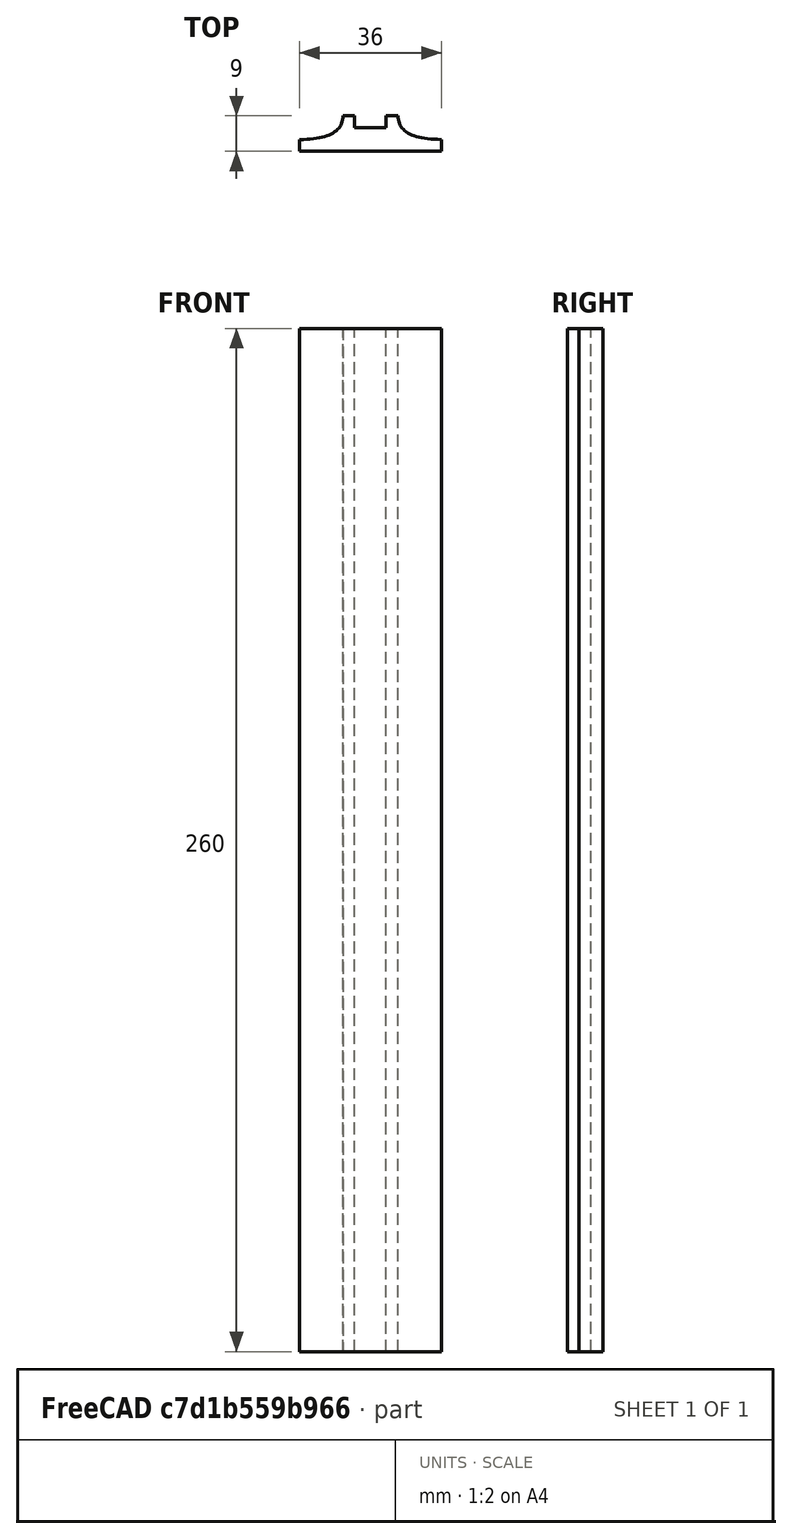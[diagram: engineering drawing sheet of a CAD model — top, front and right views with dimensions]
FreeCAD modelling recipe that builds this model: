
FCSTD DOCUMENT  (FreeCAD 0.19R0.19.2)
Label: laptopStand304
License: All rights reserved
LicenseURL: http://en.wikipedia.org/wiki/All_rights_reserved
objects: Sketcher::SketchObject×12, Part::Extrusion×1
note: 13 computed .brp shape members not serialized (recipe doc carries the construction recipe); baked Part::Feature solids carry a one-line shape summary decoded from their .brp

FEATURE [Sketcher::SketchObject] Sketch001  label="legTop"
  FullyConstrained = true
  MapMode = 4
  Placement = pos=(0,0,0) rot=(0.57735,0.57735,0.57735;2.0944rad)
  sketch-geometry (41):
    g0: BSplineCurve PolesCount=3 KnotsCount=2 Degree=2 IsPeriodic=0
    g1: ArcOfCircle CenterX=73.1223 CenterY=-32.291 CenterZ=0 NormalX=0 NormalY=0 NormalZ=1 AngleXU=0 Radius=13 StartAngle=5.92268 EndAngle=9.06428
    g2: ArcOfCircle CenterX=66.7816 CenterY=-49.1439 CenterZ=0 NormalX=0 NormalY=0 NormalZ=1 AngleXU=0 Radius=13 StartAngle=2.78068 EndAngle=5.92131
    g3-g6: Circle x4 (B-spline internal-alignment scaffolding for g7; pole/knot coordinates omitted)
    g7: BSplineCurve PolesCount=4 KnotsCount=2 Degree=3 IsPeriodic=0
    g8: GeomPoint X=28.8094 Y=-19.0875 Z=0
    g9: GeomPoint X=47.0443 Y=-50.4712 Z=0
    g10: Circle CenterX=53.5586 CenterY=-23.2695 CenterZ=0 NormalX=0 NormalY=0 NormalZ=1 AngleXU=0 Radius=3.24518
    g11: LineSegment StartX=17.2232 StartY=-16.0875 StartZ=0 EndX=17.2232 EndY=-19.0875 EndZ=0
    g12: ArcOfCircle CenterX=17.2475 CenterY=-181.166 CenterZ=0 NormalX=0 NormalY=0 NormalZ=1 AngleXU=0 Radius=13 StartAngle=5.92268 EndAngle=7.49361
    g13: ArcOfCircle CenterX=29.5716 CenterY=-148.408 CenterZ=0 NormalX=0 NormalY=0 NormalZ=1 AngleXU=0 Radius=13 StartAngle=4.35228 EndAngle=5.92131
    g14: ArcOfCircle CenterX=35.8967 CenterY=-131.555 CenterZ=0 NormalX=0 NormalY=0 NormalZ=1 AngleXU=0 Radius=13 StartAngle=5.92268 EndAngle=7.49902
    g15: ArcOfCircle CenterX=48.1805 CenterY=-98.7782 CenterZ=0 NormalX=0 NormalY=0 NormalZ=1 AngleXU=0 Radius=13 StartAngle=4.34921 EndAngle=5.92131
    g16: ArcOfCircle CenterX=54.5183 CenterY=-81.9247 CenterZ=0 NormalX=0 NormalY=0 NormalZ=1 AngleXU=0 Radius=13 StartAngle=5.92268 EndAngle=8.70432
    g17: ArcOfCircle CenterX=20.184 CenterY=-217.506 CenterZ=0 NormalX=0 NormalY=0 NormalZ=1 AngleXU=0 Radius=3.81084 StartAngle=1.88136 EndAngle=6.80465
    g18: ArcOfCircle CenterX=36.3663 CenterY=-113.042 CenterZ=0 NormalX=0 NormalY=0 NormalZ=1 AngleXU=0 Radius=3.60555 StartAngle=0.230024 EndAngle=5.3372
    g19: ArcOfCircle CenterX=17.7945 CenterY=-162.686 CenterZ=0 NormalX=0 NormalY=0 NormalZ=1 AngleXU=0 Radius=3.60555 StartAngle=0.230024 EndAngle=5.3372
    g20: ArcOfCircle CenterX=49.8795 CenterY=-62.6074 CenterZ=0 NormalX=0 NormalY=0 NormalZ=1 AngleXU=0 Radius=3.84187 StartAngle=4.46973 EndAngle=9.40343
    g21: LineSegment StartX=48.9563 StartY=-66.3367 StartZ=0 EndX=44.7488 EndY=-73.3482 EndZ=0
    g22: LineSegment StartX=41.085 StartY=-66.3176 StartZ=0 EndX=46.0385 EndY=-62.5254 EndZ=0
    g23: LineSegment StartX=47.0443 StartY=-50.4712 StartZ=0 EndX=41.085 EndY=-66.3176 EndZ=0
    g24: LineSegment StartX=17.2232 StartY=-16.0875 StartZ=0 EndX=117.223 EndY=-16.0875 EndZ=0
    g25: LineSegment StartX=28.8094 StartY=-19.0875 StartZ=0 EndX=17.2232 EndY=-19.0875 EndZ=0
    g26: LineSegment StartX=117.223 StartY=-16.0875 StartZ=0 EndX=117.223 EndY=-19.0875 EndZ=0
    g27: LineSegment StartX=85.2866 StartY=-36.8766 StartZ=0 EndX=78.9396 EndY=-53.7463 EndZ=0
    g28: LineSegment StartX=60.9579 StartY=-27.7053 StartZ=0 EndX=54.6191 EndY=-44.5532 EndZ=0
    g29: LineSegment StartX=23.4884 StartY=-215.608 StartZ=0 EndX=94.6579 EndY=-26.1359 EndZ=0
    g30: LineSegment StartX=19.0195 StartY=-213.878 StartZ=0 EndX=29.4118 EndY=-185.752 EndZ=0
    g31: LineSegment StartX=22.7134 StartY=-166.661 StartZ=0 EndX=21.8316 EndY=-169.001 EndZ=0
    g32: LineSegment StartX=19.9036 StartY=-165.61 StartZ=0 EndX=22.7134 EndY=-166.661 EndZ=0
    g33: LineSegment StartX=21.3051 StartY=-161.864 StartZ=0 EndX=24.1149 EndY=-162.915 EndZ=0
    g34: LineSegment StartX=24.1149 StartY=-162.915 StartZ=0 EndX=24.9906 EndY=-160.574 EndZ=0
    g35: LineSegment StartX=41.7296 StartY=-153.01 StartZ=0 EndX=48.061 EndY=-136.14 EndZ=0
    g36: LineSegment StartX=41.2852 StartY=-117.017 StartZ=0 EndX=40.4148 EndY=-119.365 EndZ=0
    g37: LineSegment StartX=38.4753 StartY=-115.966 StartZ=0 EndX=41.2852 EndY=-117.017 EndZ=0
    g38: LineSegment StartX=39.8769 StartY=-112.22 StartZ=0 EndX=42.6867 EndY=-113.271 EndZ=0
    g39: LineSegment StartX=42.6867 StartY=-113.271 StartZ=0 EndX=43.5622 EndY=-110.93 EndZ=0
    g40: LineSegment StartX=66.6827 StartY=-86.5104 StartZ=0 EndX=60.3386 EndY=-103.381 EndZ=0
  constraints (65):
    c: Block(g0)
    c: Block(g1)
    c: Block(g2)
    c: Weight(g3) = 1
    c: Equal(g3,g4)
    c: Equal(g3,g5)
    c: Equal(g3,g6)
    c: InternalAlignment(g3-g6 -> g7) x4
    c: InternalAlignment(g8,g7)
    c: InternalAlignment(g9,g7)
    c: Block(g10)
    c: Block(g7)
    c: Vertical(g11)
    c: Block(g12)
    c: Block(g13)
    c: Block(g14)
    c: Block(g15)
    c: Block(g16)
    c: Block(g17)
    c: Block(g18)
    c: Block(g19)
    c: Block(g20)
    c: Coincident(g21,g20)
    c: Coincident(g21,g16)
    c: Coincident(g22,g20)
    c: Block(g22)
    c: Coincident(g23,g7)
    c: Coincident(g23,g22)
    c: Coincident(g24,g11)
    c: Horizontal(g24)
    c: Coincident(g25,g7)
    c: Coincident(g25,g11)
    c: Horizontal(g25)
    c: Coincident(g26,g24)
    c: Coincident(g26,g0)
    c: Vertical(g26)
    c: Block(g24)
    c: Coincident(g27,g1)
    c: Coincident(g27,g2)
    c: Coincident(g28,g1)
    c: Coincident(g28,g2)
    c: Coincident(g29,g17)
    c: Coincident(g29,g0)
    c: Coincident(g30,g17)
    c: Coincident(g30,g12)
    c: Coincident(g31,g12)
    c: Coincident(g32,g19)
    c: Coincident(g32,g31)
    c: Block(g31)
    c: Coincident(g33,g19)
    c: Coincident(g34,g33)
    c: Coincident(g34,g13)
    c: Block(g34)
    c: Coincident(g35,g13)
    c: Coincident(g35,g14)
    c: Coincident(g36,g14)
    c: Coincident(g37,g18)
    c: Coincident(g37,g36)
    c: Block(g36)
    c: Coincident(g38,g18)
    c: Coincident(g39,g38)
    c: Coincident(g39,g15)
    c: Block(g39)
    c: Coincident(g40,g16)
    c: Coincident(g40,g15)
FEATURE [Sketcher::SketchObject] Sketch002
  FullyConstrained = true
  sketch-geometry (20):
    g0: LineSegment StartX=-2.77179 StartY=-200.304 StartZ=0 EndX=5.22821 EndY=-200.304 EndZ=0
    g1: LineSegment StartX=5.22821 StartY=-200.304 StartZ=0 EndX=5.22821 EndY=-197.304 EndZ=0
    g2: LineSegment StartX=-2.77179 StartY=-200.304 StartZ=0 EndX=-2.77179 EndY=-197.304 EndZ=0
    g3: LineSegment StartX=5.22821 StartY=-197.304 StartZ=0 EndX=8.22821 EndY=-197.304 EndZ=0
    g4: LineSegment StartX=-2.77179 StartY=-197.304 StartZ=0 EndX=-5.77179 EndY=-197.304 EndZ=0
    g5: LineSegment StartX=19.2282 StartY=-203.304 StartZ=0 EndX=19.2282 EndY=-206.304 EndZ=0
    g6: LineSegment StartX=-16.7718 StartY=-203.304 StartZ=0 EndX=-16.7718 EndY=-206.304 EndZ=0
    g7: LineSegment StartX=-16.7718 StartY=-206.304 StartZ=0 EndX=19.2282 EndY=-206.304 EndZ=0
    g8: Circle CenterX=-16.7718 CenterY=-203.304 CenterZ=0 NormalX=0 NormalY=0 NormalZ=1 AngleXU=0 Radius=1
    g9: Circle CenterX=-5.77179 CenterY=-203.304 CenterZ=0 NormalX=0 NormalY=0 NormalZ=1 AngleXU=0 Radius=1
    g10: Circle CenterX=-5.77179 CenterY=-197.304 CenterZ=0 NormalX=0 NormalY=0 NormalZ=1 AngleXU=0 Radius=1
    g11: BSplineCurve PolesCount=3 KnotsCount=2 Degree=2 IsPeriodic=0
    g12: GeomPoint X=-16.7718 Y=-203.304 Z=0
    g13: GeomPoint X=-5.77179 Y=-197.304 Z=0
    g14: Circle CenterX=19.2282 CenterY=-203.304 CenterZ=0 NormalX=0 NormalY=0 NormalZ=1 AngleXU=0 Radius=1
    g15: Circle CenterX=8.22821 CenterY=-203.304 CenterZ=0 NormalX=0 NormalY=0 NormalZ=1 AngleXU=0 Radius=1
    g16: Circle CenterX=8.22821 CenterY=-197.304 CenterZ=0 NormalX=0 NormalY=0 NormalZ=1 AngleXU=0 Radius=1
    g17: BSplineCurve PolesCount=3 KnotsCount=2 Degree=2 IsPeriodic=0
    g18: GeomPoint X=19.2282 Y=-203.304 Z=0
    g19: GeomPoint X=8.22821 Y=-197.304 Z=0
  constraints (41):
    c: Horizontal(g0)
    c: Distance(g0) = 8
    c: Coincident(g1,g0)
    c: Vertical(g1)
    c: Distance(g1) = 3
    c: Coincident(g2,g0)
    c: Vertical(g2)
    c: Distance(g2) = 3
    c: Coincident(g3,g1)
    c: Horizontal(g3)
    c: Distance(g3) = 3
    c: Coincident(g4,g2)
    c: Horizontal(g4)
    c: Distance(g4) = 3
    c: Vertical(g5)
    c: Vertical(g6)
    c: Coincident(g7,g6)
    c: Coincident(g7,g5)
    c: Weight(g8) = 1
    c: Equal(g8,g9)
    c: Equal(g8,g10)
    c: Coincident(g11,g4)
    c: InternalAlignment(g8,g11)
    c: InternalAlignment(g9,g11)
    c: InternalAlignment(g10,g11)
    c: InternalAlignment(g12,g11)
    c: InternalAlignment(g13,g11)
    c: Coincident(g17,g5)
    c: Weight(g14) = 1
    c: Equal(g14,g15)
    c: Equal(g14,g16)
    c: Coincident(g17,g3)
    c: InternalAlignment(g14,g17)
    c: InternalAlignment(g15,g17)
    c: InternalAlignment(g16,g17)
    c: InternalAlignment(g18,g17)
    c: InternalAlignment(g19,g17)
    c: Block(g7)
    c: Block(g17)
    c: Block(g11)
    c: Block(g6)
FEATURE [Part::Extrusion] Extrude003
  Base = -> Sketch002
  Dir = (0,0,1)
  DirMode = 2
  FaceMakerClass = Part::FaceMakerBullseye
  LengthFwd = 260
  LengthRev = 0
  Solid = true
  Symmetric = false
FEATURE [Sketcher::SketchObject] Sketch003  label="original"
  FullyConstrained = false
  sketch-geometry (469):
    g0: LineSegment StartX=-42.9272 StartY=136.221 StartZ=0 EndX=-42.9272 EndY=-103.779 EndZ=0
    g1: LineSegment StartX=407.073 StartY=136.221 StartZ=0 EndX=407.073 EndY=-103.779 EndZ=0
    g2: ArcOfCircle CenterX=-26.9272 CenterY=-83.7794 CenterZ=0 NormalX=0 NormalY=0 NormalZ=1 AngleXU=0 Radius=8 StartAngle=3.14159 EndAngle=6.28319
    g3: ArcOfCircle CenterX=391.073 CenterY=-83.7794 CenterZ=0 NormalX=0 NormalY=0 NormalZ=1 AngleXU=0 Radius=8 StartAngle=3.14159 EndAngle=6.28319
    g4: Circle CenterX=175.022 CenterY=27.0628 CenterZ=0 NormalX=0 NormalY=0 NormalZ=1 AngleXU=0 Radius=1
    g5: Circle CenterX=179.022 CenterY=24.8665 CenterZ=0 NormalX=0 NormalY=0 NormalZ=1 AngleXU=0 Radius=1
    g6: Circle CenterX=179.022 CenterY=27.0628 CenterZ=0 NormalX=0 NormalY=0 NormalZ=1 AngleXU=0 Radius=1
    g7: BSplineCurve PolesCount=3 KnotsCount=2 Degree=2 IsPeriodic=0
    g8: GeomPoint X=175.022 Y=27.0628 Z=0
    g9: GeomPoint X=179.022 Y=27.0628 Z=0
    g10: Circle CenterX=189.124 CenterY=27.0628 CenterZ=0 NormalX=0 NormalY=0 NormalZ=1 AngleXU=0 Radius=1
    g11: Circle CenterX=185.124 CenterY=24.8665 CenterZ=0 NormalX=0 NormalY=0 NormalZ=1 AngleXU=0 Radius=1
    g12: Circle CenterX=185.124 CenterY=27.0628 CenterZ=0 NormalX=0 NormalY=0 NormalZ=1 AngleXU=0 Radius=1
    g13: BSplineCurve PolesCount=3 KnotsCount=2 Degree=2 IsPeriodic=0
    g14: GeomPoint X=189.124 Y=27.0628 Z=0
    g15: GeomPoint X=185.124 Y=27.0628 Z=0
    g16: Circle CenterX=175.022 CenterY=5.37834 CenterZ=0 NormalX=0 NormalY=0 NormalZ=1 AngleXU=0 Radius=1
    g17: Circle CenterX=179.022 CenterY=7.57463 CenterZ=0 NormalX=0 NormalY=0 NormalZ=1 AngleXU=0 Radius=1
    g18: Circle CenterX=179.022 CenterY=5.34704 CenterZ=0 NormalX=0 NormalY=0 NormalZ=1 AngleXU=0 Radius=1
    g19: BSplineCurve PolesCount=3 KnotsCount=2 Degree=2 IsPeriodic=0
    g20: GeomPoint X=175.022 Y=5.37834 Z=0
    g21: GeomPoint X=179.022 Y=5.34704 Z=0
    g22: Circle CenterX=189.124 CenterY=5.37834 CenterZ=0 NormalX=0 NormalY=0 NormalZ=1 AngleXU=0 Radius=1
    g23: Circle CenterX=185.124 CenterY=7.57463 CenterZ=0 NormalX=0 NormalY=0 NormalZ=1 AngleXU=0 Radius=1
    g24: Circle CenterX=185.124 CenterY=5.34704 CenterZ=0 NormalX=0 NormalY=0 NormalZ=1 AngleXU=0 Radius=1
    g25: BSplineCurve PolesCount=3 KnotsCount=2 Degree=2 IsPeriodic=0
    g26: GeomPoint X=189.124 Y=5.37834 Z=0
    g27: GeomPoint X=185.124 Y=5.34704 Z=0
    g28: Circle CenterX=165.871 CenterY=18.1458 CenterZ=0 NormalX=0 NormalY=0 NormalZ=1 AngleXU=0 Radius=1
    g29: Circle CenterX=169.377 CenterY=16.2206 CenterZ=0 NormalX=0 NormalY=0 NormalZ=1 AngleXU=0 Radius=1
    g30: Circle CenterX=165.871 CenterY=14.2956 CenterZ=0 NormalX=0 NormalY=0 NormalZ=1 AngleXU=0 Radius=1
    g31: BSplineCurve PolesCount=3 KnotsCount=2 Degree=2 IsPeriodic=0
    g32: GeomPoint X=165.871 Y=18.1458 Z=0
    g33: GeomPoint X=165.871 Y=14.2956 Z=0
    g34: Circle CenterX=198.275 CenterY=18.1318 CenterZ=0 NormalX=0 NormalY=0 NormalZ=1 AngleXU=0 Radius=1
    g35: Circle CenterX=194.768 CenterY=16.2206 CenterZ=0 NormalX=0 NormalY=0 NormalZ=1 AngleXU=0 Radius=1
    g36: Circle CenterX=198.264 CenterY=14.2963 CenterZ=0 NormalX=0 NormalY=0 NormalZ=1 AngleXU=0 Radius=1
    g37: BSplineCurve PolesCount=3 KnotsCount=2 Degree=2 IsPeriodic=0
    g38: GeomPoint X=198.275 Y=18.1318 Z=0
    g39: GeomPoint X=198.264 Y=14.2963 Z=0
    g40: LineSegment StartX=407.073 StartY=-103.779 StartZ=0 EndX=-42.9272 EndY=-103.779 EndZ=0
    g41: Circle CenterX=125.607 CenterY=54.1951 CenterZ=0 NormalX=0 NormalY=0 NormalZ=1 AngleXU=0 Radius=1
    g42: Circle CenterX=139.632 CenterY=46.4944 CenterZ=0 NormalX=0 NormalY=0 NormalZ=1 AngleXU=0 Radius=1
    g43: Circle CenterX=127.326 CenterY=56.7187 CenterZ=0 NormalX=0 NormalY=0 NormalZ=1 AngleXU=0 Radius=1
    g44: BSplineCurve PolesCount=3 KnotsCount=2 Degree=2 IsPeriodic=0
    g45: GeomPoint X=125.607 Y=54.1951 Z=0
    g46: GeomPoint X=127.326 Y=56.7187 Z=0
    g47: Circle CenterX=236.824 CenterY=56.7187 CenterZ=0 NormalX=0 NormalY=0 NormalZ=1 AngleXU=0 Radius=1
    g48: Circle CenterX=224.513 CenterY=46.4944 CenterZ=0 NormalX=0 NormalY=0 NormalZ=1 AngleXU=0 Radius=1
    g49: Circle CenterX=238.538 CenterY=54.1951 CenterZ=0 NormalX=0 NormalY=0 NormalZ=1 AngleXU=0 Radius=1
    g50: BSplineCurve PolesCount=3 KnotsCount=2 Degree=2 IsPeriodic=0
    g51: GeomPoint X=236.824 Y=56.7187 Z=0
    g52: GeomPoint X=238.538 Y=54.1951 Z=0
    g53: Circle CenterX=238.538 CenterY=-21.7516 CenterZ=0 NormalX=0 NormalY=0 NormalZ=1 AngleXU=0 Radius=1
    g54: Circle CenterX=224.513 CenterY=-14.0532 CenterZ=0 NormalX=0 NormalY=0 NormalZ=1 AngleXU=0 Radius=1
    g55: Circle CenterX=236.584 CenterY=-24.2775 CenterZ=0 NormalX=0 NormalY=0 NormalZ=1 AngleXU=0 Radius=1
    g56: BSplineCurve PolesCount=3 KnotsCount=2 Degree=2 IsPeriodic=0
    g57: GeomPoint X=238.538 Y=-21.7516 Z=0
    g58: GeomPoint X=236.584 Y=-24.2775 Z=0
    g59: Circle CenterX=125.607 CenterY=-21.7539 CenterZ=0 NormalX=0 NormalY=0 NormalZ=1 AngleXU=0 Radius=1
    g60: Circle CenterX=139.632 CenterY=-14.0532 CenterZ=0 NormalX=0 NormalY=0 NormalZ=1 AngleXU=0 Radius=1
    g61: Circle CenterX=127.325 CenterY=-24.2775 CenterZ=0 NormalX=0 NormalY=0 NormalZ=1 AngleXU=0 Radius=1
    g62: BSplineCurve PolesCount=3 KnotsCount=2 Degree=2 IsPeriodic=0
    g63: GeomPoint X=125.607 Y=-21.7539 Z=0
    g64: GeomPoint X=127.325 Y=-24.2775 Z=0
    g65: Circle CenterX=302.996 CenterY=111.695 CenterZ=0 NormalX=0 NormalY=0 NormalZ=1 AngleXU=0 Radius=1
    g66: Circle CenterX=306.073 CenterY=114.251 CenterZ=0 NormalX=0 NormalY=0 NormalZ=1 AngleXU=0 Radius=1
    g67: Circle CenterX=306.073 CenterY=110.251 CenterZ=0 NormalX=0 NormalY=0 NormalZ=1 AngleXU=0 Radius=1
    g68: BSplineCurve PolesCount=3 KnotsCount=2 Degree=2 IsPeriodic=0
    g69: GeomPoint X=302.996 Y=111.695 Z=0
    g70: GeomPoint X=306.073 Y=110.251 Z=0
    g71: Circle CenterX=306.073 CenterY=95.2763 CenterZ=0 NormalX=0 NormalY=0 NormalZ=1 AngleXU=0 Radius=1
    g72: Circle CenterX=306.073 CenterY=91.2763 CenterZ=0 NormalX=0 NormalY=0 NormalZ=1 AngleXU=0 Radius=1
    g73: Circle CenterX=302.567 CenterY=89.3511 CenterZ=0 NormalX=0 NormalY=0 NormalZ=1 AngleXU=0 Radius=1
    g74: BSplineCurve PolesCount=3 KnotsCount=2 Degree=2 IsPeriodic=0
    g75: GeomPoint X=306.073 Y=95.2763 Z=0
    g76: GeomPoint X=302.567 Y=89.3511 Z=0
    g77: LineSegment StartX=306.073 StartY=110.251 StartZ=0 EndX=306.073 EndY=95.2763 EndZ=0
    g78: LineSegment StartX=302.996 StartY=111.695 StartZ=0 EndX=236.824 EndY=56.7187 EndZ=0
    g79: LineSegment StartX=238.538 StartY=54.1951 StartZ=0 EndX=302.567 EndY=89.3511 EndZ=0
    g80: Circle CenterX=61.1496 CenterY=111.695 CenterZ=0 NormalX=0 NormalY=0 NormalZ=1 AngleXU=0 Radius=1
    g81: Circle CenterX=58.0728 CenterY=114.251 CenterZ=0 NormalX=0 NormalY=0 NormalZ=1 AngleXU=0 Radius=1
    g82: Circle CenterX=58.0728 CenterY=110.251 CenterZ=0 NormalX=0 NormalY=0 NormalZ=1 AngleXU=0 Radius=1
    g83: BSplineCurve PolesCount=3 KnotsCount=2 Degree=2 IsPeriodic=0
    g84: GeomPoint X=61.1496 Y=111.695 Z=0
    g85: GeomPoint X=58.0728 Y=110.251 Z=0
    g86: Circle CenterX=61.5791 CenterY=89.3511 CenterZ=0 NormalX=0 NormalY=0 NormalZ=1 AngleXU=0 Radius=1
    g87: Circle CenterX=58.0728 CenterY=91.2763 CenterZ=0 NormalX=0 NormalY=0 NormalZ=1 AngleXU=0 Radius=1
    g88: Circle CenterX=58.0728 CenterY=95.2763 CenterZ=0 NormalX=0 NormalY=0 NormalZ=1 AngleXU=0 Radius=1
    g89: BSplineCurve PolesCount=3 KnotsCount=2 Degree=2 IsPeriodic=0
    g90: GeomPoint X=61.5791 Y=89.3511 Z=0
    g91: GeomPoint X=58.0728 Y=95.2763 Z=0
    g92: LineSegment StartX=58.0728 StartY=110.251 StartZ=0 EndX=58.0728 EndY=95.2763 EndZ=0
    g93: LineSegment StartX=61.1496 StartY=111.695 StartZ=0 EndX=127.326 EndY=56.7187 EndZ=0
    g94: LineSegment StartX=125.607 StartY=54.1951 StartZ=0 EndX=61.5791 EndY=89.3511 EndZ=0
    g95: Circle CenterX=61.5791 CenterY=-56.9099 CenterZ=0 NormalX=0 NormalY=0 NormalZ=1 AngleXU=0 Radius=1
    g96: Circle CenterX=58.0728 CenterY=-58.8351 CenterZ=0 NormalX=0 NormalY=0 NormalZ=1 AngleXU=0 Radius=1
    g97: Circle CenterX=58.0728 CenterY=-62.8351 CenterZ=0 NormalX=0 NormalY=0 NormalZ=1 AngleXU=0 Radius=1
    g98: BSplineCurve PolesCount=3 KnotsCount=2 Degree=2 IsPeriodic=0
    g99: GeomPoint X=61.5791 Y=-56.9099 Z=0
    g100: GeomPoint X=58.0728 Y=-62.8351 Z=0
    g101: Circle CenterX=58.0728 CenterY=-77.8102 CenterZ=0 NormalX=0 NormalY=0 NormalZ=1 AngleXU=0 Radius=1
    g102: Circle CenterX=58.0728 CenterY=-81.8102 CenterZ=0 NormalX=0 NormalY=0 NormalZ=1 AngleXU=0 Radius=1
    g103: Circle CenterX=61.1496 CenterY=-79.2541 CenterZ=0 NormalX=0 NormalY=0 NormalZ=1 AngleXU=0 Radius=1
    g104: BSplineCurve PolesCount=3 KnotsCount=2 Degree=2 IsPeriodic=0
    g105: GeomPoint X=58.0728 Y=-77.8102 Z=0
    g106: GeomPoint X=61.1496 Y=-79.2541 Z=0
    g107: LineSegment StartX=58.0728 StartY=-62.8351 StartZ=0 EndX=58.0728 EndY=-77.8102 EndZ=0
    g108: LineSegment StartX=61.1496 StartY=-79.2541 StartZ=0 EndX=127.325 EndY=-24.2775 EndZ=0
    g109: LineSegment StartX=125.607 StartY=-21.7539 StartZ=0 EndX=61.5791 EndY=-56.9099 EndZ=0
    g110: Circle CenterX=302.567 CenterY=-56.9099 CenterZ=0 NormalX=0 NormalY=0 NormalZ=1 AngleXU=0 Radius=1
    g111: Circle CenterX=306.073 CenterY=-58.8351 CenterZ=0 NormalX=0 NormalY=0 NormalZ=1 AngleXU=0 Radius=1
    g112: Circle CenterX=306.073 CenterY=-62.8351 CenterZ=0 NormalX=0 NormalY=0 NormalZ=1 AngleXU=0 Radius=1
    g113: BSplineCurve PolesCount=3 KnotsCount=2 Degree=2 IsPeriodic=0
    g114: GeomPoint X=302.567 Y=-56.9099 Z=0
    g115: GeomPoint X=306.073 Y=-62.8351 Z=0
    g116: Circle CenterX=302.996 CenterY=-79.2541 CenterZ=0 NormalX=0 NormalY=0 NormalZ=1 AngleXU=0 Radius=1
    g117: Circle CenterX=306.073 CenterY=-81.8102 CenterZ=0 NormalX=0 NormalY=0 NormalZ=1 AngleXU=0 Radius=1
    g118: Circle CenterX=306.073 CenterY=-77.8102 CenterZ=0 NormalX=0 NormalY=0 NormalZ=1 AngleXU=0 Radius=1
    g119: BSplineCurve PolesCount=3 KnotsCount=2 Degree=2 IsPeriodic=0
    g120: GeomPoint X=302.996 Y=-79.2541 Z=0
    g121: GeomPoint X=306.073 Y=-77.8102 Z=0
    g122: LineSegment StartX=306.073 StartY=-62.8351 StartZ=0 EndX=306.073 EndY=-77.8102 EndZ=0
    g123: LineSegment StartX=302.996 StartY=-79.2541 StartZ=0 EndX=236.584 EndY=-24.2775 EndZ=0
    g124: LineSegment StartX=238.538 StartY=-21.7516 StartZ=0 EndX=302.567 EndY=-56.9099 EndZ=0
    g125: Circle CenterX=61.6457 CenterY=-88.8112 CenterZ=0 NormalX=0 NormalY=0 NormalZ=1 AngleXU=0 Radius=1
    g126: Circle CenterX=58.0728 CenterY=-91.7794 CenterZ=0 NormalX=0 NormalY=0 NormalZ=1 AngleXU=0 Radius=1
    g127: Circle CenterX=63.9135 CenterY=-91.7791 CenterZ=0 NormalX=0 NormalY=0 NormalZ=1 AngleXU=0 Radius=1
    g128: BSplineCurve PolesCount=3 KnotsCount=2 Degree=2 IsPeriodic=0
    g129: GeomPoint X=61.6457 Y=-88.8112 Z=0
    g130: GeomPoint X=63.9135 Y=-91.7791 Z=0
    g131: Circle CenterX=179.022 CenterY=-85.8163 CenterZ=0 NormalX=0 NormalY=0 NormalZ=1 AngleXU=0 Radius=1
    g132: Circle CenterX=179.022 CenterY=-91.7794 CenterZ=0 NormalX=0 NormalY=0 NormalZ=1 AngleXU=0 Radius=1
    g133: Circle CenterX=171.895 CenterY=-91.7791 CenterZ=0 NormalX=0 NormalY=0 NormalZ=1 AngleXU=0 Radius=1
    g134: BSplineCurve PolesCount=3 KnotsCount=2 Degree=2 IsPeriodic=0
    g135: GeomPoint X=179.022 Y=-85.8163 Z=0
    g136: GeomPoint X=171.895 Y=-91.7791 Z=0
    g137: Circle CenterX=185.124 CenterY=-86.2028 CenterZ=0 NormalX=0 NormalY=0 NormalZ=1 AngleXU=0 Radius=1
    g138: Circle CenterX=185.124 CenterY=-91.7794 CenterZ=0 NormalX=0 NormalY=0 NormalZ=1 AngleXU=0 Radius=1
    g139: Circle CenterX=191.747 CenterY=-91.7794 CenterZ=0 NormalX=0 NormalY=0 NormalZ=1 AngleXU=0 Radius=1
    g140: BSplineCurve PolesCount=3 KnotsCount=2 Degree=2 IsPeriodic=0
    g141: GeomPoint X=185.124 Y=-86.2028 Z=0
    g142: GeomPoint X=191.747 Y=-91.7794 Z=0
    g143: Circle CenterX=299.888 CenterY=-86.6413 CenterZ=0 NormalX=0 NormalY=0 NormalZ=1 AngleXU=0 Radius=1
    g144: Circle CenterX=306.073 CenterY=-91.7794 CenterZ=0 NormalX=0 NormalY=0 NormalZ=1 AngleXU=0 Radius=1
    g145: Circle CenterX=298.776 CenterY=-91.7794 CenterZ=0 NormalX=0 NormalY=0 NormalZ=1 AngleXU=0 Radius=1
    g146: BSplineCurve PolesCount=3 KnotsCount=2 Degree=2 IsPeriodic=0
    g147: GeomPoint X=299.888 Y=-86.6413 Z=0
    g148: GeomPoint X=298.776 Y=-91.7794 Z=0
    g149: LineSegment StartX=189.124 StartY=5.37834 StartZ=0 EndX=299.888 EndY=-86.6413 EndZ=0
    g150: LineSegment StartX=298.776 StartY=-91.7794 StartZ=0 EndX=191.747 EndY=-91.7794 EndZ=0
    g151: LineSegment StartX=185.124 StartY=-86.2028 StartZ=0 EndX=185.124 EndY=5.34704 EndZ=0
    g152: LineSegment StartX=179.022 StartY=5.34704 StartZ=0 EndX=179.022 EndY=-85.8163 EndZ=0
    g153: LineSegment StartX=171.895 StartY=-91.7791 StartZ=0 EndX=63.9135 EndY=-91.7791 EndZ=0
    g154: LineSegment StartX=61.6457 StartY=-88.8112 StartZ=0 EndX=175.022 EndY=5.37834 EndZ=0
    g155: Circle CenterX=302.073 CenterY=124.221 CenterZ=0 NormalX=0 NormalY=0 NormalZ=1 AngleXU=0 Radius=1
    g156: Circle CenterX=306.073 CenterY=124.221 CenterZ=0 NormalX=0 NormalY=0 NormalZ=1 AngleXU=0 Radius=1
    g157: Circle CenterX=302.996 CenterY=121.665 CenterZ=0 NormalX=0 NormalY=0 NormalZ=1 AngleXU=0 Radius=1
    g158: BSplineCurve PolesCount=3 KnotsCount=2 Degree=2 IsPeriodic=0
    g159: GeomPoint X=302.073 Y=124.221 Z=0
    g160: GeomPoint X=302.996 Y=121.665 Z=0
    g161: Circle CenterX=189.124 CenterY=124.221 CenterZ=0 NormalX=0 NormalY=0 NormalZ=1 AngleXU=0 Radius=1
    g162: Circle CenterX=185.124 CenterY=124.221 CenterZ=0 NormalX=0 NormalY=0 NormalZ=1 AngleXU=0 Radius=1
    g163: Circle CenterX=185.124 CenterY=120.221 CenterZ=0 NormalX=0 NormalY=0 NormalZ=1 AngleXU=0 Radius=1
    g164: BSplineCurve PolesCount=3 KnotsCount=2 Degree=2 IsPeriodic=0
    g165: GeomPoint X=189.124 Y=124.221 Z=0
    g166: GeomPoint X=185.124 Y=120.221 Z=0
    g167: Circle CenterX=175.022 CenterY=124.221 CenterZ=0 NormalX=0 NormalY=0 NormalZ=1 AngleXU=0 Radius=1
    g168: Circle CenterX=179.022 CenterY=124.221 CenterZ=0 NormalX=0 NormalY=0 NormalZ=1 AngleXU=0 Radius=1
    g169: Circle CenterX=179.022 CenterY=120.221 CenterZ=0 NormalX=0 NormalY=0 NormalZ=1 AngleXU=0 Radius=1
    g170: BSplineCurve PolesCount=3 KnotsCount=2 Degree=2 IsPeriodic=0
    g171: GeomPoint X=175.022 Y=124.221 Z=0
    g172: GeomPoint X=179.022 Y=120.221 Z=0
    g173: Circle CenterX=62.0728 CenterY=124.221 CenterZ=0 NormalX=0 NormalY=0 NormalZ=1 AngleXU=0 Radius=1
    g174: Circle CenterX=58.0728 CenterY=124.221 CenterZ=0 NormalX=0 NormalY=0 NormalZ=1 AngleXU=0 Radius=1
    g175: Circle CenterX=61.1496 CenterY=121.665 CenterZ=0 NormalX=0 NormalY=0 NormalZ=1 AngleXU=0 Radius=1
    g176: BSplineCurve PolesCount=3 KnotsCount=2 Degree=2 IsPeriodic=0
    g177: GeomPoint X=62.0728 Y=124.221 Z=0
    g178: GeomPoint X=61.1496 Y=121.665 Z=0
    g179: LineSegment StartX=179.022 StartY=120.221 StartZ=0 EndX=179.022 EndY=27.0628 EndZ=0
    g180: LineSegment StartX=185.124 StartY=27.0628 StartZ=0 EndX=185.124 EndY=120.221 EndZ=0
    g181: LineSegment StartX=302.996 StartY=121.665 StartZ=0 EndX=189.124 EndY=27.0628 EndZ=0
    g182: LineSegment StartX=175.022 StartY=27.0628 StartZ=0 EndX=61.1496 EndY=121.665 EndZ=0
    g183: Circle CenterX=61.5791 CenterY=75.4095 CenterZ=0 NormalX=0 NormalY=0 NormalZ=1 AngleXU=0 Radius=1
    g184: Circle CenterX=58.0728 CenterY=77.3346 CenterZ=0 NormalX=0 NormalY=0 NormalZ=1 AngleXU=0 Radius=1
    g185: Circle CenterX=58.0728 CenterY=73.3346 CenterZ=0 NormalX=0 NormalY=0 NormalZ=1 AngleXU=0 Radius=1
    g186: BSplineCurve PolesCount=3 KnotsCount=2 Degree=2 IsPeriodic=0
    g187: GeomPoint X=61.5791 Y=75.4095 Z=0
    g188: GeomPoint X=58.0728 Y=73.3346 Z=0
    g189: Circle CenterX=58.0728 CenterY=-40.8935 CenterZ=0 NormalX=0 NormalY=0 NormalZ=1 AngleXU=0 Radius=1
    g190: Circle CenterX=58.0728 CenterY=-44.8935 CenterZ=0 NormalX=0 NormalY=0 NormalZ=1 AngleXU=0 Radius=1
    g191: Circle CenterX=61.5791 CenterY=-42.9683 CenterZ=0 NormalX=0 NormalY=0 NormalZ=1 AngleXU=0 Radius=1
    g192: BSplineCurve PolesCount=3 KnotsCount=2 Degree=2 IsPeriodic=0
    g193: GeomPoint X=58.0728 Y=-40.8935 Z=0
    g194: GeomPoint X=61.5791 Y=-42.9683 Z=0
    g195: LineSegment StartX=61.5791 StartY=-42.9683 StartZ=0 EndX=165.871 EndY=14.2956 EndZ=0
    g196: LineSegment StartX=165.871 StartY=18.1458 StartZ=0 EndX=61.5791 EndY=75.4095 EndZ=0
    g197: LineSegment StartX=58.0728 StartY=73.3346 StartZ=0 EndX=58.0728 EndY=-40.8935 EndZ=0
    g198: Circle CenterX=302.567 CenterY=-42.9683 CenterZ=0 NormalX=0 NormalY=0 NormalZ=1 AngleXU=0 Radius=1
    g199: Circle CenterX=306.073 CenterY=-44.8935 CenterZ=0 NormalX=0 NormalY=0 NormalZ=1 AngleXU=0 Radius=1
    g200: Circle CenterX=306.073 CenterY=-40.8935 CenterZ=0 NormalX=0 NormalY=0 NormalZ=1 AngleXU=0 Radius=1
    g201: BSplineCurve PolesCount=3 KnotsCount=2 Degree=2 IsPeriodic=0
    g202: GeomPoint X=302.567 Y=-42.9683 Z=0
    g203: GeomPoint X=306.073 Y=-40.8935 Z=0
    g204: Circle CenterX=306.073 CenterY=73.3346 CenterZ=0 NormalX=0 NormalY=0 NormalZ=1 AngleXU=0 Radius=1
    g205: Circle CenterX=306.073 CenterY=77.3346 CenterZ=0 NormalX=0 NormalY=0 NormalZ=1 AngleXU=0 Radius=1
    g206: Circle CenterX=302.535 CenterY=75.4095 CenterZ=0 NormalX=0 NormalY=0 NormalZ=1 AngleXU=0 Radius=1
    g207: BSplineCurve PolesCount=3 KnotsCount=2 Degree=2 IsPeriodic=0
    g208: GeomPoint X=306.073 Y=73.3346 Z=0
    g209: GeomPoint X=302.535 Y=75.4095 Z=0
    g210: LineSegment StartX=302.567 StartY=-42.9683 StartZ=0 EndX=198.264 EndY=14.2963 EndZ=0
    g211: LineSegment StartX=198.275 StartY=18.1318 StartZ=0 EndX=302.535 EndY=75.4095 EndZ=0
    g212: LineSegment StartX=306.073 StartY=73.3346 StartZ=0 EndX=306.073 EndY=-40.8935 EndZ=0
    g213: LineSegment StartX=322.073 StartY=105.865 StartZ=0 EndX=328.643 EndY=105.865 EndZ=0
    g214: LineSegment StartX=318.073 StartY=120.221 StartZ=0 EndX=318.073 EndY=109.865 EndZ=0
    g215: LineSegment StartX=336.157 StartY=107.779 StartZ=0 EndX=362.567 EndY=122.294 EndZ=0
    g216: Circle CenterX=362.073 CenterY=124.221 CenterZ=0 NormalX=0 NormalY=0 NormalZ=1 AngleXU=0 Radius=1
    g217: Circle CenterX=366.073 CenterY=124.221 CenterZ=0 NormalX=0 NormalY=0 NormalZ=1 AngleXU=0 Radius=1
    g218: Circle CenterX=362.567 CenterY=122.294 CenterZ=0 NormalX=0 NormalY=0 NormalZ=1 AngleXU=0 Radius=1
    g219: BSplineCurve PolesCount=3 KnotsCount=2 Degree=2 IsPeriodic=0
    g220: GeomPoint X=362.073 Y=124.221 Z=0
    g221: GeomPoint X=362.567 Y=122.294 Z=0
    g222: Circle CenterX=322.073 CenterY=124.221 CenterZ=0 NormalX=0 NormalY=0 NormalZ=1 AngleXU=0 Radius=1
    g223: Circle CenterX=318.073 CenterY=124.221 CenterZ=0 NormalX=0 NormalY=0 NormalZ=1 AngleXU=0 Radius=1
    g224: Circle CenterX=318.073 CenterY=120.221 CenterZ=0 NormalX=0 NormalY=0 NormalZ=1 AngleXU=0 Radius=1
    g225: BSplineCurve PolesCount=3 KnotsCount=2 Degree=2 IsPeriodic=0
    g226: GeomPoint X=322.073 Y=124.221 Z=0
    g227: GeomPoint X=318.073 Y=120.221 Z=0
    g228: Circle CenterX=322.073 CenterY=105.865 CenterZ=0 NormalX=0 NormalY=0 NormalZ=1 AngleXU=0 Radius=1
    g229: Circle CenterX=318.073 CenterY=105.865 CenterZ=0 NormalX=0 NormalY=0 NormalZ=1 AngleXU=0 Radius=1
    g230: Circle CenterX=318.073 CenterY=109.865 CenterZ=0 NormalX=0 NormalY=0 NormalZ=1 AngleXU=0 Radius=1
    g231: BSplineCurve PolesCount=3 KnotsCount=2 Degree=2 IsPeriodic=0
    g232: GeomPoint X=322.073 Y=105.865 Z=0
    g233: GeomPoint X=318.073 Y=109.865 Z=0
    g234: Circle CenterX=336.157 CenterY=107.779 CenterZ=0 NormalX=0 NormalY=0 NormalZ=1 AngleXU=0 Radius=1
    g235: Circle CenterX=332.651 CenterY=105.853 CenterZ=0 NormalX=0 NormalY=0 NormalZ=1 AngleXU=0 Radius=1
    g236: Circle CenterX=328.643 CenterY=105.865 CenterZ=0 NormalX=0 NormalY=0 NormalZ=1 AngleXU=0 Radius=1
    g237: BSplineCurve PolesCount=3 KnotsCount=2 Degree=2 IsPeriodic=0
    g238: GeomPoint X=336.157 Y=107.779 Z=0
    g239: GeomPoint X=328.643 Y=105.865 Z=0
    g240: LineSegment StartX=322.073 StartY=124.221 StartZ=0 EndX=362.073 EndY=124.221 EndZ=0
    g241: Circle CenterX=371.567 CenterY=-80.8644 CenterZ=0 NormalX=0 NormalY=0 NormalZ=1 AngleXU=0 Radius=1
    g242: Circle CenterX=375.073 CenterY=-82.7896 CenterZ=0 NormalX=0 NormalY=0 NormalZ=1 AngleXU=0 Radius=1
    g243: Circle CenterX=375.073 CenterY=-78.7896 CenterZ=0 NormalX=0 NormalY=0 NormalZ=1 AngleXU=0 Radius=1
    g244: BSplineCurve PolesCount=3 KnotsCount=2 Degree=2 IsPeriodic=0
    g245: GeomPoint X=371.567 Y=-80.8644 Z=0
    g246: GeomPoint X=375.073 Y=-78.7896 Z=0
    g247: Circle CenterX=321.579 CenterY=-53.4075 CenterZ=0 NormalX=0 NormalY=0 NormalZ=1 AngleXU=0 Radius=1
    g248: Circle CenterX=318.073 CenterY=-51.4823 CenterZ=0 NormalX=0 NormalY=0 NormalZ=1 AngleXU=0 Radius=1
    g249: Circle CenterX=318.073 CenterY=-47.4805 CenterZ=0 NormalX=0 NormalY=0 NormalZ=1 AngleXU=0 Radius=1
    g250: BSplineCurve PolesCount=3 KnotsCount=2 Degree=2 IsPeriodic=0
    g251: GeomPoint X=321.579 Y=-53.4075 Z=0
    g252: GeomPoint X=318.073 Y=-47.4805 Z=0
    g253: LineSegment StartX=371.567 StartY=-80.8644 StartZ=0 EndX=321.579 EndY=-53.4075 EndZ=0
    g254: Circle CenterX=321.579 CenterY=-67.3492 CenterZ=0 NormalX=0 NormalY=0 NormalZ=1 AngleXU=0 Radius=1
    g255: Circle CenterX=318.073 CenterY=-65.424 CenterZ=0 NormalX=0 NormalY=0 NormalZ=1 AngleXU=0 Radius=1
    g256: Circle CenterX=318.073 CenterY=-69.424 CenterZ=0 NormalX=0 NormalY=0 NormalZ=1 AngleXU=0 Radius=1
    g257: BSplineCurve PolesCount=3 KnotsCount=2 Degree=2 IsPeriodic=0
    g258: GeomPoint X=321.579 Y=-67.3492 Z=0
    g259: GeomPoint X=318.073 Y=-69.424 Z=0
    g260: Circle CenterX=362.567 CenterY=-89.8542 CenterZ=0 NormalX=0 NormalY=0 NormalZ=1 AngleXU=0 Radius=1
    g261: Circle CenterX=366.073 CenterY=-91.7794 CenterZ=0 NormalX=0 NormalY=0 NormalZ=1 AngleXU=0 Radius=1
    g262: Circle CenterX=362.073 CenterY=-91.7794 CenterZ=0 NormalX=0 NormalY=0 NormalZ=1 AngleXU=0 Radius=1
    g263: BSplineCurve PolesCount=3 KnotsCount=2 Degree=2 IsPeriodic=0
    g264: GeomPoint X=362.567 Y=-89.8542 Z=0
    g265: GeomPoint X=362.073 Y=-91.7794 Z=0
    g266: Circle CenterX=322.073 CenterY=-91.7794 CenterZ=0 NormalX=0 NormalY=0 NormalZ=1 AngleXU=0 Radius=1
    g267: Circle CenterX=318.073 CenterY=-91.7794 CenterZ=0 NormalX=0 NormalY=0 NormalZ=1 AngleXU=0 Radius=1
    g268: Circle CenterX=318.073 CenterY=-87.7794 CenterZ=0 NormalX=0 NormalY=0 NormalZ=1 AngleXU=0 Radius=1
    g269: BSplineCurve PolesCount=3 KnotsCount=2 Degree=2 IsPeriodic=0
    g270: GeomPoint X=322.073 Y=-91.7794 Z=0
    g271: GeomPoint X=318.073 Y=-87.7794 Z=0
    g272: LineSegment StartX=362.567 StartY=-89.8542 StartZ=0 EndX=321.579 EndY=-67.3492 EndZ=0
    g273: LineSegment StartX=318.073 StartY=-69.424 StartZ=0 EndX=318.073 EndY=-87.7794 EndZ=0
    g274: LineSegment StartX=322.073 StartY=-91.7794 StartZ=0 EndX=362.073 EndY=-91.7794 EndZ=0
    g275: Circle CenterX=2.07281 CenterY=124.221 CenterZ=0 NormalX=0 NormalY=0 NormalZ=1 AngleXU=0 Radius=1
    g276: Circle CenterX=1.57905 CenterY=122.295 CenterZ=0 NormalX=0 NormalY=0 NormalZ=1 AngleXU=0 Radius=1
    g277: BSplineCurve PolesCount=3 KnotsCount=2 Degree=2 IsPeriodic=0
    g278: GeomPoint X=2.07281 Y=124.221 Z=0
    g279: GeomPoint X=1.57905 Y=122.295 Z=0
    g280: Circle CenterX=42.0728 CenterY=124.221 CenterZ=0 NormalX=0 NormalY=0 NormalZ=1 AngleXU=0 Radius=1
    g281: Circle CenterX=46.0728 CenterY=124.221 CenterZ=0 NormalX=0 NormalY=0 NormalZ=1 AngleXU=0 Radius=1
    g282: Circle CenterX=46.0728 CenterY=120.221 CenterZ=0 NormalX=0 NormalY=0 NormalZ=1 AngleXU=0 Radius=1
    g283: BSplineCurve PolesCount=3 KnotsCount=2 Degree=2 IsPeriodic=0
    g284: GeomPoint X=42.0728 Y=124.221 Z=0
    g285: GeomPoint X=46.0728 Y=120.221 Z=0
    g286: Circle CenterX=46.0728 CenterY=109.865 CenterZ=0 NormalX=0 NormalY=0 NormalZ=1 AngleXU=0 Radius=1
    g287: Circle CenterX=46.0728 CenterY=105.865 CenterZ=0 NormalX=0 NormalY=0 NormalZ=1 AngleXU=0 Radius=1
    g288: Circle CenterX=42.0728 CenterY=105.865 CenterZ=0 NormalX=0 NormalY=0 NormalZ=1 AngleXU=0 Radius=1
    g289: BSplineCurve PolesCount=3 KnotsCount=2 Degree=2 IsPeriodic=0
    g290: GeomPoint X=46.0728 Y=109.865 Z=0
    g291: GeomPoint X=42.0728 Y=105.865 Z=0
    g292: Circle CenterX=35.5028 CenterY=105.865 CenterZ=0 NormalX=0 NormalY=0 NormalZ=1 AngleXU=0 Radius=1
    g293: Circle CenterX=31.5028 CenterY=105.865 CenterZ=0 NormalX=0 NormalY=0 NormalZ=1 AngleXU=0 Radius=1
    g294: Circle CenterX=27.9965 CenterY=107.79 CenterZ=0 NormalX=0 NormalY=0 NormalZ=1 AngleXU=0 Radius=1
    g295: BSplineCurve PolesCount=3 KnotsCount=2 Degree=2 IsPeriodic=0
    g296: GeomPoint X=35.5028 Y=105.865 Z=0
    g297: GeomPoint X=27.9965 Y=107.79 Z=0
    g298: LineSegment StartX=2.07281 StartY=124.221 StartZ=0 EndX=42.0728 EndY=124.221 EndZ=0
    g299: LineSegment StartX=46.0728 StartY=120.221 StartZ=0 EndX=46.0728 EndY=109.865 EndZ=0
    g300: LineSegment StartX=42.0728 StartY=105.865 StartZ=0 EndX=35.5028 EndY=105.865 EndZ=0
    g301: LineSegment StartX=27.9965 StartY=107.79 StartZ=0 EndX=1.57905 EndY=122.295 EndZ=0
    g302: Circle CenterX=42.5666 CenterY=-67.3492 CenterZ=0 NormalX=0 NormalY=0 NormalZ=1 AngleXU=0 Radius=1
    g303: Circle CenterX=46.0728 CenterY=-65.424 CenterZ=0 NormalX=0 NormalY=0 NormalZ=1 AngleXU=0 Radius=1
    g304: Circle CenterX=46.0728 CenterY=-69.424 CenterZ=0 NormalX=0 NormalY=0 NormalZ=1 AngleXU=0 Radius=1
    g305: BSplineCurve PolesCount=3 KnotsCount=2 Degree=2 IsPeriodic=0
    g306: GeomPoint X=42.5666 Y=-67.3492 Z=0
    g307: GeomPoint X=46.0728 Y=-69.424 Z=0
    g308: Circle CenterX=46.0728 CenterY=-87.7794 CenterZ=0 NormalX=0 NormalY=0 NormalZ=1 AngleXU=0 Radius=1
    g309: Circle CenterX=46.0728 CenterY=-91.7794 CenterZ=0 NormalX=0 NormalY=0 NormalZ=1 AngleXU=0 Radius=1
    g310: Circle CenterX=42.0728 CenterY=-91.7794 CenterZ=0 NormalX=0 NormalY=0 NormalZ=1 AngleXU=0 Radius=1
    g311: BSplineCurve PolesCount=3 KnotsCount=2 Degree=2 IsPeriodic=0
    g312: GeomPoint X=46.0728 Y=-87.7794 Z=0
    g313: GeomPoint X=42.0728 Y=-91.7794 Z=0
    g314: Circle CenterX=2.07281 CenterY=-91.7794 CenterZ=0 NormalX=0 NormalY=0 NormalZ=1 AngleXU=0 Radius=1
    g315: Circle CenterX=-1.92719 CenterY=-91.7794 CenterZ=0 NormalX=0 NormalY=0 NormalZ=1 AngleXU=0 Radius=1
    g316: Circle CenterX=1.57905 CenterY=-89.8542 CenterZ=0 NormalX=0 NormalY=0 NormalZ=1 AngleXU=0 Radius=1
    g317: BSplineCurve PolesCount=3 KnotsCount=2 Degree=2 IsPeriodic=0
    g318: GeomPoint X=2.07281 Y=-91.7794 Z=0
    g319: GeomPoint X=1.57905 Y=-89.8542 Z=0
    g320: LineSegment StartX=2.07281 StartY=-91.7794 StartZ=0 EndX=42.0728 EndY=-91.7794 EndZ=0
    g321: LineSegment StartX=46.0728 StartY=-87.7794 StartZ=0 EndX=46.0728 EndY=-69.424 EndZ=0
    g322: LineSegment StartX=42.5666 StartY=-67.3492 StartZ=0 EndX=1.57905 EndY=-89.8542 EndZ=0
    g323: Circle CenterX=322.073 CenterY=76.4095 CenterZ=0 NormalX=0 NormalY=0 NormalZ=1 AngleXU=0 Radius=4
    g324: BSplineCurve PolesCount=3 KnotsCount=2 Degree=2 IsPeriodic=0
    g325: GeomPoint X=318.073 Y=72.4095 Z=0
    g326: GeomPoint X=322.073 Y=76.4095 Z=0
    g327: Circle CenterX=375.073 CenterY=72.4095 CenterZ=0 NormalX=0 NormalY=0 NormalZ=1 AngleXU=0 Radius=1
    g328: Circle CenterX=375.073 CenterY=76.4095 CenterZ=0 NormalX=0 NormalY=0 NormalZ=1 AngleXU=0 Radius=1
    g329: Circle CenterX=371.073 CenterY=76.4095 CenterZ=0 NormalX=0 NormalY=0 NormalZ=1 AngleXU=0 Radius=1
    g330: BSplineCurve PolesCount=3 KnotsCount=2 Degree=2 IsPeriodic=0
    g331: GeomPoint X=375.073 Y=72.4095 Z=0
    g332: GeomPoint X=371.073 Y=76.4095 Z=0
    g333: LineSegment StartX=322.073 StartY=76.4095 StartZ=0 EndX=371.073 EndY=76.4095 EndZ=0
    g334: LineSegment StartX=318.073 StartY=72.4095 StartZ=0 EndX=318.073 EndY=-47.4805 EndZ=0
    g335: LineSegment StartX=375.073 StartY=72.4095 StartZ=0 EndX=375.073 EndY=-78.7896 EndZ=0
    g336: ArcOfCircle CenterX=-26.9272 CenterY=22.1087 CenterZ=0 NormalX=0 NormalY=0 NormalZ=1 AngleXU=0 Radius=4 StartAngle=5e-16 EndAngle=3.14159
    g337: LineSegment StartX=-22.9272 StartY=22.1087 StartZ=0 EndX=-18.9272 EndY=-83.7794 EndZ=0
    g338: LineSegment StartX=-34.9272 StartY=-83.7794 StartZ=0 EndX=-30.9272 EndY=22.1087 EndZ=0
    g339: ArcOfCircle CenterX=391.073 CenterY=22.1087 CenterZ=0 NormalX=0 NormalY=0 NormalZ=1 AngleXU=0 Radius=4 StartAngle=0 EndAngle=3.14159
    g340: LineSegment StartX=387.073 StartY=22.1087 StartZ=0 EndX=383.073 EndY=-83.7794 EndZ=0
    g341: LineSegment StartX=395.073 StartY=22.1087 StartZ=0 EndX=399.073 EndY=-83.7794 EndZ=0
    g342: Circle CenterX=-10.9272 CenterY=-78.7794 CenterZ=0 NormalX=0 NormalY=0 NormalZ=1 AngleXU=0 Radius=1
    g343: Circle CenterX=-10.9272 CenterY=-82.7794 CenterZ=0 NormalX=0 NormalY=0 NormalZ=1 AngleXU=0 Radius=1
    g344: Circle CenterX=-7.42095 CenterY=-80.8542 CenterZ=0 NormalX=0 NormalY=0 NormalZ=1 AngleXU=0 Radius=1
    g345: BSplineCurve PolesCount=3 KnotsCount=2 Degree=2 IsPeriodic=0
    g346: GeomPoint X=-10.9272 Y=-78.7794 Z=0
    g347: GeomPoint X=-7.42095 Y=-80.8542 Z=0
    g348: Circle CenterX=42.5666 CenterY=-53.4075 CenterZ=0 NormalX=0 NormalY=0 NormalZ=1 AngleXU=0 Radius=1
    g349: Circle CenterX=46.0728 CenterY=-51.4823 CenterZ=0 NormalX=0 NormalY=0 NormalZ=1 AngleXU=0 Radius=1
    g350: Circle CenterX=46.0728 CenterY=-47.4823 CenterZ=0 NormalX=0 NormalY=0 NormalZ=1 AngleXU=0 Radius=1
    g351: BSplineCurve PolesCount=3 KnotsCount=2 Degree=2 IsPeriodic=0
    g352: GeomPoint X=42.5666 Y=-53.4075 Z=0
    g353: GeomPoint X=46.0728 Y=-47.4823 Z=0
    g354: Circle CenterX=46.0728 CenterY=72.4095 CenterZ=0 NormalX=0 NormalY=0 NormalZ=1 AngleXU=0 Radius=1
    g355: Circle CenterX=46.0728 CenterY=76.4095 CenterZ=0 NormalX=0 NormalY=0 NormalZ=1 AngleXU=0 Radius=1
    g356: Circle CenterX=42.0728 CenterY=76.4095 CenterZ=0 NormalX=0 NormalY=0 NormalZ=1 AngleXU=0 Radius=1
    g357: BSplineCurve PolesCount=3 KnotsCount=2 Degree=2 IsPeriodic=0
    g358: GeomPoint X=46.0728 Y=72.4095 Z=0
    g359: GeomPoint X=42.0728 Y=76.4095 Z=0
    g360: Circle CenterX=-6.92719 CenterY=76.4095 CenterZ=0 NormalX=0 NormalY=0 NormalZ=1 AngleXU=0 Radius=1
    g361: Circle CenterX=-10.9272 CenterY=76.4095 CenterZ=0 NormalX=0 NormalY=0 NormalZ=1 AngleXU=0 Radius=1
    g362: Circle CenterX=-10.9272 CenterY=72.4095 CenterZ=0 NormalX=0 NormalY=0 NormalZ=1 AngleXU=0 Radius=1
    g363: BSplineCurve PolesCount=3 KnotsCount=2 Degree=2 IsPeriodic=0
    g364: GeomPoint X=-6.92719 Y=76.4095 Z=0
    g365: GeomPoint X=-10.9272 Y=72.4095 Z=0
    g366: LineSegment StartX=-10.9272 StartY=72.4095 StartZ=0 EndX=-10.9272 EndY=-78.7794 EndZ=0
    g367: LineSegment StartX=-7.42095 StartY=-80.8542 StartZ=0 EndX=42.5666 EndY=-53.4075 EndZ=0
    g368: LineSegment StartX=46.0728 StartY=-47.4823 StartZ=0 EndX=46.0728 EndY=72.4095 EndZ=0
    g369: LineSegment StartX=42.0728 StartY=76.4095 StartZ=0 EndX=-6.92719 EndY=76.4095 EndZ=0
    g370: LineSegment StartX=-42.9272 StartY=136.221 StartZ=0 EndX=407.073 EndY=136.221 EndZ=0
    g371: LineSegment StartX=232.072 StartY=136.221 StartZ=0 EndX=220.072 EndY=136.221 EndZ=0
    g372: LineSegment StartX=232.072 StartY=136.221 StartZ=0 EndX=232.072 EndY=124.221 EndZ=0
    g373: LineSegment StartX=220.072 StartY=136.221 StartZ=0 EndX=220.072 EndY=124.221 EndZ=0
    g374: LineSegment StartX=220.072 StartY=136.221 StartZ=0 EndX=226.072 EndY=136.221 EndZ=0
    g375: LineSegment StartX=220.072 StartY=136.221 StartZ=0 EndX=220.072 EndY=130.221 EndZ=0
    g376: LineSegment StartX=220.072 StartY=124.221 StartZ=0 EndX=226.072 EndY=124.221 EndZ=0
    g377: LineSegment StartX=232.072 StartY=124.221 StartZ=0 EndX=232.072 EndY=127.221 EndZ=0
    g378: LineSegment StartX=232.072 StartY=136.221 StartZ=0 EndX=232.072 EndY=133.221 EndZ=0
    g379-g383: Circle x5 (B-spline internal-alignment scaffolding for g384; pole/knot coordinates omitted)
    g384: BSplineCurve PolesCount=5 KnotsCount=3 Degree=3 IsPeriodic=0
    g385: GeomPoint X=232.072 Y=133.221 Z=0
    g386: GeomPoint X=223.072 Y=130.221 Z=0
    g387: GeomPoint X=232.072 Y=127.221 Z=0
    g388: LineSegment StartX=189.124 StartY=124.221 StartZ=0 EndX=302.073 EndY=124.221 EndZ=0
    g389: LineSegment StartX=132.072 StartY=136.221 StartZ=0 EndX=132.072 EndY=124.221 EndZ=0
    g390: LineSegment StartX=132.072 StartY=136.221 StartZ=0 EndX=144.072 EndY=136.221 EndZ=0
    g391: LineSegment StartX=144.072 StartY=136.221 StartZ=0 EndX=144.072 EndY=124.221 EndZ=0
    g392: LineSegment StartX=144.072 StartY=136.221 StartZ=0 EndX=138.072 EndY=136.221 EndZ=0
    g393: LineSegment StartX=144.072 StartY=136.221 StartZ=0 EndX=144.072 EndY=130.221 EndZ=0
    g394: LineSegment StartX=132.072 StartY=136.221 StartZ=0 EndX=132.072 EndY=133.221 EndZ=0
    g395: LineSegment StartX=132.072 StartY=133.221 StartZ=0 EndX=132.072 EndY=127.221 EndZ=0
    g396-g400: Circle x5 (B-spline internal-alignment scaffolding for g401; pole/knot coordinates omitted)
    g401: BSplineCurve PolesCount=5 KnotsCount=3 Degree=3 IsPeriodic=0
    g402: GeomPoint X=132.072 Y=133.221 Z=0
    g403: GeomPoint X=141.072 Y=130.221 Z=0
    g404: GeomPoint X=132.072 Y=127.221 Z=0
    g405: LineSegment StartX=132.072 StartY=124.221 StartZ=0 EndX=175.022 EndY=124.221 EndZ=0
    g406: LineSegment StartX=62.0728 StartY=124.221 StartZ=0 EndX=132.072 EndY=124.221 EndZ=0
    g407: LineSegment StartX=132.072 StartY=136.221 StartZ=0 EndX=131.457 EndY=138.832 EndZ=0
    ... +61 more geometry lines
  constraints (808):
    c: Vertical(g0)
    c: Vertical(g1)
    c: Block(g1)
    c: Block(g0)
    c: Weight(g4) = 1
    c: Equal(g4,g5)
    c: Equal(g4,g6)
    c: InternalAlignment(g4,g7)
    c: InternalAlignment(g5,g7)
    c: InternalAlignment(g6,g7)
    c: InternalAlignment(g8,g7)
    c: InternalAlignment(g9,g7)
    c: Weight(g10) = 1
    c: Equal(g10,g11)
    c: Equal(g10,g12)
    c: InternalAlignment(g10,g13)
    c: InternalAlignment(g11,g13)
    c: InternalAlignment(g12,g13)
    c: InternalAlignment(g14,g13)
    c: InternalAlignment(g15,g13)
    c: Block(g13)
    c: Block(g7)
    c: Weight(g16) = 1
    c: Equal(g16,g17)
    c: Equal(g16,g18)
    c: InternalAlignment(g16,g19)
    c: InternalAlignment(g17,g19)
    c: InternalAlignment(g18,g19)
    c: InternalAlignment(g20,g19)
    c: InternalAlignment(g21,g19)
    c: Weight(g22) = 1
    c: Equal(g22,g23)
    c: Equal(g22,g24)
    c: InternalAlignment(g22,g25)
    c: InternalAlignment(g23,g25)
    c: InternalAlignment(g24,g25)
    c: InternalAlignment(g26,g25)
    c: InternalAlignment(g27,g25)
    c: Block(g25)
    c: Block(g19)
    c: Weight(g28) = 1
    c: Equal(g28,g29)
    c: Equal(g28,g30)
    c: InternalAlignment(g28,g31)
    c: InternalAlignment(g29,g31)
    c: InternalAlignment(g30,g31)
    c: InternalAlignment(g32,g31)
    c: InternalAlignment(g33,g31)
    c: Weight(g34) = 1
    c: Equal(g34,g35)
    c: Equal(g34,g36)
    c: InternalAlignment(g34,g37)
    c: InternalAlignment(g35,g37)
    c: InternalAlignment(g36,g37)
    c: InternalAlignment(g38,g37)
    c: InternalAlignment(g39,g37)
    c: Block(g31)
    c: Block(g37)
    c: Coincident(g40,g1)
    c: Coincident(g40,g0)
    c: Horizontal(g40)
    c: Distance(g40) = 450
    c: Weight(g41) = 1
    c: Equal(g41,g42)
    c: Equal(g41,g43)
    c: InternalAlignment(g41,g44)
    c: InternalAlignment(g42,g44)
    c: InternalAlignment(g43,g44)
    c: InternalAlignment(g45,g44)
    c: InternalAlignment(g46,g44)
    c: Block(g44)
    c: Weight(g47) = 1
    c: Equal(g47,g48)
    c: Equal(g47,g49)
    c: InternalAlignment(g47,g50)
    c: InternalAlignment(g48,g50)
    c: InternalAlignment(g49,g50)
    c: InternalAlignment(g51,g50)
    c: InternalAlignment(g52,g50)
    c: Block(g50)
    c: Weight(g53) = 1
    c: Equal(g53,g54)
    c: Equal(g53,g55)
    c: InternalAlignment(g53,g56)
    c: InternalAlignment(g54,g56)
    c: InternalAlignment(g55,g56)
    c: InternalAlignment(g57,g56)
    c: InternalAlignment(g58,g56)
    c: Block(g56)
    c: Weight(g59) = 1
    c: Equal(g59,g60)
    c: Equal(g59,g61)
    c: InternalAlignment(g59,g62)
    c: InternalAlignment(g60,g62)
    c: InternalAlignment(g61,g62)
    c: InternalAlignment(g63,g62)
    c: InternalAlignment(g64,g62)
    c: Block(g62)
    c: Weight(g65) = 1
    c: Equal(g65,g66)
    c: Equal(g65,g67)
    c: InternalAlignment(g65,g68)
    c: InternalAlignment(g66,g68)
    c: InternalAlignment(g67,g68)
    c: InternalAlignment(g69,g68)
    c: InternalAlignment(g70,g68)
    c: Weight(g71) = 1
    c: Equal(g71,g72)
    c: Equal(g71,g73)
    c: InternalAlignment(g71,g74)
    c: InternalAlignment(g72,g74)
    c: InternalAlignment(g73,g74)
    c: InternalAlignment(g75,g74)
    c: InternalAlignment(g76,g74)
    c: Block(g68)
    c: Block(g74)
    c: Coincident(g77,g68)
    c: Coincident(g77,g74)
    c: Vertical(g77)
    c: Coincident(g78,g68)
    c: Coincident(g78,g50)
    c: Coincident(g79,g50)
    c: Coincident(g79,g74)
    c: Weight(g80) = 1
    c: Equal(g80,g81)
    c: Equal(g80,g82)
    c: InternalAlignment(g80,g83)
    c: InternalAlignment(g81,g83)
    c: InternalAlignment(g82,g83)
    c: InternalAlignment(g84,g83)
    c: InternalAlignment(g85,g83)
    c: Weight(g86) = 1
    c: Equal(g86,g87)
    c: Equal(g86,g88)
    c: InternalAlignment(g86,g89)
    c: InternalAlignment(g87,g89)
    c: InternalAlignment(g88,g89)
    c: InternalAlignment(g90,g89)
    c: InternalAlignment(g91,g89)
    c: Block(g83)
    c: Block(g89)
    c: Coincident(g92,g83)
    c: Coincident(g92,g89)
    c: Vertical(g92)
    c: Coincident(g93,g83)
    c: Coincident(g93,g44)
    c: Coincident(g94,g44)
    c: Coincident(g94,g89)
    c: Weight(g95) = 1
    c: Equal(g95,g96)
    c: Equal(g95,g97)
    c: InternalAlignment(g95,g98)
    c: InternalAlignment(g96,g98)
    c: InternalAlignment(g97,g98)
    c: InternalAlignment(g99,g98)
    c: InternalAlignment(g100,g98)
    c: Weight(g101) = 1
    c: Equal(g101,g102)
    c: Equal(g101,g103)
    c: InternalAlignment(g101,g104)
    c: InternalAlignment(g102,g104)
    c: InternalAlignment(g103,g104)
    c: InternalAlignment(g105,g104)
    c: InternalAlignment(g106,g104)
    c: Block(g98)
    c: Block(g104)
    c: Coincident(g107,g98)
    c: Coincident(g107,g104)
    c: Vertical(g107)
    c: Coincident(g108,g104)
    c: Coincident(g108,g62)
    c: Coincident(g109,g62)
    c: Coincident(g109,g98)
    c: Weight(g110) = 1
    c: Equal(g110,g111)
    c: Equal(g110,g112)
    c: InternalAlignment(g110,g113)
    c: InternalAlignment(g111,g113)
    c: InternalAlignment(g112,g113)
    c: InternalAlignment(g114,g113)
    c: InternalAlignment(g115,g113)
    c: Weight(g116) = 1
    c: Equal(g116,g117)
    c: Equal(g116,g118)
    c: InternalAlignment(g116,g119)
    c: InternalAlignment(g117,g119)
    c: InternalAlignment(g118,g119)
    c: InternalAlignment(g120,g119)
    c: InternalAlignment(g121,g119)
    c: Block(g113)
    c: Block(g119)
    c: Coincident(g122,g113)
    c: Coincident(g122,g119)
    c: Vertical(g122)
    c: Coincident(g123,g119)
    c: Coincident(g123,g56)
    c: Coincident(g124,g56)
    c: Coincident(g124,g113)
    c: Weight(g125) = 1
    c: Equal(g125,g126)
    c: Equal(g125,g127)
    c: InternalAlignment(g125,g128)
    c: InternalAlignment(g126,g128)
    c: InternalAlignment(g127,g128)
    c: InternalAlignment(g129,g128)
    c: InternalAlignment(g130,g128)
    c: Weight(g131) = 1
    c: Equal(g131,g132)
    c: Equal(g131,g133)
    c: InternalAlignment(g131,g134)
    c: InternalAlignment(g132,g134)
    c: InternalAlignment(g133,g134)
    c: InternalAlignment(g135,g134)
    c: InternalAlignment(g136,g134)
    c: Weight(g137) = 1
    c: Equal(g137,g138)
    c: Equal(g137,g139)
    c: InternalAlignment(g137,g140)
    c: InternalAlignment(g138,g140)
    c: InternalAlignment(g139,g140)
    c: InternalAlignment(g141,g140)
    c: InternalAlignment(g142,g140)
    c: Weight(g143) = 1
    c: Equal(g143,g144)
    c: Equal(g143,g145)
    c: InternalAlignment(g143,g146)
    c: InternalAlignment(g144,g146)
    c: InternalAlignment(g145,g146)
    c: InternalAlignment(g147,g146)
    c: InternalAlignment(g148,g146)
    c: Block(g146)
    c: Block(g140)
    c: Block(g134)
    c: Block(g128)
    c: Coincident(g149,g25)
    c: Coincident(g149,g146)
    c: Coincident(g150,g146)
    c: Coincident(g150,g140)
    c: Horizontal(g150)
    c: Coincident(g151,g140)
    c: Coincident(g151,g25)
    c: Vertical(g151)
    c: Coincident(g152,g19)
    c: Coincident(g152,g134)
    c: Vertical(g152)
    c: Coincident(g153,g134)
    c: Coincident(g153,g128)
    c: Horizontal(g153)
    c: Coincident(g154,g128)
    c: Coincident(g154,g19)
    c: Weight(g155) = 1
    c: Equal(g155,g156)
    c: Equal(g155,g157)
    c: InternalAlignment(g155,g158)
    c: InternalAlignment(g156,g158)
    c: InternalAlignment(g157,g158)
    c: InternalAlignment(g159,g158)
    c: InternalAlignment(g160,g158)
    c: Weight(g161) = 1
    c: Equal(g161,g162)
    c: Equal(g161,g163)
    c: InternalAlignment(g161,g164)
    c: InternalAlignment(g162,g164)
    c: InternalAlignment(g163,g164)
    c: InternalAlignment(g165,g164)
    c: InternalAlignment(g166,g164)
    c: Weight(g167) = 1
    c: Equal(g167,g168)
    c: Equal(g167,g169)
    c: InternalAlignment(g167,g170)
    c: InternalAlignment(g168,g170)
    c: InternalAlignment(g169,g170)
    c: InternalAlignment(g171,g170)
    c: InternalAlignment(g172,g170)
    c: Weight(g173) = 1
    c: Equal(g173,g174)
    c: Equal(g173,g175)
    c: InternalAlignment(g173,g176)
    c: InternalAlignment(g174,g176)
    c: InternalAlignment(g175,g176)
    c: InternalAlignment(g177,g176)
    c: InternalAlignment(g178,g176)
    c: Block(g176)
    c: Block(g170)
    c: Block(g164)
    c: Block(g158)
    c: Coincident(g179,g170)
    c: Coincident(g179,g7)
    c: Vertical(g179)
    c: Coincident(g180,g13)
    c: Coincident(g180,g164)
    c: Vertical(g180)
    c: Coincident(g181,g158)
    c: Coincident(g181,g13)
    c: Coincident(g182,g7)
    c: Weight(g183) = 1
    c: Equal(g183,g184)
    c: Equal(g183,g185)
    c: InternalAlignment(g183,g186)
    c: InternalAlignment(g184,g186)
    c: InternalAlignment(g185,g186)
    c: InternalAlignment(g187,g186)
    c: InternalAlignment(g188,g186)
    c: Weight(g189) = 1
    c: Equal(g189,g190)
    c: Equal(g189,g191)
    c: InternalAlignment(g189,g192)
    c: InternalAlignment(g190,g192)
    c: InternalAlignment(g191,g192)
    c: InternalAlignment(g193,g192)
    c: InternalAlignment(g194,g192)
    c: Block(g192)
    c: Block(g186)
    c: Coincident(g195,g192)
    c: Coincident(g195,g31)
    c: Coincident(g196,g31)
    c: Coincident(g196,g186)
    c: Coincident(g197,g186)
    c: Coincident(g197,g192)
    c: Vertical(g197)
    c: Weight(g198) = 1
    c: Equal(g198,g199)
    c: Equal(g198,g200)
    c: InternalAlignment(g198,g201)
    c: InternalAlignment(g199,g201)
    c: InternalAlignment(g200,g201)
    c: InternalAlignment(g202,g201)
    c: InternalAlignment(g203,g201)
    c: Weight(g204) = 1
    c: Equal(g204,g205)
    c: Equal(g204,g206)
    c: InternalAlignment(g204,g207)
    c: InternalAlignment(g205,g207)
    c: InternalAlignment(g206,g207)
    c: InternalAlignment(g208,g207)
    c: InternalAlignment(g209,g207)
    c: Block(g207)
    c: Block(g201)
    c: Coincident(g210,g201)
    c: Coincident(g210,g37)
    c: Coincident(g211,g37)
    c: Coincident(g211,g207)
    c: Coincident(g212,g207)
    c: Coincident(g212,g201)
    c: Vertical(g212)
    c: Horizontal(g213)
    c: Block(g213)
    c: Vertical(g214)
    c: Block(g214)
    c: Block(g215)
    c: Weight(g216) = 1
    c: Equal(g216,g217)
    c: Equal(g216,g218)
    c: InternalAlignment(g216,g219)
    c: InternalAlignment(g217,g219)
    c: InternalAlignment(g218,g219)
    c: InternalAlignment(g220,g219)
    c: InternalAlignment(g221,g219)
    c: Weight(g222) = 1
    c: Equal(g222,g223)
    c: Equal(g222,g224)
    c: InternalAlignment(g222,g225)
    c: InternalAlignment(g223,g225)
    c: InternalAlignment(g224,g225)
    c: InternalAlignment(g226,g225)
    c: InternalAlignment(g227,g225)
    c: Weight(g228) = 1
    c: Equal(g228,g229)
    c: Equal(g228,g230)
    c: InternalAlignment(g228,g231)
    c: InternalAlignment(g229,g231)
    c: InternalAlignment(g230,g231)
    c: InternalAlignment(g232,g231)
    c: InternalAlignment(g233,g231)
    c: Weight(g234) = 1
    c: Equal(g234,g235)
    c: Equal(g234,g236)
    c: InternalAlignment(g234,g237)
    c: InternalAlignment(g235,g237)
    c: InternalAlignment(g236,g237)
    c: InternalAlignment(g238,g237)
    c: InternalAlignment(g239,g237)
    c: Block(g219)
    c: Block(g225)
    c: Block(g231)
    c: Block(g237)
    c: Coincident(g240,g225)
    c: Coincident(g240,g219)
    c: Horizontal(g240)
    c: Block(g182)
    c: Weight(g241) = 1
    c: Equal(g241,g242)
    c: Equal(g241,g243)
    c: InternalAlignment(g241,g244)
    c: InternalAlignment(g242,g244)
    c: InternalAlignment(g243,g244)
    c: InternalAlignment(g245,g244)
    c: InternalAlignment(g246,g244)
    c: Weight(g247) = 1
    c: Equal(g247,g248)
    c: Equal(g247,g249)
    c: InternalAlignment(g247,g250)
    c: InternalAlignment(g248,g250)
    c: InternalAlignment(g249,g250)
    c: InternalAlignment(g251,g250)
    c: InternalAlignment(g252,g250)
    c: Block(g244)
    c: Block(g250)
    c: Coincident(g253,g244)
    c: Coincident(g253,g250)
    c: Weight(g254) = 1
    c: Equal(g254,g255)
    c: Equal(g254,g256)
    c: InternalAlignment(g254,g257)
    c: InternalAlignment(g255,g257)
    c: InternalAlignment(g256,g257)
    c: InternalAlignment(g258,g257)
    c: InternalAlignment(g259,g257)
    c: Weight(g260) = 1
    c: Equal(g260,g261)
    c: Equal(g260,g262)
    c: InternalAlignment(g260,g263)
    c: InternalAlignment(g261,g263)
    c: InternalAlignment(g262,g263)
    c: InternalAlignment(g264,g263)
    c: InternalAlignment(g265,g263)
    c: Weight(g266) = 1
    c: Equal(g266,g267)
    c: Equal(g266,g268)
    c: InternalAlignment(g266,g269)
    c: InternalAlignment(g267,g269)
    c: InternalAlignment(g268,g269)
    c: InternalAlignment(g270,g269)
    c: InternalAlignment(g271,g269)
    c: Block(g269)
    c: Block(g263)
    c: Block(g257)
    c: Coincident(g272,g263)
    c: Coincident(g272,g257)
    c: Coincident(g273,g257)
    c: Coincident(g273,g269)
    c: Vertical(g273)
    c: Coincident(g274,g269)
    c: Coincident(g274,g263)
    c: Horizontal(g274)
    c: Weight(g275) = 1
    c: Equal(g275,g276)
    c: InternalAlignment(g275,g277)
    c: InternalAlignment(g276,g277)
    c: InternalAlignment(g278,g277)
    c: InternalAlignment(g279,g277)
    c: Weight(g280) = 1
    c: InternalAlignment(g281,g283)
    c: InternalAlignment(g282,g283)
    c: InternalAlignment(g284,g283)
    c: InternalAlignment(g285,g283)
    c: Weight(g286) = 1
    c: Equal(g286,g287)
    c: Equal(g286,g288)
    c: InternalAlignment(g286,g289)
    c: InternalAlignment(g287,g289)
    c: InternalAlignment(g288,g289)
    c: InternalAlignment(g290,g289)
    c: InternalAlignment(g291,g289)
    c: Equal(g292,g293)
    c: Equal(g292,g294)
    c: InternalAlignment(g292,g295)
    c: InternalAlignment(g293,g295)
    c: InternalAlignment(g294,g295)
    c: InternalAlignment(g296,g295)
    c: InternalAlignment(g297,g295)
    c: Block(g283)
    c: Block(g289)
    c: Block(g295)
    c: Block(g277)
    c: Coincident(g298,g277)
    c: Coincident(g298,g283)
    c: Horizontal(g298)
    c: Coincident(g299,g283)
    c: Coincident(g299,g289)
    c: Vertical(g299)
    c: Coincident(g300,g289)
    c: Coincident(g300,g295)
    c: Horizontal(g300)
    c: Coincident(g301,g295)
    c: Coincident(g301,g277)
    c: Weight(g302) = 1
    c: Equal(g302,g303)
    c: Equal(g302,g304)
    c: InternalAlignment(g302,g305)
    c: InternalAlignment(g303,g305)
    c: InternalAlignment(g304,g305)
    c: InternalAlignment(g306,g305)
    c: InternalAlignment(g307,g305)
    c: Weight(g308) = 1
    c: Equal(g308,g309)
    c: Equal(g308,g310)
    c: InternalAlignment(g308,g311)
    c: InternalAlignment(g309,g311)
    c: InternalAlignment(g310,g311)
    c: InternalAlignment(g312,g311)
    c: Weight(g314) = 1
    c: Equal(g314,g315)
    c: Equal(g314,g316)
    c: InternalAlignment(g314,g317)
    c: InternalAlignment(g315,g317)
    c: InternalAlignment(g316,g317)
    c: InternalAlignment(g318,g317)
    c: InternalAlignment(g319,g317)
    c: Block(g317)
    c: Block(g311)
    c: Block(g305)
    c: Coincident(g320,g317)
    c: Coincident(g320,g311)
    c: Horizontal(g320)
    c: Coincident(g321,g311)
    c: Coincident(g321,g305)
    c: Vertical(g321)
    c: Coincident(g322,g305)
    c: Coincident(g322,g317)
    c: InternalAlignment(g323,g324)
    c: InternalAlignment(g325,g324)
    c: InternalAlignment(g326,g324)
    c: Block(g324)
    c: Equal(g327,g328)
    c: Equal(g327,g329)
    c: InternalAlignment(g327,g330)
    c: InternalAlignment(g328,g330)
    c: InternalAlignment(g329,g330)
    c: InternalAlignment(g331,g330)
    c: InternalAlignment(g332,g330)
    c: Block(g330)
    c: Coincident(g333,g324)
    c: Horizontal(g333)
    c: Block(g333)
    c: Coincident(g334,g324)
    c: Coincident(g334,g250)
    c: Vertical(g334)
    c: Coincident(g335,g330)
    c: Coincident(g335,g244)
    c: Vertical(g335)
    c: Block(g336)
    c: Block(g2)
    c: Distance(g334) = 119.89
    c: Coincident(g337,g336)
    c: Coincident(g337,g2)
    c: Coincident(g338,g2)
    c: Coincident(g338,g336)
    c: Block(g3)
    c: Block(g339)
    c: Coincident(g340,g339)
    c: Coincident(g340,g3)
    c: Coincident(g341,g339)
    c: Coincident(g341,g3)
    c: Block(g341)
    c: Block(g340)
    c: Weight(g342) = 1
    c: Equal(g342,g344)
    c: InternalAlignment(g342,g345)
    c: InternalAlignment(g343,g345)
    c: InternalAlignment(g344,g345)
    c: InternalAlignment(g346,g345)
    c: InternalAlignment(g347,g345)
    c: InternalAlignment(g352,g351)
    c: InternalAlignment(g353,g351)
    c: InternalAlignment(g355,g357)
    c: Horizontal(g369)
    c: Coincident(g370,g0)
    c: Horizontal(g370)
    c: Block(g370)
    c: Distance(g370) = 450
    c: Horizontal(g371)
    c: Distance(g371) = 12
    c: Coincident(g373,g371)
    c: Vertical(g373)
    c: Horizontal(g374)
    c: Vertical(g375)
    c: Distance(g375) = 6
    c: Coincident(g375,g371)
    c: Coincident(g374,g371)
    c: Block(g373)
    c: Coincident(g376,g373)
    c: Horizontal(g376)
    c: Distance(g376) = 6
    c: Vertical(g377)
    c: Distance(g377) = 3
    c: Vertical(g378)
    c: Distance(g378) = 3
    c: Coincident(g372,g377)
    c: Coincident(g384,g378)
    c: Weight(g379) = 1
    c: Equal(g379,g380)
    c: Coincident(g380,g374)
    c: Equal(g379,g381)
    c: Coincident(g381,g375)
    c: Equal(g379,g382)
    c: Coincident(g382,g376)
    c: Equal(g379,g383)
    c: Coincident(g384,g377)
    c: InternalAlignment(g379-g383 -> g384) x5
    c: InternalAlignment(g385,g384)
    c: InternalAlignment(g386,g384)
    c: InternalAlignment(g387,g384)
    c: Coincident(g388,g164)
    c: Coincident(g388,g158)
    c: Coincident(g392,g390)
    c: Vertical(g393)
    c: Distance(g393) = 6
    c: Coincident(g393,g390)
    c: Vertical(g394)
    c: Distance(g394) = 3
    c: Vertical(g395)
    c: Distance(g395) = 6
    c: Coincident(g395,g394)
    c: Coincident(g401,g394)
    c: Weight(g396) = 1
    c: Equal(g396,g397)
    c: Coincident(g397,g392)
    c: Equal(g396,g398)
    c: Coincident(g398,g393)
    c: Equal(g396,g399)
    c: Equal(g396,g400)
    c: Coincident(g401,g395)
    c: InternalAlignment(g396-g400 -> g401) x5
    c: InternalAlignment(g402,g401)
    c: InternalAlignment(g403,g401)
    c: InternalAlignment(g404,g401)
    c: Coincident(g405,g389)
    c: Coincident(g405,g170)
    c: Horizontal(g405)
    c: Block(g401)
    c: Coincident(g406,g176)
    c: Coincident(g406,g389)
    c: Horizontal(g406)
    c: Block(g405)
    c: Coincident(g408,g389)
    c: PointOnObject(g408,g153)
    c: Vertical(g408)
    c: Block(g409)
    c: Coincident(g410,g409)
    c: Vertical(g410)
    c: PointOnObject(g410,g40)
    c: Block(g410)
    c: Coincident(g411,g409)
    c: Vertical(g411)
    c: Block(g411)
    c: Vertical(g412)
    c: Distance(g412) = 3
    c: Equal(g379,g415) = 1
    c: Equal(g415,g416)
    c: InternalAlignment(g415,g417)
    c: InternalAlignment(g416,g417)
    c: InternalAlignment(g413,g417)
    c: InternalAlignment(g414,g417)
    c: InternalAlignment(g418,g417)
    c: Block(g417)
    c: Coincident(g418,g412)
    c: Coincident(g419,g417)
    c: PointOnObject(g419,g150)
    c: Vertical(g419)
    c: Distance(g420) = 3
    c: Block(g420)
    c: Distance(g421) = 3
    c: Parallel(g421,g420)
    c: Coincident(g421,g420)
    c: Coincident(g422,g420)
    c: Perpendicular(g422,g420)
    c: Distance(g422) = 3
    c: Coincident(g423,g421)
    c: Perpendicular(g423,g421)
    c: Distance(g423) = 3
    c: Coincident(g424,g420)
    c: Perpendicular(g424,g421)
    c: Distance(g424) = 6
    c: Coincident(g425,g424)
    c: PointOnObject(g423,g425)
    c: Coincident(g426,g420)
    c: PointOnObject(g426,g79)
    c: Block(g426)
    c: Distance(g427) = 2.76
    c: Coincident(g428,g427)
    c: Parallel(g427,g428)
    c: PointOnObject(g428,g181)
    c: Distance(g428) = 2.41
    c: Block(g428)
    c: Coincident(g429,g427)
    c: Distance(g429) = 6.6
    c: Perpendicular(g429,g428)
    c: Distance(g430) = 6.6
    c: Coincident(g431,g429)
    c: Coincident(g431,g430)
    c: Block(g432)
    c: Coincident(g433,g432)
    c: Vertical(g433)
    c: Distance(g433) = 3.6
    c: Coincident(g434,g427)
    c: Parallel(g427,g434)
    c: PointOnObject(g434,g78)
    c: Block(g434)
    c: Coincident(g435,g421)
    c: Parallel(g435,g421)
    c: PointOnObject(g435,g211)
    c: Block(g435)
    c: Coincident(g436,g435)
    c: Vertical(g436)
    c: PointOnObject(g436,g210)
    c: Coincident(g437,g436)
    c: Perpendicular(g437,g210)
    c: Distance(g437) = 3
    c: Coincident(g438,g437)
    c: Block(g437)
    c: Distance(g438) = 3
    c: Parallel(g437,g438)
    c: Coincident(g439,g438)
    c: Distance(g439) = 3
    c: Parallel(g438,g439)
    c: Coincident(g440,g439)
    c: Parallel(g440,g437)
    c: PointOnObject(g440,g124)
    c: PointOnObject(g441,g53)
    c: Tangent(g440,g441)
    c: Coincident(g442,g439)
    c: Perpendicular(g442,g439)
    c: Coincident(g443,g437)
    c: Parallel(g443,g442)
    c: Distance(g443) = 3
    c: Distance(g442) = 3
    c: PointOnObject(g442,g444)
    c: Block(g444)
    c: PointOnObject(g445,g123)
    c: Perpendicular(g123,g445)
    c: Distance(g445) = 2.41
    c: Block(g445)
    c: Coincident(g446,g445)
    c: Perpendicular(g123,g446)
    c: Distance(g446) = 2.76
    c: Coincident(g447,g446)
    c: Perpendicular(g123,g447)
    c: PointOnObject(g447,g149)
    c: Coincident(g448,g445)
    c: Parallel(g123,g448)
    c: Distance(g448) = 6.6
    c: Coincident(g449,g446)
    c: Parallel(g123,g449)
    c: Coincident(g450,g448)
    c: Distance(g449) = 6.6
    c: Coincident(g449,g450)
    c: Block(g149)
    c: Block(g124)
    c: Block(g211)
    c: Block(g181)
    c: Block(g78)
    c: Block(g79)
    c: Block(g430)
    c: Coincident(g451,g447)
    c: Distance(g451) = 46
    c: Parallel(g149,g451)
    c: Coincident(g452,g451)
    c: Horizontal(g452)
    c: PointOnObject(g452,g154)
    c: Coincident(g453,g451)
    c: Vertical(g453)
    c: Distance(g453) = 9
    c: Block(g452)
    c: PointOnObject(g454,g93)
    c: Distance(g455) = 6.6
    c: Distance(g456) = 6.6
    c: Block(g454)
    c: Coincident(g457,g456)
    c: Coincident(g457,g455)
    c: Perpendicular(g457,g182)
    c: Coincident(g458,g455)
    c: Perpendicular(g458,g182)
    c: PointOnObject(g458,g182)
    c: Block(g458)
    c: Block(g457)
    c: Block(g456)
    c: PointOnObject(g459,g196)
    c: Perpendicular(g196,g459)
    c: Distance(g459) = 3
    c: Coincident(g460,g459)
    c: Perpendicular(g196,g460)
    c: Distance(g460) = 3
    c: Coincident(g461,g460)
    c: Perpendicular(g196,g461)
    c: Distance(g461) = 3
    c: Coincident(g462,g461)
    c: Tangent(g462,g41)
    c: PointOnObject(g462,g94)
    c: Block(g462)
    c: Block(g459)
    c: Coincident(g463,g459)
    c: Parallel(g196,g463)
    c: Distance(g463) = 3
    c: Coincident(g464,g461)
    c: Distance(g464) = 3
    c: Parallel(g196,g464)
    c: Coincident(g465,g460)
    c: Distance(g465) = 6
    c: Parallel(g465,g196)
    c: Coincident(g466,g465)
    c: PointOnObject(g464,g466)
    c: Block(g466)
    c: Coincident(g467,g458)
    c: Vertical(g467)
    c: PointOnObject(g467,g195)
    c: Coincident(g468,g467)
    c: Perpendicular(g195,g468)
FEATURE [Sketcher::SketchObject] Sketch004  label="rightSideBottom"
  FullyConstrained = false
  sketch-geometry (91):
    g0: ArcOfCircle CenterX=391.073 CenterY=-83.7794 CenterZ=0 NormalX=0 NormalY=0 NormalZ=1 AngleXU=0 Radius=8 StartAngle=3.14159 EndAngle=6.28319
    g1: Circle CenterX=306.073 CenterY=-81.8102 CenterZ=0 NormalX=0 NormalY=0 NormalZ=1 AngleXU=0 Radius=1
    g2: Circle CenterX=306.073 CenterY=-77.8102 CenterZ=0 NormalX=0 NormalY=0 NormalZ=1 AngleXU=0 Radius=1
    g3: Circle CenterX=302.567 CenterY=-42.9683 CenterZ=0 NormalX=0 NormalY=0 NormalZ=1 AngleXU=0 Radius=1
    g4: Circle CenterX=306.073 CenterY=-44.8935 CenterZ=0 NormalX=0 NormalY=0 NormalZ=1 AngleXU=0 Radius=1
    g5: Circle CenterX=306.073 CenterY=-40.8935 CenterZ=0 NormalX=0 NormalY=0 NormalZ=1 AngleXU=0 Radius=1
    g6: BSplineCurve PolesCount=3 KnotsCount=2 Degree=2 IsPeriodic=0
    g7: GeomPoint X=302.567 Y=-42.9683 Z=0
    g8: GeomPoint X=306.073 Y=-40.8935 Z=0
    g9: Circle CenterX=371.567 CenterY=-80.8644 CenterZ=0 NormalX=0 NormalY=0 NormalZ=1 AngleXU=0 Radius=1
    g10: Circle CenterX=375.073 CenterY=-82.7896 CenterZ=0 NormalX=0 NormalY=0 NormalZ=1 AngleXU=0 Radius=1
    g11: Circle CenterX=375.073 CenterY=-78.7896 CenterZ=0 NormalX=0 NormalY=0 NormalZ=1 AngleXU=0 Radius=1
    g12: GeomPoint X=371.567 Y=-80.8644 Z=0
    g13: GeomPoint X=375.073 Y=-78.7896 Z=0
    g14: Circle CenterX=318.073 CenterY=-51.4823 CenterZ=0 NormalX=0 NormalY=0 NormalZ=1 AngleXU=0 Radius=1
    g15: Circle CenterX=318.073 CenterY=-47.4805 CenterZ=0 NormalX=0 NormalY=0 NormalZ=1 AngleXU=0 Radius=1
    g16: GeomPoint X=321.579 Y=-53.4075 Z=0
    g17: GeomPoint X=318.073 Y=-47.4805 Z=0
    g18: Circle CenterX=321.579 CenterY=-67.3492 CenterZ=0 NormalX=0 NormalY=0 NormalZ=1 AngleXU=0 Radius=1
    g19: Circle CenterX=318.073 CenterY=-65.424 CenterZ=0 NormalX=0 NormalY=0 NormalZ=1 AngleXU=0 Radius=1
    g20: Circle CenterX=318.073 CenterY=-69.424 CenterZ=0 NormalX=0 NormalY=0 NormalZ=1 AngleXU=0 Radius=1
    g21: GeomPoint X=321.579 Y=-67.3492 Z=0
    g22: GeomPoint X=318.073 Y=-69.424 Z=0
    g23: Circle CenterX=362.567 CenterY=-89.8542 CenterZ=0 NormalX=0 NormalY=0 NormalZ=1 AngleXU=0 Radius=1
    g24: Circle CenterX=366.073 CenterY=-91.7794 CenterZ=0 NormalX=0 NormalY=0 NormalZ=1 AngleXU=0 Radius=1
    g25: Circle CenterX=362.073 CenterY=-91.7794 CenterZ=0 NormalX=0 NormalY=0 NormalZ=1 AngleXU=0 Radius=1
    g26: GeomPoint X=362.567 Y=-89.8542 Z=0
    g27: GeomPoint X=362.073 Y=-91.7794 Z=0
    g28: Circle CenterX=322.073 CenterY=-91.7794 CenterZ=0 NormalX=0 NormalY=0 NormalZ=1 AngleXU=0 Radius=1
    g29: Circle CenterX=318.073 CenterY=-91.7794 CenterZ=0 NormalX=0 NormalY=0 NormalZ=1 AngleXU=0 Radius=1
    g30: Circle CenterX=318.073 CenterY=-87.7794 CenterZ=0 NormalX=0 NormalY=0 NormalZ=1 AngleXU=0 Radius=1
    g31: GeomPoint X=322.073 Y=-91.7794 Z=0
    g32: GeomPoint X=318.073 Y=-87.7794 Z=0
    g33: ArcOfCircle CenterX=391.073 CenterY=22.1087 CenterZ=0 NormalX=0 NormalY=0 NormalZ=1 AngleXU=0 Radius=4 StartAngle=0 EndAngle=3.14159
    g34: LineSegment StartX=387.073 StartY=22.1087 StartZ=0 EndX=383.073 EndY=-83.7794 EndZ=0
    g35: LineSegment StartX=395.073 StartY=22.1087 StartZ=0 EndX=399.073 EndY=-83.7794 EndZ=0
    g36: LineSegment StartX=232.072 StartY=-103.779 StartZ=0 EndX=232.072 EndY=-100.779 EndZ=0
    g37: GeomPoint X=232.072 Y=-94.7794 Z=0
    g38: GeomPoint X=223.072 Y=-97.7794 Z=0
    g39: Circle CenterX=232.072 CenterY=-94.7794 CenterZ=0 NormalX=0 NormalY=0 NormalZ=1 AngleXU=0 Radius=1
    g40: Circle CenterX=232.072 CenterY=-100.779 CenterZ=0 NormalX=0 NormalY=0 NormalZ=1 AngleXU=0 Radius=1
    g41: BSplineCurve PolesCount=5 KnotsCount=3 Degree=3 IsPeriodic=0
    g42: GeomPoint X=232.072 Y=-100.779 Z=0
    g43: LineSegment StartX=232.072 StartY=-94.7794 StartZ=0 EndX=232.072 EndY=-91.7794 EndZ=0
    g44: LineSegment StartX=245.072 StartY=-31.3037 StartZ=0 EndX=243.535 EndY=-33.1602 EndZ=0
    g45: LineSegment StartX=241.775 StartY=-35.2862 StartZ=0 EndX=240.266 EndY=-37.1092 EndZ=0
    g46: LineSegment StartX=243.535 StartY=-33.1602 StartZ=0 EndX=248.619 EndY=-37.3688 EndZ=0
    g47: LineSegment StartX=241.775 StartY=-35.2862 StartZ=0 EndX=246.859 EndY=-39.4949 EndZ=0
    g48: LineSegment StartX=248.619 StartY=-37.3688 StartZ=0 EndX=246.859 EndY=-39.4949 EndZ=0
    g49: LineSegment StartX=232.072 StartY=-103.779 StartZ=0 EndX=407.073 EndY=-103.779 EndZ=0
    g50: LineSegment StartX=299.888 StartY=-86.6413 StartZ=0 EndX=240.266 EndY=-37.1092 EndZ=0
    g51: LineSegment StartX=245.072 StartY=-11.4025 StartZ=0 EndX=302.567 EndY=-42.9683 EndZ=0
    g52: BSplineCurve PolesCount=3 KnotsCount=2 Degree=2 IsPeriodic=0
    g53: BSplineCurve PolesCount=3 KnotsCount=2 Degree=2 IsPeriodic=0
    g54: LineSegment StartX=321.579 StartY=-53.4075 StartZ=0 EndX=371.567 EndY=-80.8644 EndZ=0
    g55: BSplineCurve PolesCount=3 KnotsCount=2 Degree=2 IsPeriodic=0
    g56: BSplineCurve PolesCount=3 KnotsCount=2 Degree=2 IsPeriodic=0
    g57: BSplineCurve PolesCount=3 KnotsCount=2 Degree=2 IsPeriodic=0
    g58: LineSegment StartX=318.073 StartY=-69.424 StartZ=0 EndX=318.073 EndY=-87.7794 EndZ=0
    g59: LineSegment StartX=321.579 StartY=-67.3492 StartZ=0 EndX=362.567 EndY=-89.8542 EndZ=0
    g60: LineSegment StartX=362.073 StartY=-91.7794 StartZ=0 EndX=322.073 EndY=-91.7794 EndZ=0
    g61: BSplineCurve PolesCount=3 KnotsCount=2 Degree=2 IsPeriodic=0
    g62: BSplineCurve PolesCount=3 KnotsCount=2 Degree=2 IsPeriodic=0
    g63: LineSegment StartX=245.072 StartY=-31.3037 StartZ=0 EndX=302.996 EndY=-79.2541 EndZ=0
    g64: LineSegment StartX=302.567 StartY=-56.9099 StartZ=0 EndX=239.193 EndY=-22.1109 EndZ=0
    g65: LineSegment StartX=306.073 StartY=-62.8351 StartZ=0 EndX=306.073 EndY=-77.8102 EndZ=0
    g66: BSplineCurve PolesCount=3 KnotsCount=2 Degree=2 IsPeriodic=0
    g67: LineSegment StartX=298.776 StartY=-91.7794 StartZ=0 EndX=232.072 EndY=-91.7794 EndZ=0
    g68: LineSegment StartX=245.072 StartY=-11.4025 StartZ=0 EndX=243.628 EndY=-14.0323 EndZ=0
    g69: LineSegment StartX=240.741 StartY=-19.2917 StartZ=0 EndX=239.193 EndY=-22.1109 EndZ=0
    g70: LineSegment StartX=243.628 StartY=-14.0323 StartZ=0 EndX=246.258 EndY=-15.476 EndZ=0
    g71: LineSegment StartX=240.741 StartY=-19.2917 StartZ=0 EndX=243.37 EndY=-20.7355 EndZ=0
    g72: ArcOfCircle CenterX=247.444 CenterY=-19.5495 CenterZ=0 NormalX=0 NormalY=0 NormalZ=1 AngleXU=0 Radius=4.24264 StartAngle=3.4249 EndAngle=8.13729
    g73: LineSegment StartX=407.073 StartY=-103.779 StartZ=0 EndX=407.073 EndY=48.2206 EndZ=0
    g74: LineSegment StartX=375.073 StartY=48.2206 StartZ=0 EndX=375.073 EndY=-78.7896 EndZ=0
    g75: LineSegment StartX=375.073 StartY=48.2206 StartZ=0 EndX=382.073 EndY=48.2206 EndZ=0
    g76: LineSegment StartX=407.073 StartY=48.2206 StartZ=0 EndX=400.073 EndY=48.2206 EndZ=0
    g77: LineSegment StartX=394.073 StartY=48.2206 StartZ=0 EndX=394.073 EndY=52.2206 EndZ=0
    g78: LineSegment StartX=388.073 StartY=48.2206 StartZ=0 EndX=388.073 EndY=58.2206 EndZ=0
    g79: ArcOfCircle CenterX=385.073 CenterY=61.2206 CenterZ=0 NormalX=0 NormalY=0 NormalZ=1 AngleXU=0 Radius=4.24264 StartAngle=5.49779 EndAngle=10.2102
    g80: ArcOfCircle CenterX=397.073 CenterY=55.2206 CenterZ=0 NormalX=0 NormalY=0 NormalZ=1 AngleXU=0 Radius=4.24264 StartAngle=5.49779 EndAngle=10.2102
    g81: LineSegment StartX=382.073 StartY=58.2206 StartZ=0 EndX=382.073 EndY=48.2206 EndZ=0
    g82: LineSegment StartX=400.073 StartY=52.2206 StartZ=0 EndX=400.073 EndY=48.2206 EndZ=0
    g83: LineSegment StartX=394.073 StartY=48.2206 StartZ=0 EndX=388.073 EndY=48.2206 EndZ=0
    g84: LineSegment StartX=306.073 StartY=-40.8935 StartZ=0 EndX=306.073 EndY=-27.5935 EndZ=0
    g85: LineSegment StartX=318.073 StartY=-27.5935 StartZ=0 EndX=318.073 EndY=-47.4805 EndZ=0
    g86: LineSegment StartX=306.073 StartY=-27.5935 StartZ=0 EndX=310.073 EndY=-27.5935 EndZ=0
    g87: LineSegment StartX=318.073 StartY=-27.5935 StartZ=0 EndX=314.073 EndY=-27.5935 EndZ=0
    g88: LineSegment StartX=310.073 StartY=-27.5935 StartZ=0 EndX=310.073 EndY=-31.5935 EndZ=0
    g89: LineSegment StartX=314.073 StartY=-27.5935 StartZ=0 EndX=314.073 EndY=-31.5935 EndZ=0
    g90: ArcOfCircle CenterX=312.073 CenterY=-33.5935 CenterZ=0 NormalX=0 NormalY=0 NormalZ=1 AngleXU=0 Radius=2.82843 StartAngle=2.35619 EndAngle=7.06858
  constraints (121):
    c: Distance(g44) = 2.41
    c: Block(g44)
    c: Coincident(g46,g44)
    c: Coincident(g49,g36)
    c: Horizontal(g49)
    c: Block(g49)
    c: Coincident(g50,g45)
    c: Block(g50)
    c: Coincident(g51,g6)
    c: Block(g51)
    c: Coincident(g54,g52)
    c: Coincident(g54,g53)
    c: Coincident(g58,g56)
    c: Coincident(g58,g57)
    c: Vertical(g58)
    c: Coincident(g59,g56)
    c: Coincident(g59,g55)
    c: Coincident(g60,g55)
    c: Coincident(g60,g57)
    c: Horizontal(g60)
    c: Block(g61)
    c: Block(g62)
    c: Coincident(g63,g44)
    c: Coincident(g63,g62)
    c: Coincident(g64,g61)
    c: Coincident(g65,g61)
    c: Coincident(g65,g62)
    c: Vertical(g65)
    c: Block(g66)
    c: Coincident(g66,g50)
    c: Coincident(g67,g66)
    c: Coincident(g67,g43)
    c: Horizontal(g67)
    c: Coincident(g68,g51)
    c: Perpendicular(g68,g51)
    c: Coincident(g69,g64)
    c: Coincident(g70,g68)
    c: Distance(g70) = 3
    c: Distance(g71) = 3
    c: Perpendicular(g68,g70)
    c: Coincident(g72,g70)
    c: Coincident(g72,g71)
    c: Block(g72)
    c: Block(g69)
    c: Block(g71)
    c: Block(g54)
    c: Block(g59)
    c: Block(g58)
    c: Block(g60)
    c: Block(g67)
    c: Block(g43)
    c: Block(g36)
    c: Block(g48)
    c: Block(g46)
    c: Block(g47)
    c: Block(g45)
    c: Block(g35)
    c: Block(g34)
    c: Block(g0)
    c: Block(g33)
    c: Block(g52)
    c: Block(g6)
    c: Block(g41)
    c: Block(g57)
    c: Block(g55)
    c: Block(g53)
    c: Block(g68)
    c: Distance(g48) = 2.76
    c: Distance(g47) = 6.6
    c: Distance(g45) = 2.36657
    c: Coincident(g73,g49)
    c: Vertical(g73)
    c: Distance(g73) = 152
    c: Coincident(g74,g53)
    c: Vertical(g74)
    c: Block(g74)
    c: Coincident(g75,g74)
    c: Horizontal(g75)
    c: Distance(g75) = 7
    c: Horizontal(g76)
    c: Distance(g76) = 7
    c: Coincident(g76,g73)
    c: Vertical(g77)
    c: Distance(g77) = 4
    c: Vertical(g78)
    c: Distance(g78) = 10
    c: Coincident(g79,g78)
    c: Coincident(g80,g77)
    c: Block(g80)
    c: Block(g79)
    c: Coincident(g81,g79)
    c: Coincident(g81,g75)
    c: Vertical(g81)
    c: Coincident(g82,g80)
    c: Coincident(g82,g76)
    c: Vertical(g82)
    c: Coincident(g83,g77)
    c: Coincident(g83,g78)
    c: Horizontal(g83)
    c: Coincident(g84,g6)
    c: Vertical(g84)
    c: Distance(g84) = 13.3
    c: Coincident(g85,g52)
    c: Vertical(g85)
    c: Block(g85)
    c: Coincident(g86,g84)
    c: Horizontal(g86)
    c: Distance(g86) = 4
    c: Coincident(g87,g85)
    c: Horizontal(g87)
    c: Distance(g87) = 4
    c: Coincident(g88,g86)
    c: Vertical(g88)
    c: Coincident(g89,g87)
    c: Vertical(g89)
    c: Distance(g88) = 4
    c: Distance(g89) = 4
    c: Coincident(g90,g88)
    c: Coincident(g90,g89)
    c: Block(g90)
    c: Block(g56)
FEATURE [Sketcher::SketchObject] Sketch005  label="middleTop"
  FullyConstrained = true
  sketch-geometry (133):
    g0: Circle CenterX=175.025 CenterY=27.0667 CenterZ=0 NormalX=0 NormalY=0 NormalZ=1 AngleXU=0 Radius=1
    g1: Circle CenterX=179.022 CenterY=24.8665 CenterZ=0 NormalX=0 NormalY=0 NormalZ=1 AngleXU=0 Radius=1
    g2: Circle CenterX=179.022 CenterY=27.0606 CenterZ=0 NormalX=0 NormalY=0 NormalZ=1 AngleXU=0 Radius=1
    g3: BSplineCurve PolesCount=3 KnotsCount=2 Degree=2 IsPeriodic=0
    g4: GeomPoint X=175.025 Y=27.0667 Z=0
    g5: GeomPoint X=179.022 Y=27.0606 Z=0
    g6: Circle CenterX=189.124 CenterY=27.0628 CenterZ=0 NormalX=0 NormalY=0 NormalZ=1 AngleXU=0 Radius=1
    g7: Circle CenterX=185.124 CenterY=24.8665 CenterZ=0 NormalX=0 NormalY=0 NormalZ=1 AngleXU=0 Radius=1
    g8: Circle CenterX=185.124 CenterY=27.0606 CenterZ=0 NormalX=0 NormalY=0 NormalZ=1 AngleXU=0 Radius=1
    g9: BSplineCurve PolesCount=3 KnotsCount=2 Degree=2 IsPeriodic=0
    g10: GeomPoint X=189.124 Y=27.0628 Z=0
    g11: GeomPoint X=185.124 Y=27.0606 Z=0
    g12: Circle CenterX=165.871 CenterY=18.1458 CenterZ=0 NormalX=0 NormalY=0 NormalZ=1 AngleXU=0 Radius=1
    g13: Circle CenterX=169.377 CenterY=16.2206 CenterZ=0 NormalX=0 NormalY=0 NormalZ=1 AngleXU=0 Radius=1
    g14: Circle CenterX=165.871 CenterY=14.2956 CenterZ=0 NormalX=0 NormalY=0 NormalZ=1 AngleXU=0 Radius=1
    g15: BSplineCurve PolesCount=3 KnotsCount=2 Degree=2 IsPeriodic=0
    g16: GeomPoint X=165.871 Y=18.1458 Z=0
    g17: GeomPoint X=165.871 Y=14.2956 Z=0
    g18: Circle CenterX=198.275 CenterY=18.1318 CenterZ=0 NormalX=0 NormalY=0 NormalZ=1 AngleXU=0 Radius=1
    g19: Circle CenterX=194.768 CenterY=16.2206 CenterZ=0 NormalX=0 NormalY=0 NormalZ=1 AngleXU=0 Radius=1
    g20: Circle CenterX=198.264 CenterY=14.2963 CenterZ=0 NormalX=0 NormalY=0 NormalZ=1 AngleXU=0 Radius=1
    g21: BSplineCurve PolesCount=3 KnotsCount=2 Degree=2 IsPeriodic=0
    g22: GeomPoint X=198.275 Y=18.1318 Z=0
    g23: GeomPoint X=198.264 Y=14.2963 Z=0
    g24: Circle CenterX=125.607 CenterY=54.1951 CenterZ=0 NormalX=0 NormalY=0 NormalZ=1 AngleXU=0 Radius=1
    g25: Circle CenterX=139.632 CenterY=46.4944 CenterZ=0 NormalX=0 NormalY=0 NormalZ=1 AngleXU=0 Radius=1
    g26: Circle CenterX=127.326 CenterY=56.7187 CenterZ=0 NormalX=0 NormalY=0 NormalZ=1 AngleXU=0 Radius=1
    g27: BSplineCurve PolesCount=3 KnotsCount=2 Degree=2 IsPeriodic=0
    g28: GeomPoint X=125.607 Y=54.1951 Z=0
    g29: GeomPoint X=127.326 Y=56.7187 Z=0
    g30: Circle CenterX=236.824 CenterY=56.7187 CenterZ=0 NormalX=0 NormalY=0 NormalZ=1 AngleXU=0 Radius=1
    g31: Circle CenterX=224.513 CenterY=46.4944 CenterZ=0 NormalX=0 NormalY=0 NormalZ=1 AngleXU=0 Radius=1
    g32: Circle CenterX=238.538 CenterY=54.1951 CenterZ=0 NormalX=0 NormalY=0 NormalZ=1 AngleXU=0 Radius=1
    g33: BSplineCurve PolesCount=3 KnotsCount=2 Degree=2 IsPeriodic=0
    g34: GeomPoint X=236.824 Y=56.7187 Z=0
    g35: GeomPoint X=238.538 Y=54.1951 Z=0
    g36: Circle CenterX=189.121 CenterY=124.221 CenterZ=0 NormalX=0 NormalY=0 NormalZ=1 AngleXU=0 Radius=1
    g37: Circle CenterX=185.124 CenterY=124.221 CenterZ=0 NormalX=0 NormalY=0 NormalZ=1 AngleXU=0 Radius=1
    g38: Circle CenterX=185.124 CenterY=120.221 CenterZ=0 NormalX=0 NormalY=0 NormalZ=1 AngleXU=0 Radius=1
    g39: BSplineCurve PolesCount=3 KnotsCount=2 Degree=2 IsPeriodic=0
    g40: GeomPoint X=189.121 Y=124.221 Z=0
    g41: GeomPoint X=185.124 Y=120.221 Z=0
    g42: Circle CenterX=175.022 CenterY=124.221 CenterZ=0 NormalX=0 NormalY=0 NormalZ=1 AngleXU=0 Radius=1
    g43: Circle CenterX=179.022 CenterY=124.221 CenterZ=0 NormalX=0 NormalY=0 NormalZ=1 AngleXU=0 Radius=1
    g44: Circle CenterX=179.022 CenterY=120.221 CenterZ=0 NormalX=0 NormalY=0 NormalZ=1 AngleXU=0 Radius=1
    g45: BSplineCurve PolesCount=3 KnotsCount=2 Degree=2 IsPeriodic=0
    g46: GeomPoint X=175.022 Y=124.221 Z=0
    g47: GeomPoint X=179.022 Y=120.221 Z=0
    g48: LineSegment StartX=232.071 StartY=124.221 StartZ=0 EndX=232.071 EndY=127.221 EndZ=0
    g49-g52: Circle x4 (B-spline internal-alignment scaffolding for g53; pole/knot coordinates omitted)
    g53: BSplineCurve PolesCount=5 KnotsCount=3 Degree=3 IsPeriodic=0
    g54: GeomPoint X=232.072 Y=133.221 Z=0
    g55: GeomPoint X=223.072 Y=130.221 Z=0
    g56: GeomPoint X=232.071 Y=127.221 Z=0
    g57-g61: Circle x5 (B-spline internal-alignment scaffolding for g62; pole/knot coordinates omitted)
    g62: BSplineCurve PolesCount=5 KnotsCount=3 Degree=3 IsPeriodic=0
    g63: GeomPoint X=132.072 Y=133.221 Z=0
    g64: GeomPoint X=141.072 Y=130.221 Z=0
    g65: GeomPoint X=132.072 Y=127.221 Z=0
    g66: ArcOfCircle CenterX=247.391 CenterY=52.0843 CenterZ=0 NormalX=0 NormalY=0 NormalZ=1 AngleXU=0 Radius=4.24264 StartAngle=4.42912 EndAngle=9.14151
    g67: LineSegment StartX=240.687 StartY=51.8263 StartZ=0 EndX=239.192 EndY=54.5542 EndZ=0
    g68: LineSegment StartX=243.575 StartY=46.5669 StartZ=0 EndX=245.072 EndY=43.8408 EndZ=0
    g69: LineSegment StartX=240.168 StartY=69.471 StartZ=0 EndX=241.708 EndY=67.6172 EndZ=0
    g70: LineSegment StartX=246.783 StartY=71.8328 StartZ=0 EndX=248.546 EndY=69.7098 EndZ=0
    g71: LineSegment StartX=245.073 StartY=63.5726 StartZ=0 EndX=243.476 EndY=65.4955 EndZ=0
    g72: LineSegment StartX=123.967 StartY=69.4706 StartZ=0 EndX=122.37 EndY=67.5474 EndZ=0
    g73: LineSegment StartX=232.072 StartY=133.221 StartZ=0 EndX=232.072 EndY=136.221 EndZ=0
    g74: LineSegment StartX=232.072 StartY=136.221 StartZ=0 EndX=132.072 EndY=136.221 EndZ=0
    g75: LineSegment StartX=132.072 StartY=136.221 StartZ=0 EndX=132.072 EndY=133.221 EndZ=0
    g76: LineSegment StartX=132.072 StartY=127.221 StartZ=0 EndX=132.072 EndY=124.221 EndZ=0
    g77: LineSegment StartX=132.072 StartY=124.221 StartZ=0 EndX=175.022 EndY=124.221 EndZ=0
    g78: LineSegment StartX=189.121 StartY=124.221 StartZ=0 EndX=232.071 EndY=124.221 EndZ=0
    g79: LineSegment StartX=185.124 StartY=120.221 StartZ=0 EndX=185.124 EndY=27.0606 EndZ=0
    g80: LineSegment StartX=189.124 StartY=27.0628 StartZ=0 EndX=240.168 EndY=69.471 EndZ=0
    g81: LineSegment StartX=241.708 StartY=67.6172 StartZ=0 EndX=246.783 EndY=71.8328 EndZ=0
    g82: LineSegment StartX=248.546 StartY=69.7098 StartZ=0 EndX=243.476 EndY=65.4955 EndZ=0
    g83: LineSegment StartX=245.073 StartY=63.5726 StartZ=0 EndX=236.824 EndY=56.7187 EndZ=0
    g84: LineSegment StartX=238.538 StartY=54.1951 StartZ=0 EndX=239.192 EndY=54.5542 EndZ=0
    g85: LineSegment StartX=240.687 StartY=51.8263 StartZ=0 EndX=243.317 EndY=53.2701 EndZ=0
    g86: LineSegment StartX=246.205 StartY=48.0108 StartZ=0 EndX=243.575 EndY=46.5669 EndZ=0
    g87: LineSegment StartX=245.072 StartY=43.8408 StartZ=0 EndX=198.275 EndY=18.1318 EndZ=0
    g88: LineSegment StartX=165.871 StartY=18.1458 StartZ=0 EndX=118.934 EndY=43.9178 EndZ=0
    g89: LineSegment StartX=118.934 StartY=43.9178 StartZ=0 EndX=120.377 EndY=46.5474 EndZ=0
    g90: LineSegment StartX=117.748 StartY=47.9913 StartZ=0 EndX=120.377 EndY=46.5474 EndZ=0
    g91: LineSegment StartX=120.635 StartY=53.2507 StartZ=0 EndX=123.265 EndY=51.8068 EndZ=0
    g92: LineSegment StartX=123.265 StartY=51.8068 StartZ=0 EndX=124.73 EndY=54.6766 EndZ=0
    g93: ArcOfCircle CenterX=116.562 CenterY=52.0649 CenterZ=0 NormalX=0 NormalY=0 NormalZ=1 AngleXU=0 Radius=4.24264 StartAngle=0.283267 EndAngle=4.99566
    g94: LineSegment StartX=124.73 StartY=54.6766 StartZ=0 EndX=125.607 EndY=54.1951 EndZ=0
    g95: LineSegment StartX=127.326 StartY=56.7187 StartZ=0 EndX=119.072 EndY=63.5741 EndZ=0
    g96: LineSegment StartX=119.072 StartY=63.5741 StartZ=0 EndX=120.669 EndY=65.4973 EndZ=0
    g97: LineSegment StartX=120.669 StartY=65.4973 StartZ=0 EndX=115.591 EndY=69.7147 EndZ=0
    g98: LineSegment StartX=115.591 StartY=69.7147 StartZ=0 EndX=117.293 EndY=71.7641 EndZ=0
    g99: LineSegment StartX=117.293 StartY=71.7641 StartZ=0 EndX=122.37 EndY=67.5474 EndZ=0
    g100: LineSegment StartX=123.967 StartY=69.4706 StartZ=0 EndX=175.025 EndY=27.0667 EndZ=0
    g101: LineSegment StartX=179.022 StartY=27.0606 StartZ=0 EndX=179.022 EndY=120.221 EndZ=0
    g102-g117: Circle x16 (B-spline internal-alignment scaffolding for g118; pole/knot coordinates omitted)
    g118: BSplineCurve PolesCount=16 KnotsCount=14 Degree=3 IsPeriodic=0
    g119-g132: GeomPoint x14 (B-spline internal-alignment scaffolding for g118; pole/knot coordinates omitted)
  constraints (180):
    c: Weight(g0) = 1
    c: Equal(g0,g1)
    c: Equal(g0,g2)
    c: InternalAlignment(g0,g3)
    c: InternalAlignment(g1,g3)
    c: InternalAlignment(g2,g3)
    c: InternalAlignment(g4,g3)
    c: InternalAlignment(g5,g3)
    c: Weight(g6) = 1
    c: Equal(g6,g7)
    c: Equal(g6,g8)
    c: InternalAlignment(g6,g9)
    c: InternalAlignment(g7,g9)
    c: InternalAlignment(g8,g9)
    c: InternalAlignment(g10,g9)
    c: InternalAlignment(g11,g9)
    c: Block(g9)
    c: Block(g3)
    c: Weight(g12) = 1
    c: Equal(g12,g13)
    c: Equal(g12,g14)
    c: InternalAlignment(g12,g15)
    c: InternalAlignment(g13,g15)
    c: InternalAlignment(g14,g15)
    c: InternalAlignment(g16,g15)
    c: InternalAlignment(g17,g15)
    c: Weight(g18) = 1
    c: Equal(g18,g19)
    c: Equal(g18,g20)
    c: InternalAlignment(g18,g21)
    c: InternalAlignment(g19,g21)
    c: InternalAlignment(g20,g21)
    c: InternalAlignment(g22,g21)
    c: InternalAlignment(g23,g21)
    c: Block(g15)
    c: Block(g21)
    c: Weight(g24) = 1
    c: Equal(g24,g25)
    c: Equal(g24,g26)
    c: InternalAlignment(g24,g27)
    c: InternalAlignment(g25,g27)
    c: InternalAlignment(g26,g27)
    c: InternalAlignment(g28,g27)
    c: InternalAlignment(g29,g27)
    c: Block(g27)
    c: Weight(g30) = 1
    c: Equal(g30,g31)
    c: Equal(g30,g32)
    c: InternalAlignment(g30,g33)
    c: InternalAlignment(g31,g33)
    c: InternalAlignment(g32,g33)
    c: InternalAlignment(g34,g33)
    c: InternalAlignment(g35,g33)
    c: Block(g33)
    c: Weight(g36) = 1
    c: Equal(g36,g37)
    c: Equal(g36,g38)
    c: InternalAlignment(g36,g39)
    c: InternalAlignment(g37,g39)
    c: InternalAlignment(g38,g39)
    c: InternalAlignment(g40,g39)
    c: InternalAlignment(g41,g39)
    c: Weight(g42) = 1
    c: Equal(g42,g43)
    c: Equal(g42,g44)
    c: InternalAlignment(g42,g45)
    c: InternalAlignment(g43,g45)
    c: InternalAlignment(g44,g45)
    c: InternalAlignment(g46,g45)
    c: InternalAlignment(g47,g45)
    c: Block(g45)
    c: Block(g39)
    c: Vertical(g48)
    c: Distance(g48) = 3
    c: Weight(g49) = 1
    c: Equal(g49,g50)
    c: Equal(g49,g51)
    c: Equal(g49,g52)
    c: Coincident(g53,g48)
    c: InternalAlignment(g49-g52 -> g53) x4
    c: InternalAlignment(g54,g53)
    c: InternalAlignment(g55,g53)
    c: InternalAlignment(g56,g53)
    c: Weight(g57) = 1
    c: Equal(g57, g58-g61) x4
    c: InternalAlignment(g57-g61 -> g62) x5
    c: InternalAlignment(g63,g62)
    c: InternalAlignment(g64,g62)
    c: InternalAlignment(g65,g62)
    c: Block(g62)
    c: Block(g67)
    c: Block(g68)
    c: Distance(g69) = 2.41
    c: Distance(g70) = 2.76
    c: Distance(g71) = 2.5
    c: Distance(g72) = 2.5
    c: Block(g66)
    c: Block(g48)
    c: Block(g53)
    c: Coincident(g73,g53)
    c: Vertical(g73)
    c: Distance(g73) = 3
    c: Coincident(g74,g73)
    c: Horizontal(g74)
    c: Distance(g74) = 100
    c: Coincident(g75,g74)
    c: Coincident(g75,g62)
    c: Vertical(g75)
    c: Distance(g75) = 3
    c: Coincident(g76,g62)
    c: Vertical(g76)
    c: Distance(g76) = 3
    c: Coincident(g77,g76)
    c: Coincident(g77,g45)
    c: Horizontal(g77)
    c: Distance(g77) = 42.95
    c: Coincident(g78,g39)
    c: Coincident(g78,g48)
    c: Horizontal(g78)
    c: Distance(g78) = 42.95
    c: Coincident(g79,g39)
    c: Coincident(g79,g9)
    c: Vertical(g79)
    c: Distance(g79) = 93.16
    c: Coincident(g80,g9)
    c: Coincident(g80,g69)
    c: Angle(g80) = 0.693245
    c: Block(g80)
    c: Coincident(g81,g69)
    c: Coincident(g81,g70)
    c: Block(g81)
    c: Coincident(g82,g70)
    c: Coincident(g82,g71)
    c: Block(g82)
    c: Coincident(g83,g71)
    c: Coincident(g83,g33)
    c: Block(g71)
    c: Coincident(g84,g33)
    c: Coincident(g84,g67)
    c: Coincident(g85,g67)
    c: Coincident(g85,g66)
    c: Coincident(g86,g66)
    c: Coincident(g86,g68)
    c: Coincident(g87,g68)
    c: Coincident(g87,g21)
    c: Coincident(g88,g15)
    c: Coincident(g89,g88)
    c: Block(g89)
    c: Coincident(g90,g89)
    c: Block(g90)
    c: Block(g91)
    c: Coincident(g92,g91)
    c: Block(g92)
    c: Coincident(g93,g91)
    c: Coincident(g93,g90)
    c: Block(g93)
    c: Coincident(g94,g92)
    c: Coincident(g94,g27)
    c: Coincident(g95,g27)
    c: Block(g95)
    c: Coincident(g96,g95)
    c: Coincident(g97,g96)
    c: Coincident(g98,g97)
    c: Coincident(g99,g98)
    c: Coincident(g99,g72)
    c: Block(g98)
    c: Block(g96)
    c: Block(g72)
    c: Coincident(g100,g72)
    c: Coincident(g100,g3)
    c: Coincident(g101,g3)
    c: Coincident(g101,g45)
    c: Vertical(g101)
    c: Coincident(g118,g21)
    c: Weight(g102) = 1
    c: Equal(g102, g103-g117) x15
    c: Coincident(g118,g15)
    c: InternalAlignment(g102-g117 -> g118) x16
    c: InternalAlignment(g119-g132 -> g118) x14
    c: Block(g118)
FEATURE [Sketcher::SketchObject] Sketch006  label="leftSideTop"
  FullyConstrained = true
  sketch-geometry (99):
    g0: Circle CenterX=61.1495 CenterY=111.695 CenterZ=0 NormalX=0 NormalY=0 NormalZ=1 AngleXU=0 Radius=1
    g1: Circle CenterX=58.0728 CenterY=114.251 CenterZ=0 NormalX=0 NormalY=0 NormalZ=1 AngleXU=0 Radius=1
    g2: Circle CenterX=58.0728 CenterY=110.251 CenterZ=0 NormalX=0 NormalY=0 NormalZ=1 AngleXU=0 Radius=1
    g3: BSplineCurve PolesCount=3 KnotsCount=2 Degree=2 IsPeriodic=0
    g4: GeomPoint X=61.1495 Y=111.695 Z=0
    g5: GeomPoint X=58.0728 Y=110.251 Z=0
    g6: Circle CenterX=61.5791 CenterY=89.3511 CenterZ=0 NormalX=0 NormalY=0 NormalZ=1 AngleXU=0 Radius=1
    g7: Circle CenterX=58.0728 CenterY=91.2763 CenterZ=0 NormalX=0 NormalY=0 NormalZ=1 AngleXU=0 Radius=1
    g8: Circle CenterX=58.0728 CenterY=95.2763 CenterZ=0 NormalX=0 NormalY=0 NormalZ=1 AngleXU=0 Radius=1
    g9: BSplineCurve PolesCount=3 KnotsCount=2 Degree=2 IsPeriodic=0
    g10: GeomPoint X=61.5791 Y=89.3511 Z=0
    g11: GeomPoint X=58.0728 Y=95.2763 Z=0
    g12: Circle CenterX=62.0728 CenterY=124.221 CenterZ=0 NormalX=0 NormalY=0 NormalZ=1 AngleXU=0 Radius=1
    g13: Circle CenterX=58.0728 CenterY=124.221 CenterZ=0 NormalX=0 NormalY=0 NormalZ=1 AngleXU=0 Radius=1
    g14: Circle CenterX=61.1496 CenterY=121.665 CenterZ=0 NormalX=0 NormalY=0 NormalZ=1 AngleXU=0 Radius=1
    g15: BSplineCurve PolesCount=3 KnotsCount=2 Degree=2 IsPeriodic=0
    g16: GeomPoint X=62.0728 Y=124.221 Z=0
    g17: GeomPoint X=61.1496 Y=121.665 Z=0
    g18: Circle CenterX=61.5791 CenterY=75.4095 CenterZ=0 NormalX=0 NormalY=0 NormalZ=1 AngleXU=0 Radius=1
    g19: Circle CenterX=58.0728 CenterY=77.3346 CenterZ=0 NormalX=0 NormalY=0 NormalZ=1 AngleXU=0 Radius=1
    g20: Circle CenterX=58.0728 CenterY=73.3346 CenterZ=0 NormalX=0 NormalY=0 NormalZ=1 AngleXU=0 Radius=1
    g21: BSplineCurve PolesCount=3 KnotsCount=2 Degree=2 IsPeriodic=0
    g22: GeomPoint X=61.5791 Y=75.4095 Z=0
    g23: GeomPoint X=58.0728 Y=73.3346 Z=0
    g24: Circle CenterX=2.07281 CenterY=124.221 CenterZ=0 NormalX=0 NormalY=0 NormalZ=1 AngleXU=0 Radius=1
    g25: Circle CenterX=1.57905 CenterY=122.295 CenterZ=0 NormalX=0 NormalY=0 NormalZ=1 AngleXU=0 Radius=1
    g26: BSplineCurve PolesCount=3 KnotsCount=2 Degree=2 IsPeriodic=0
    g27: GeomPoint X=2.07281 Y=124.221 Z=0
    g28: GeomPoint X=1.57905 Y=122.295 Z=0
    g29: Circle CenterX=46.0728 CenterY=124.221 CenterZ=0 NormalX=0 NormalY=0 NormalZ=1 AngleXU=0 Radius=1
    g30: Circle CenterX=46.0728 CenterY=120.221 CenterZ=0 NormalX=0 NormalY=0 NormalZ=1 AngleXU=0 Radius=1
    g31: BSplineCurve PolesCount=3 KnotsCount=2 Degree=2 IsPeriodic=0
    g32: GeomPoint X=42.0728 Y=124.221 Z=0
    g33: GeomPoint X=46.0728 Y=120.221 Z=0
    g34: Circle CenterX=46.0728 CenterY=109.865 CenterZ=0 NormalX=0 NormalY=0 NormalZ=1 AngleXU=0 Radius=1
    g35: Circle CenterX=46.0728 CenterY=105.865 CenterZ=0 NormalX=0 NormalY=0 NormalZ=1 AngleXU=0 Radius=1
    g36: Circle CenterX=42.0728 CenterY=105.865 CenterZ=0 NormalX=0 NormalY=0 NormalZ=1 AngleXU=0 Radius=1
    g37: BSplineCurve PolesCount=3 KnotsCount=2 Degree=2 IsPeriodic=0
    g38: GeomPoint X=46.0728 Y=109.865 Z=0
    g39: GeomPoint X=42.0728 Y=105.865 Z=0
    g40: Circle CenterX=35.5028 CenterY=105.865 CenterZ=0 NormalX=0 NormalY=0 NormalZ=1 AngleXU=0 Radius=1
    g41: Circle CenterX=31.5028 CenterY=105.865 CenterZ=0 NormalX=0 NormalY=0 NormalZ=1 AngleXU=0 Radius=1
    g42: Circle CenterX=27.9965 CenterY=107.79 CenterZ=0 NormalX=0 NormalY=0 NormalZ=1 AngleXU=0 Radius=1
    g43: BSplineCurve PolesCount=3 KnotsCount=2 Degree=2 IsPeriodic=0
    g44: GeomPoint X=35.5028 Y=105.865 Z=0
    g45: GeomPoint X=27.9965 Y=107.79 Z=0
    g46-g50: Circle x5 (B-spline internal-alignment scaffolding for g51; pole/knot coordinates omitted)
    g51: BSplineCurve PolesCount=5 KnotsCount=3 Degree=3 IsPeriodic=0
    g52: GeomPoint X=132.072 Y=133.221 Z=0
    g53: GeomPoint X=141.072 Y=130.221 Z=0
    g54: GeomPoint X=132.072 Y=127.221 Z=0
    g55: ArcOfCircle CenterX=116.562 CenterY=52.0649 CenterZ=0 NormalX=0 NormalY=0 NormalZ=1 AngleXU=0 Radius=4.24264 StartAngle=0.283268 EndAngle=4.99566
    g56: LineSegment StartX=123.967 StartY=69.4706 StartZ=0 EndX=122.37 EndY=67.5474 EndZ=0
    g57: LineSegment StartX=117.293 StartY=71.7641 StartZ=0 EndX=115.591 EndY=69.7147 EndZ=0
    g58: LineSegment StartX=120.669 StartY=65.4973 StartZ=0 EndX=119.072 EndY=63.5741 EndZ=0
    g59: LineSegment StartX=124.73 StartY=54.6766 StartZ=0 EndX=123.265 EndY=51.8068 EndZ=0
    g60: LineSegment StartX=120.377 StartY=46.5474 StartZ=0 EndX=118.934 EndY=43.9178 EndZ=0
    g61: BSplineCurve PolesCount=3 KnotsCount=2 Degree=2 IsPeriodic=0
    g62: BSplineCurve PolesCount=3 KnotsCount=2 Degree=2 IsPeriodic=0
    g63: LineSegment StartX=61.5791 StartY=75.4095 StartZ=0 EndX=118.934 EndY=43.9178 EndZ=0
    g64: LineSegment StartX=117.748 StartY=47.9913 StartZ=0 EndX=120.377 EndY=46.5474 EndZ=0
    g65: LineSegment StartX=120.635 StartY=53.2507 StartZ=0 EndX=123.265 EndY=51.8068 EndZ=0
    g66: LineSegment StartX=124.73 StartY=54.6766 StartZ=0 EndX=61.5791 EndY=89.3511 EndZ=0
    g67: LineSegment StartX=58.0728 StartY=95.2763 StartZ=0 EndX=58.0728 EndY=110.251 EndZ=0
    g68: LineSegment StartX=61.1495 StartY=111.695 StartZ=0 EndX=119.072 EndY=63.5741 EndZ=0
    g69: LineSegment StartX=120.669 StartY=65.4973 StartZ=0 EndX=115.591 EndY=69.7147 EndZ=0
    g70: LineSegment StartX=117.293 StartY=71.7641 StartZ=0 EndX=122.37 EndY=67.5474 EndZ=0
    g71: LineSegment StartX=123.967 StartY=69.4706 StartZ=0 EndX=61.1496 EndY=121.665 EndZ=0
    g72: LineSegment StartX=62.0728 StartY=124.221 StartZ=0 EndX=132.072 EndY=124.221 EndZ=0
    g73: LineSegment StartX=132.072 StartY=127.221 StartZ=0 EndX=132.072 EndY=124.221 EndZ=0
    g74: LineSegment StartX=132.072 StartY=133.221 StartZ=0 EndX=132.072 EndY=136.221 EndZ=0
    g75: LineSegment StartX=132.072 StartY=136.221 StartZ=0 EndX=-42.9272 EndY=136.221 EndZ=0
    g76: LineSegment StartX=2.07281 StartY=124.221 StartZ=0 EndX=42.0728 EndY=124.221 EndZ=0
    g77: LineSegment StartX=46.0728 StartY=120.221 StartZ=0 EndX=46.0728 EndY=109.865 EndZ=0
    g78: LineSegment StartX=42.0728 StartY=105.865 StartZ=0 EndX=35.5028 EndY=105.865 EndZ=0
    g79: LineSegment StartX=27.9965 StartY=107.79 StartZ=0 EndX=1.57905 EndY=122.295 EndZ=0
    g80: LineSegment StartX=-6.92718 StartY=76.4095 StartZ=0 EndX=42.0728 EndY=76.4095 EndZ=0
    g81: LineSegment StartX=-17.9272 StartY=48.2206 StartZ=0 EndX=-17.9272 EndY=58.2206 EndZ=0
    g82: LineSegment StartX=-35.9272 StartY=48.2206 StartZ=0 EndX=-35.9272 EndY=52.2206 EndZ=0
    g83: LineSegment StartX=-29.9272 StartY=48.2206 StartZ=0 EndX=-29.9272 EndY=52.2206 EndZ=0
    g84: LineSegment StartX=-23.9272 StartY=48.2206 StartZ=0 EndX=-23.9272 EndY=58.2206 EndZ=0
    g85: ArcOfCircle CenterX=-32.9272 CenterY=55.2206 CenterZ=0 NormalX=0 NormalY=0 NormalZ=1 AngleXU=0 Radius=4.24264 StartAngle=5.49779 EndAngle=10.2102
    g86: ArcOfCircle CenterX=-20.9272 CenterY=61.2206 CenterZ=0 NormalX=0 NormalY=0 NormalZ=1 AngleXU=0 Radius=4.24264 StartAngle=5.49779 EndAngle=10.2102
    g87: LineSegment StartX=-10.9272 StartY=48.2206 StartZ=0 EndX=-10.9272 EndY=72.4095 EndZ=0
    g88: LineSegment StartX=-42.9272 StartY=48.2206 StartZ=0 EndX=-42.9272 EndY=136.221 EndZ=0
    g89: LineSegment StartX=46.0728 StartY=72.4095 StartZ=0 EndX=46.0728 EndY=-27.5905 EndZ=0
    g90: LineSegment StartX=58.0728 StartY=-27.5905 StartZ=0 EndX=58.0728 EndY=73.3346 EndZ=0
    g91: LineSegment StartX=50.0728 StartY=-27.5905 StartZ=0 EndX=50.0728 EndY=-31.5905 EndZ=0
    g92: LineSegment StartX=54.0728 StartY=-27.5905 StartZ=0 EndX=54.0728 EndY=-31.5905 EndZ=0
    g93: ArcOfCircle CenterX=52.0728 CenterY=-33.5905 CenterZ=0 NormalX=0 NormalY=0 NormalZ=1 AngleXU=0 Radius=2.82843 StartAngle=2.35619 EndAngle=7.06858
    g94: LineSegment StartX=46.0728 StartY=-27.5905 StartZ=0 EndX=50.0728 EndY=-27.5905 EndZ=0
    g95: LineSegment StartX=54.0728 StartY=-27.5905 StartZ=0 EndX=58.0728 EndY=-27.5905 EndZ=0
    g96: LineSegment StartX=-17.9272 StartY=48.2206 StartZ=0 EndX=-10.9272 EndY=48.2206 EndZ=0
    g97: LineSegment StartX=-29.9272 StartY=48.2206 StartZ=0 EndX=-23.9272 EndY=48.2206 EndZ=0
    g98: LineSegment StartX=-42.9272 StartY=48.2206 StartZ=0 EndX=-35.9272 EndY=48.2206 EndZ=0
  constraints (172):
    c: Weight(g0) = 1
    c: Equal(g0,g1)
    c: Equal(g0,g2)
    c: InternalAlignment(g0,g3)
    c: InternalAlignment(g1,g3)
    c: InternalAlignment(g2,g3)
    c: InternalAlignment(g4,g3)
    c: InternalAlignment(g5,g3)
    c: Weight(g6) = 1
    c: Equal(g6,g7)
    c: Equal(g6,g8)
    c: InternalAlignment(g6,g9)
    c: InternalAlignment(g7,g9)
    c: InternalAlignment(g8,g9)
    c: InternalAlignment(g10,g9)
    c: InternalAlignment(g11,g9)
    c: Block(g3)
    c: Block(g9)
    c: Weight(g12) = 1
    c: Equal(g12,g13)
    c: Equal(g12,g14)
    c: InternalAlignment(g12,g15)
    c: InternalAlignment(g13,g15)
    c: InternalAlignment(g14,g15)
    c: InternalAlignment(g16,g15)
    c: InternalAlignment(g17,g15)
    c: Block(g15)
    c: Weight(g18) = 1
    c: Equal(g18,g19)
    c: Equal(g18,g20)
    c: InternalAlignment(g18,g21)
    c: InternalAlignment(g19,g21)
    c: InternalAlignment(g20,g21)
    c: InternalAlignment(g22,g21)
    c: InternalAlignment(g23,g21)
    c: Block(g21)
    c: Weight(g24) = 1
    c: Equal(g24,g25)
    c: InternalAlignment(g24,g26)
    c: InternalAlignment(g25,g26)
    c: InternalAlignment(g27,g26)
    c: InternalAlignment(g28,g26)
    c: InternalAlignment(g29,g31)
    c: InternalAlignment(g30,g31)
    c: InternalAlignment(g32,g31)
    c: InternalAlignment(g33,g31)
    c: Weight(g34) = 1
    c: Equal(g34,g35)
    c: Equal(g34,g36)
    c: InternalAlignment(g34,g37)
    c: InternalAlignment(g35,g37)
    c: InternalAlignment(g36,g37)
    c: InternalAlignment(g38,g37)
    c: InternalAlignment(g39,g37)
    c: Equal(g40,g41)
    c: Equal(g40,g42)
    c: InternalAlignment(g40,g43)
    c: InternalAlignment(g41,g43)
    c: InternalAlignment(g42,g43)
    c: InternalAlignment(g44,g43)
    c: InternalAlignment(g45,g43)
    c: Block(g31)
    c: Block(g37)
    c: Block(g43)
    c: Block(g26)
    c: Weight(g46) = 1
    c: Equal(g46, g47-g50) x4
    c: InternalAlignment(g46-g50 -> g51) x5
    c: InternalAlignment(g52,g51)
    c: InternalAlignment(g53,g51)
    c: InternalAlignment(g54,g51)
    c: Block(g51)
    c: Block(g55)
    c: Block(g56)
    c: Block(g57)
    c: Block(g58)
    c: Block(g59)
    c: Block(g60)
    c: Block(g61)
    c: Block(g62)
    c: Coincident(g90,g21)
    c: Coincident(g63,g21)
    c: Coincident(g63,g60)
    c: Coincident(g64,g55)
    c: Coincident(g64,g60)
    c: Coincident(g65,g55)
    c: Coincident(g65,g59)
    c: Coincident(g66,g59)
    c: Coincident(g66,g9)
    c: Coincident(g67,g9)
    c: Coincident(g67,g3)
    c: Vertical(g67)
    c: Coincident(g68,g3)
    c: Coincident(g68,g58)
    c: Coincident(g69,g58)
    c: Coincident(g69,g57)
    c: Coincident(g70,g57)
    c: Coincident(g70,g56)
    c: Coincident(g71,g56)
    c: Coincident(g71,g15)
    c: Coincident(g72,g15)
    c: Horizontal(g72)
    c: Coincident(g73,g51)
    c: Coincident(g73,g72)
    c: Vertical(g73)
    c: Coincident(g74,g51)
    c: Vertical(g74)
    c: Coincident(g75,g74)
    c: Horizontal(g75)
    c: Coincident(g76,g26)
    c: Coincident(g76,g31)
    c: Horizontal(g76)
    c: Coincident(g77,g31)
    c: Coincident(g77,g37)
    c: Vertical(g77)
    c: Coincident(g78,g37)
    c: Coincident(g78,g43)
    c: Horizontal(g78)
    c: Coincident(g79,g43)
    c: Coincident(g79,g26)
    c: Coincident(g80,g62)
    c: Coincident(g80,g61)
    c: Horizontal(g80)
    c: Vertical(g81)
    c: Distance(g81) = 10
    c: Vertical(g82)
    c: Distance(g82) = 4
    c: Vertical(g83)
    c: Distance(g83) = 4
    c: Vertical(g84)
    c: Distance(g84) = 10
    c: Coincident(g85,g83)
    c: Coincident(g85,g82)
    c: Block(g85)
    c: Coincident(g86,g84)
    c: Coincident(g86,g81)
    c: Block(g86)
    c: Coincident(g87,g62)
    c: Vertical(g87)
    c: Coincident(g88,g75)
    c: Vertical(g88)
    c: Block(g75)
    c: Coincident(g89,g61)
    c: Vertical(g89)
    c: Distance(g89) = 100
    c: Block(g90)
    c: Vertical(g91)
    c: Distance(g91) = 4
    c: Vertical(g92)
    c: Distance(g92) = 4
    c: Coincident(g93,g91)
    c: Coincident(g93,g92)
    c: Block(g93)
    c: Coincident(g94,g89)
    c: Coincident(g94,g91)
    c: Horizontal(g94)
    c: Distance(g94) = 4
    c: Coincident(g95,g92)
    c: Coincident(g95,g90)
    c: Horizontal(g95)
    c: Distance(g95) = 4
    c: Block(g87)
    c: Block(g88)
    c: Coincident(g96,g81)
    c: Coincident(g96,g87)
    c: Horizontal(g96)
    c: Coincident(g97,g83)
    c: Coincident(g97,g84)
    c: Horizontal(g97)
    c: Coincident(g98,g88)
    c: Coincident(g98,g82)
    c: Horizontal(g98)
FEATURE [Sketcher::SketchObject] Sketch007  label="leftSideBottom"
  FullyConstrained = true
  sketch-geometry (92):
    g0: ArcOfCircle CenterX=-26.9272 CenterY=-83.7794 CenterZ=0 NormalX=0 NormalY=0 NormalZ=1 AngleXU=0 Radius=8 StartAngle=3.14159 EndAngle=6.28319
    g1: Circle CenterX=61.5791 CenterY=-56.9099 CenterZ=0 NormalX=0 NormalY=0 NormalZ=1 AngleXU=0 Radius=1
    g2: Circle CenterX=58.0728 CenterY=-58.8351 CenterZ=0 NormalX=0 NormalY=0 NormalZ=1 AngleXU=0 Radius=1
    g3: Circle CenterX=58.0728 CenterY=-62.8351 CenterZ=0 NormalX=0 NormalY=0 NormalZ=1 AngleXU=0 Radius=1
    g4: BSplineCurve PolesCount=3 KnotsCount=2 Degree=2 IsPeriodic=0
    g5: GeomPoint X=61.5791 Y=-56.9099 Z=0
    g6: GeomPoint X=58.0728 Y=-62.8351 Z=0
    g7: Circle CenterX=58.0728 CenterY=-77.8102 CenterZ=0 NormalX=0 NormalY=0 NormalZ=1 AngleXU=0 Radius=1
    g8: Circle CenterX=58.0728 CenterY=-81.8102 CenterZ=0 NormalX=0 NormalY=0 NormalZ=1 AngleXU=0 Radius=1
    g9: Circle CenterX=61.1496 CenterY=-79.2541 CenterZ=0 NormalX=0 NormalY=0 NormalZ=1 AngleXU=0 Radius=1
    g10: BSplineCurve PolesCount=3 KnotsCount=2 Degree=2 IsPeriodic=0
    g11: GeomPoint X=58.0728 Y=-77.8102 Z=0
    g12: GeomPoint X=61.1496 Y=-79.2541 Z=0
    g13: Circle CenterX=61.6457 CenterY=-88.8112 CenterZ=0 NormalX=0 NormalY=0 NormalZ=1 AngleXU=0 Radius=1
    g14: Circle CenterX=58.0728 CenterY=-91.7794 CenterZ=0 NormalX=0 NormalY=0 NormalZ=1 AngleXU=0 Radius=1
    g15: Circle CenterX=63.9135 CenterY=-91.8014 CenterZ=0 NormalX=0 NormalY=0 NormalZ=1 AngleXU=0 Radius=1
    g16: BSplineCurve PolesCount=3 KnotsCount=2 Degree=2 IsPeriodic=0
    g17: GeomPoint X=61.6457 Y=-88.8112 Z=0
    g18: GeomPoint X=63.9135 Y=-91.8014 Z=0
    g19: Circle CenterX=58.0728 CenterY=-40.8935 CenterZ=0 NormalX=0 NormalY=0 NormalZ=1 AngleXU=0 Radius=1
    g20: Circle CenterX=58.0728 CenterY=-44.8935 CenterZ=0 NormalX=0 NormalY=0 NormalZ=1 AngleXU=0 Radius=1
    g21: Circle CenterX=61.5791 CenterY=-42.9683 CenterZ=0 NormalX=0 NormalY=0 NormalZ=1 AngleXU=0 Radius=1
    g22: BSplineCurve PolesCount=3 KnotsCount=2 Degree=2 IsPeriodic=0
    g23: GeomPoint X=58.0728 Y=-40.8935 Z=0
    g24: GeomPoint X=61.5791 Y=-42.9683 Z=0
    g25: Circle CenterX=42.5666 CenterY=-67.3492 CenterZ=0 NormalX=0 NormalY=0 NormalZ=1 AngleXU=0 Radius=1
    g26: Circle CenterX=46.0728 CenterY=-65.424 CenterZ=0 NormalX=0 NormalY=0 NormalZ=1 AngleXU=0 Radius=1
    g27: Circle CenterX=46.0728 CenterY=-69.424 CenterZ=0 NormalX=0 NormalY=0 NormalZ=1 AngleXU=0 Radius=1
    g28: BSplineCurve PolesCount=3 KnotsCount=2 Degree=2 IsPeriodic=0
    g29: GeomPoint X=42.5666 Y=-67.3492 Z=0
    g30: GeomPoint X=46.0728 Y=-69.424 Z=0
    g31: Circle CenterX=2.07281 CenterY=-91.7794 CenterZ=0 NormalX=0 NormalY=0 NormalZ=1 AngleXU=0 Radius=1
    g32: Circle CenterX=-1.92719 CenterY=-91.7794 CenterZ=0 NormalX=0 NormalY=0 NormalZ=1 AngleXU=0 Radius=1
    g33: Circle CenterX=1.57905 CenterY=-89.8542 CenterZ=0 NormalX=0 NormalY=0 NormalZ=1 AngleXU=0 Radius=1
    g34: BSplineCurve PolesCount=3 KnotsCount=2 Degree=2 IsPeriodic=0
    g35: GeomPoint X=2.07281 Y=-91.7794 Z=0
    g36: GeomPoint X=1.57905 Y=-89.8542 Z=0
    g37: ArcOfCircle CenterX=-26.9272 CenterY=22.1087 CenterZ=0 NormalX=0 NormalY=0 NormalZ=1 AngleXU=0 Radius=4 StartAngle=5e-16 EndAngle=3.14159
    g38: Circle CenterX=-10.9272 CenterY=-78.7794 CenterZ=0 NormalX=0 NormalY=0 NormalZ=1 AngleXU=0 Radius=1
    g39: Circle CenterX=-10.9272 CenterY=-82.7794 CenterZ=0 NormalX=0 NormalY=0 NormalZ=1 AngleXU=0 Radius=1
    g40: Circle CenterX=-7.42095 CenterY=-80.8542 CenterZ=0 NormalX=0 NormalY=0 NormalZ=1 AngleXU=0 Radius=1
    g41: BSplineCurve PolesCount=3 KnotsCount=2 Degree=2 IsPeriodic=0
    g42: GeomPoint X=-10.9272 Y=-78.7794 Z=0
    g43: GeomPoint X=-7.42095 Y=-80.8542 Z=0
    g44: BSplineCurve PolesCount=3 KnotsCount=2 Degree=2 IsPeriodic=0
    g45: GeomPoint X=42.5666 Y=-53.4075 Z=0
    g46: GeomPoint X=46.0728 Y=-47.4823 Z=0
    g47: BSplineCurve PolesCount=5 KnotsCount=3 Degree=3 IsPeriodic=0
    g48: LineSegment StartX=124.814 StartY=-22.1885 StartZ=0 EndX=123.265 EndY=-19.3655 EndZ=0
    g49: ArcOfCircle CenterX=116.562 CenterY=-19.6236 CenterZ=0 NormalX=0 NormalY=0 NormalZ=1 AngleXU=0 Radius=4.24264 StartAngle=1.28753 EndAngle=6.00037
    g50: LineSegment StartX=-30.9272 StartY=22.1087 StartZ=0 EndX=-34.9272 EndY=-83.7794 EndZ=0
    g51: LineSegment StartX=-22.9272 StartY=22.1087 StartZ=0 EndX=-18.9272 EndY=-83.7794 EndZ=0
    g52: LineSegment StartX=118.934 StartY=-11.4765 StartZ=0 EndX=120.377 EndY=-14.1062 EndZ=0
    g53: LineSegment StartX=118.86 StartY=-31.3104 StartZ=0 EndX=120.377 EndY=-33.1447 EndZ=0
    g54: LineSegment StartX=115.291 StartY=-37.3514 StartZ=0 EndX=117.05 EndY=-39.4781 EndZ=0
    g55: LineSegment StartX=122.136 StartY=-35.2714 StartZ=0 EndX=123.656 EndY=-37.1092 EndZ=0
    g56: BSplineCurve PolesCount=3 KnotsCount=2 Degree=2 IsPeriodic=0
    g57: LineSegment StartX=132.072 StartY=-100.779 StartZ=0 EndX=132.072 EndY=-103.779 EndZ=0
    g58: LineSegment StartX=132.072 StartY=-91.8014 StartZ=0 EndX=132.072 EndY=-94.7791 EndZ=0
    g59: LineSegment StartX=63.9135 StartY=-91.8014 StartZ=0 EndX=132.072 EndY=-91.8014 EndZ=0
    g60: LineSegment StartX=61.6457 StartY=-88.8112 StartZ=0 EndX=123.656 EndY=-37.1092 EndZ=0
    g61: LineSegment StartX=122.136 StartY=-35.2714 StartZ=0 EndX=117.05 EndY=-39.4781 EndZ=0
    g62: LineSegment StartX=115.291 StartY=-37.3514 StartZ=0 EndX=120.377 EndY=-33.1447 EndZ=0
    g63: LineSegment StartX=118.86 StartY=-31.3104 StartZ=0 EndX=61.1496 EndY=-79.2541 EndZ=0
    g64: LineSegment StartX=58.0728 StartY=-77.8102 StartZ=0 EndX=58.0728 EndY=-62.8351 EndZ=0
    g65: LineSegment StartX=61.5791 StartY=-56.9099 StartZ=0 EndX=124.814 EndY=-22.1885 EndZ=0
    g66: LineSegment StartX=120.636 StartY=-20.8076 StartZ=0 EndX=123.265 EndY=-19.3655 EndZ=0
    g67: LineSegment StartX=117.748 StartY=-15.55 StartZ=0 EndX=120.377 EndY=-14.1062 EndZ=0
    g68: LineSegment StartX=118.934 StartY=-11.4765 StartZ=0 EndX=61.5791 EndY=-42.9683 EndZ=0
    g69: LineSegment StartX=-42.9272 StartY=-103.779 StartZ=0 EndX=132.072 EndY=-103.779 EndZ=0
    g70: LineSegment StartX=42.5666 StartY=-53.4075 StartZ=0 EndX=-7.42095 EndY=-80.8542 EndZ=0
    g71: LineSegment StartX=-10.9272 StartY=-78.7794 StartZ=0 EndX=-10.9272 EndY=48.2206 EndZ=0
    g72: LineSegment StartX=2.07281 StartY=-91.7794 StartZ=0 EndX=42.0728 EndY=-91.7794 EndZ=0
    g73: LineSegment StartX=46.0728 StartY=-87.7794 StartZ=0 EndX=46.0728 EndY=-69.424 EndZ=0
    g74: LineSegment StartX=42.5666 StartY=-67.3492 StartZ=0 EndX=1.57905 EndY=-89.8542 EndZ=0
    g75: LineSegment StartX=-42.9272 StartY=-103.779 StartZ=0 EndX=-42.9272 EndY=48.2206 EndZ=0
    g76: LineSegment StartX=-17.9272 StartY=48.2206 StartZ=0 EndX=-17.9272 EndY=58.2206 EndZ=0
    g77: LineSegment StartX=-35.9272 StartY=48.2206 StartZ=0 EndX=-35.9272 EndY=52.2206 EndZ=0
    g78: LineSegment StartX=-29.9272 StartY=48.2206 StartZ=0 EndX=-29.9272 EndY=52.2206 EndZ=0
    g79: LineSegment StartX=-23.9272 StartY=48.2206 StartZ=0 EndX=-23.9272 EndY=58.2206 EndZ=0
    g80: ArcOfCircle CenterX=-32.9272 CenterY=55.2206 CenterZ=0 NormalX=0 NormalY=0 NormalZ=1 AngleXU=0 Radius=4.24264 StartAngle=5.49779 EndAngle=10.2102
    g81: ArcOfCircle CenterX=-20.9272 CenterY=61.2206 CenterZ=0 NormalX=0 NormalY=0 NormalZ=1 AngleXU=0 Radius=4.24264 StartAngle=5.49779 EndAngle=10.2102
    g82: LineSegment StartX=-17.9272 StartY=48.2206 StartZ=0 EndX=-10.9272 EndY=48.2206 EndZ=0
    g83: LineSegment StartX=-42.9272 StartY=48.2206 StartZ=0 EndX=-35.9272 EndY=48.2206 EndZ=0
    g84: LineSegment StartX=50.0728 StartY=-27.5905 StartZ=0 EndX=50.0728 EndY=-31.5905 EndZ=0
    g85: LineSegment StartX=54.0728 StartY=-27.5905 StartZ=0 EndX=54.0728 EndY=-31.5905 EndZ=0
    g86: ArcOfCircle CenterX=52.0728 CenterY=-33.5905 CenterZ=0 NormalX=0 NormalY=0 NormalZ=1 AngleXU=0 Radius=2.82843 StartAngle=2.35619 EndAngle=7.06858
    g87: LineSegment StartX=46.0728 StartY=-27.5905 StartZ=0 EndX=50.0728 EndY=-27.5905 EndZ=0
    g88: LineSegment StartX=54.0728 StartY=-27.5905 StartZ=0 EndX=58.0728 EndY=-27.5905 EndZ=0
    g89: LineSegment StartX=46.0728 StartY=-27.5905 StartZ=0 EndX=46.0728 EndY=-47.4823 EndZ=0
    g90: LineSegment StartX=58.0728 StartY=-27.5905 StartZ=0 EndX=58.0728 EndY=-40.8935 EndZ=0
    g91: LineSegment StartX=-29.9272 StartY=48.2206 StartZ=0 EndX=-23.9272 EndY=48.2206 EndZ=0
  constraints (170):
    c: Weight(g1) = 1
    c: Equal(g1,g2)
    c: Equal(g1,g3)
    c: InternalAlignment(g1,g4)
    c: InternalAlignment(g2,g4)
    c: InternalAlignment(g3,g4)
    c: InternalAlignment(g5,g4)
    c: InternalAlignment(g6,g4)
    c: Weight(g7) = 1
    c: Equal(g7,g8)
    c: Equal(g7,g9)
    c: InternalAlignment(g7,g10)
    c: InternalAlignment(g8,g10)
    c: InternalAlignment(g9,g10)
    c: InternalAlignment(g11,g10)
    c: InternalAlignment(g12,g10)
    c: Block(g4)
    c: Block(g10)
    c: Weight(g13) = 1
    c: Equal(g13,g14)
    c: Equal(g13,g15)
    c: InternalAlignment(g13,g16)
    c: InternalAlignment(g14,g16)
    c: InternalAlignment(g15,g16)
    c: InternalAlignment(g17,g16)
    c: InternalAlignment(g18,g16)
    c: Block(g16)
    c: Weight(g19) = 1
    c: Equal(g19,g20)
    c: Equal(g19,g21)
    c: InternalAlignment(g19,g22)
    c: InternalAlignment(g20,g22)
    c: InternalAlignment(g21,g22)
    c: InternalAlignment(g23,g22)
    c: InternalAlignment(g24,g22)
    c: Block(g22)
    c: Weight(g25) = 1
    c: Equal(g25,g26)
    c: Equal(g25,g27)
    c: InternalAlignment(g25,g28)
    c: InternalAlignment(g26,g28)
    c: InternalAlignment(g27,g28)
    c: InternalAlignment(g29,g28)
    c: InternalAlignment(g30,g28)
    c: Weight(g31) = 1
    c: Equal(g31,g32)
    c: Equal(g31,g33)
    c: InternalAlignment(g31,g34)
    c: InternalAlignment(g32,g34)
    c: InternalAlignment(g33,g34)
    c: InternalAlignment(g35,g34)
    c: InternalAlignment(g36,g34)
    c: Block(g34)
    c: Block(g28)
    c: Block(g37)
    c: Block(g0)
    c: Weight(g38) = 1
    c: Equal(g38,g40)
    c: InternalAlignment(g38,g41)
    c: InternalAlignment(g39,g41)
    c: InternalAlignment(g40,g41)
    c: InternalAlignment(g42,g41)
    c: InternalAlignment(g43,g41)
    c: InternalAlignment(g45,g44)
    c: InternalAlignment(g46,g44)
    c: Block(g47)
    c: Block(g44)
    c: Block(g41)
    c: Block(g48)
    c: Block(g49)
    c: Coincident(g50,g37)
    c: Coincident(g50,g0)
    c: Coincident(g51,g37)
    c: Coincident(g51,g0)
    c: Block(g51)
    c: Block(g50)
    c: Block(g52)
    c: Block(g53)
    c: Block(g54)
    c: Block(g55)
    c: Block(g56)
    c: Coincident(g57,g47)
    c: Vertical(g57)
    c: Coincident(g58,g47)
    c: Vertical(g58)
    c: Coincident(g59,g16)
    c: Coincident(g59,g58)
    c: Horizontal(g59)
    c: Coincident(g60,g16)
    c: Coincident(g60,g55)
    c: Coincident(g61,g55)
    c: Coincident(g61,g54)
    c: Coincident(g62,g54)
    c: Coincident(g62,g53)
    c: Coincident(g63,g53)
    c: Coincident(g63,g10)
    c: Coincident(g64,g10)
    c: Coincident(g64,g4)
    c: Vertical(g64)
    c: Coincident(g65,g4)
    c: Coincident(g65,g48)
    c: Coincident(g66,g49)
    c: Coincident(g66,g48)
    c: Coincident(g67,g49)
    c: Coincident(g67,g52)
    c: Coincident(g68,g52)
    c: Coincident(g68,g22)
    c: Coincident(g69,g57)
    c: Horizontal(g69)
    c: Coincident(g70,g44)
    c: Coincident(g70,g41)
    c: Coincident(g71,g41)
    c: Vertical(g71)
    c: Coincident(g72,g34)
    c: Coincident(g72,g56)
    c: Horizontal(g72)
    c: Coincident(g73,g56)
    c: Coincident(g73,g28)
    c: Vertical(g73)
    c: Coincident(g74,g28)
    c: Coincident(g74,g34)
    c: Block(g69)
    c: Coincident(g75,g69)
    c: Vertical(g75)
    c: Distance(g75) = 152
    c: Block(g71)
    c: Vertical(g76)
    c: Distance(g76) = 10
    c: Vertical(g77)
    c: Distance(g77) = 4
    c: Vertical(g78)
    c: Distance(g78) = 4
    c: Vertical(g79)
    c: Distance(g79) = 10
    c: Coincident(g80,g78)
    c: Coincident(g80,g77)
    c: Block(g80)
    c: Coincident(g81,g79)
    c: Coincident(g81,g76)
    c: Block(g81)
    c: Coincident(g82,g76)
    c: Coincident(g82,g71)
    c: Horizontal(g82)
    c: Coincident(g83,g75)
    c: Coincident(g83,g77)
    c: Horizontal(g83)
    c: Distance(g83) = 7
    c: Distance(g82) = 7
    c: Vertical(g84)
    c: Distance(g84) = 4
    c: Vertical(g85)
    c: Distance(g85) = 4
    c: Coincident(g86,g84)
    c: Coincident(g86,g85)
    c: Block(g86)
    c: Coincident(g87,g84)
    c: Horizontal(g87)
    c: Distance(g87) = 4
    c: Coincident(g88,g85)
    c: Horizontal(g88)
    c: Distance(g88) = 4
    c: Coincident(g89,g87)
    c: Coincident(g89,g44)
    c: Vertical(g89)
    c: Coincident(g90,g88)
    c: Coincident(g90,g22)
    c: Vertical(g90)
    c: Coincident(g91,g78)
    c: Coincident(g91,g79)
    c: Horizontal(g91)
FEATURE [Sketcher::SketchObject] Sketch008  label="rightSideTop"
  FullyConstrained = false
  sketch-geometry (108):
    g0: Circle CenterX=302.996 CenterY=111.695 CenterZ=0 NormalX=0 NormalY=0 NormalZ=1 AngleXU=0 Radius=1
    g1: Circle CenterX=306.073 CenterY=114.251 CenterZ=0 NormalX=0 NormalY=0 NormalZ=1 AngleXU=0 Radius=1
    g2: Circle CenterX=306.073 CenterY=110.251 CenterZ=0 NormalX=0 NormalY=0 NormalZ=1 AngleXU=0 Radius=1
    g3: BSplineCurve PolesCount=3 KnotsCount=2 Degree=2 IsPeriodic=0
    g4: GeomPoint X=302.996 Y=111.695 Z=0
    g5: GeomPoint X=306.073 Y=110.251 Z=0
    g6: Circle CenterX=306.073 CenterY=95.2763 CenterZ=0 NormalX=0 NormalY=0 NormalZ=1 AngleXU=0 Radius=1
    g7: Circle CenterX=306.073 CenterY=91.2763 CenterZ=0 NormalX=0 NormalY=0 NormalZ=1 AngleXU=0 Radius=1
    g8: Circle CenterX=302.567 CenterY=89.3511 CenterZ=0 NormalX=0 NormalY=0 NormalZ=1 AngleXU=0 Radius=1
    g9: BSplineCurve PolesCount=3 KnotsCount=2 Degree=2 IsPeriodic=0
    g10: GeomPoint X=306.073 Y=95.2763 Z=0
    g11: GeomPoint X=302.567 Y=89.3511 Z=0
    g12: LineSegment StartX=306.073 StartY=110.251 StartZ=0 EndX=306.073 EndY=95.2763 EndZ=0
    g13: Circle CenterX=302.073 CenterY=124.221 CenterZ=0 NormalX=0 NormalY=0 NormalZ=1 AngleXU=0 Radius=1
    g14: Circle CenterX=306.073 CenterY=124.221 CenterZ=0 NormalX=0 NormalY=0 NormalZ=1 AngleXU=0 Radius=1
    g15: Circle CenterX=302.996 CenterY=121.665 CenterZ=0 NormalX=0 NormalY=0 NormalZ=1 AngleXU=0 Radius=1
    g16: BSplineCurve PolesCount=3 KnotsCount=2 Degree=2 IsPeriodic=0
    g17: GeomPoint X=302.073 Y=124.221 Z=0
    g18: GeomPoint X=302.996 Y=121.665 Z=0
    g19: Circle CenterX=306.073 CenterY=73.3346 CenterZ=0 NormalX=0 NormalY=0 NormalZ=1 AngleXU=0 Radius=1
    g20: Circle CenterX=306.073 CenterY=77.3346 CenterZ=0 NormalX=0 NormalY=0 NormalZ=1 AngleXU=0 Radius=1
    g21: Circle CenterX=302.535 CenterY=75.4095 CenterZ=0 NormalX=0 NormalY=0 NormalZ=1 AngleXU=0 Radius=1
    g22: BSplineCurve PolesCount=3 KnotsCount=2 Degree=2 IsPeriodic=0
    g23: GeomPoint X=306.073 Y=73.3346 Z=0
    g24: GeomPoint X=302.535 Y=75.4095 Z=0
    g25: Circle CenterX=362.073 CenterY=124.221 CenterZ=0 NormalX=0 NormalY=0 NormalZ=1 AngleXU=0 Radius=1
    g26: Circle CenterX=366.073 CenterY=124.221 CenterZ=0 NormalX=0 NormalY=0 NormalZ=1 AngleXU=0 Radius=1
    g27: Circle CenterX=362.567 CenterY=122.294 CenterZ=0 NormalX=0 NormalY=0 NormalZ=1 AngleXU=0 Radius=1
    g28: BSplineCurve PolesCount=3 KnotsCount=2 Degree=2 IsPeriodic=0
    g29: GeomPoint X=362.073 Y=124.221 Z=0
    g30: GeomPoint X=362.567 Y=122.294 Z=0
    g31: Circle CenterX=322.073 CenterY=124.221 CenterZ=0 NormalX=0 NormalY=0 NormalZ=1 AngleXU=0 Radius=1
    g32: Circle CenterX=318.073 CenterY=124.221 CenterZ=0 NormalX=0 NormalY=0 NormalZ=1 AngleXU=0 Radius=1
    g33: Circle CenterX=318.073 CenterY=120.221 CenterZ=0 NormalX=0 NormalY=0 NormalZ=1 AngleXU=0 Radius=1
    g34: BSplineCurve PolesCount=3 KnotsCount=2 Degree=2 IsPeriodic=0
    g35: GeomPoint X=322.073 Y=124.221 Z=0
    g36: GeomPoint X=318.073 Y=120.221 Z=0
    g37: Circle CenterX=322.073 CenterY=105.865 CenterZ=0 NormalX=0 NormalY=0 NormalZ=1 AngleXU=0 Radius=1
    g38: Circle CenterX=318.073 CenterY=105.865 CenterZ=0 NormalX=0 NormalY=0 NormalZ=1 AngleXU=0 Radius=1
    g39: Circle CenterX=318.073 CenterY=109.865 CenterZ=0 NormalX=0 NormalY=0 NormalZ=1 AngleXU=0 Radius=1
    g40: BSplineCurve PolesCount=3 KnotsCount=2 Degree=2 IsPeriodic=0
    g41: GeomPoint X=322.073 Y=105.865 Z=0
    g42: GeomPoint X=318.073 Y=109.865 Z=0
    g43: Circle CenterX=336.157 CenterY=107.779 CenterZ=0 NormalX=0 NormalY=0 NormalZ=1 AngleXU=0 Radius=1
    g44: Circle CenterX=332.651 CenterY=105.853 CenterZ=0 NormalX=0 NormalY=0 NormalZ=1 AngleXU=0 Radius=1
    g45: Circle CenterX=328.643 CenterY=105.865 CenterZ=0 NormalX=0 NormalY=0 NormalZ=1 AngleXU=0 Radius=1
    g46: BSplineCurve PolesCount=3 KnotsCount=2 Degree=2 IsPeriodic=0
    g47: GeomPoint X=336.157 Y=107.779 Z=0
    g48: GeomPoint X=328.643 Y=105.865 Z=0
    g49: Circle CenterX=322.073 CenterY=76.4095 CenterZ=0 NormalX=0 NormalY=0 NormalZ=1 AngleXU=0 Radius=4
    g50: BSplineCurve PolesCount=3 KnotsCount=2 Degree=2 IsPeriodic=0
    g51: GeomPoint X=318.073 Y=72.4095 Z=0
    g52: GeomPoint X=322.073 Y=76.4095 Z=0
    g53: Circle CenterX=375.073 CenterY=72.4095 CenterZ=0 NormalX=0 NormalY=0 NormalZ=1 AngleXU=0 Radius=1
    g54: Circle CenterX=375.073 CenterY=76.4095 CenterZ=0 NormalX=0 NormalY=0 NormalZ=1 AngleXU=0 Radius=1
    g55: Circle CenterX=371.073 CenterY=76.4095 CenterZ=0 NormalX=0 NormalY=0 NormalZ=1 AngleXU=0 Radius=1
    g56: BSplineCurve PolesCount=3 KnotsCount=2 Degree=2 IsPeriodic=0
    g57: GeomPoint X=375.073 Y=72.4095 Z=0
    g58: GeomPoint X=371.073 Y=76.4095 Z=0
    g59: LineSegment StartX=322.073 StartY=76.4095 StartZ=0 EndX=371.073 EndY=76.4095 EndZ=0
    g60: Circle CenterX=232.072 CenterY=133.221 CenterZ=0 NormalX=0 NormalY=0 NormalZ=1 AngleXU=0 Radius=1
    g61: Circle CenterX=226.072 CenterY=136.221 CenterZ=0 NormalX=0 NormalY=0 NormalZ=1 AngleXU=0 Radius=1
    g62: Circle CenterX=226.072 CenterY=124.221 CenterZ=0 NormalX=0 NormalY=0 NormalZ=1 AngleXU=0 Radius=1
    g63: Circle CenterX=232.072 CenterY=127.221 CenterZ=0 NormalX=0 NormalY=0 NormalZ=1 AngleXU=0 Radius=1
    g64: BSplineCurve PolesCount=5 KnotsCount=3 Degree=3 IsPeriodic=0
    g65: GeomPoint X=232.072 Y=133.221 Z=0
    g66: GeomPoint X=223.072 Y=130.221 Z=0
    g67: GeomPoint X=232.072 Y=127.221 Z=0
    g68: LineSegment StartX=240.687 StartY=51.8263 StartZ=0 EndX=243.317 EndY=53.2701 EndZ=0
    g69: LineSegment StartX=243.575 StartY=46.5669 StartZ=0 EndX=246.205 EndY=48.0108 EndZ=0
    g70: ArcOfCircle CenterX=247.391 CenterY=52.0843 CenterZ=0 NormalX=0 NormalY=0 NormalZ=1 AngleXU=0 Radius=4.24264 StartAngle=4.42912 EndAngle=9.14151
    g71: LineSegment StartX=243.475 StartY=65.4951 StartZ=0 EndX=245.073 EndY=63.5726 EndZ=0
    g72: LineSegment StartX=243.575 StartY=46.5669 StartZ=0 EndX=245.072 EndY=43.8408 EndZ=0
    g73: LineSegment StartX=245.072 StartY=43.8408 StartZ=0 EndX=302.535 EndY=75.4095 EndZ=0
    g74: LineSegment StartX=239.192 StartY=54.5542 StartZ=0 EndX=302.567 EndY=89.3511 EndZ=0
    g75: LineSegment StartX=232.072 StartY=127.221 StartZ=0 EndX=232.072 EndY=124.221 EndZ=0
    g76: LineSegment StartX=232.072 StartY=136.221 StartZ=0 EndX=232.072 EndY=133.221 EndZ=0
    g77: LineSegment StartX=232.072 StartY=136.221 StartZ=0 EndX=407.073 EndY=136.221 EndZ=0
    g78: LineSegment StartX=322.073 StartY=124.221 StartZ=0 EndX=362.073 EndY=124.221 EndZ=0
    g79: LineSegment StartX=362.567 StartY=122.294 StartZ=0 EndX=336.157 EndY=107.779 EndZ=0
    g80: LineSegment StartX=322.073 StartY=105.865 StartZ=0 EndX=328.643 EndY=105.865 EndZ=0
    g81: LineSegment StartX=318.073 StartY=120.221 StartZ=0 EndX=318.073 EndY=109.865 EndZ=0
    g82: LineSegment StartX=232.072 StartY=124.221 StartZ=0 EndX=302.073 EndY=124.221 EndZ=0
    g83: LineSegment StartX=302.996 StartY=121.665 StartZ=0 EndX=240.171 EndY=69.471 EndZ=0
    g84: LineSegment StartX=240.171 StartY=69.471 StartZ=0 EndX=241.711 EndY=67.6177 EndZ=0
    g85: LineSegment StartX=241.711 StartY=67.6177 StartZ=0 EndX=246.787 EndY=71.8365 EndZ=0
    g86: LineSegment StartX=246.787 StartY=71.8365 StartZ=0 EndX=248.551 EndY=69.712 EndZ=0
    g87: LineSegment StartX=248.551 StartY=69.712 StartZ=0 EndX=243.475 EndY=65.4951 EndZ=0
    g88: LineSegment StartX=245.073 StartY=63.5726 StartZ=0 EndX=302.996 EndY=111.695 EndZ=0
    g89: LineSegment StartX=239.192 StartY=54.5542 StartZ=0 EndX=240.687 EndY=51.8263 EndZ=0
    g90: LineSegment StartX=375.073 StartY=48.2206 StartZ=0 EndX=382.073 EndY=48.2206 EndZ=0
    g91: LineSegment StartX=407.073 StartY=48.2206 StartZ=0 EndX=400.073 EndY=48.2206 EndZ=0
    g92: LineSegment StartX=394.073 StartY=48.2206 StartZ=0 EndX=394.073 EndY=52.2206 EndZ=0
    g93: LineSegment StartX=388.073 StartY=48.2206 StartZ=0 EndX=388.073 EndY=58.2206 EndZ=0
    g94: ArcOfCircle CenterX=385.073 CenterY=61.2206 CenterZ=0 NormalX=0 NormalY=0 NormalZ=1 AngleXU=0 Radius=4.24264 StartAngle=5.49779 EndAngle=10.2102
    g95: ArcOfCircle CenterX=397.073 CenterY=55.2206 CenterZ=0 NormalX=0 NormalY=0 NormalZ=1 AngleXU=0 Radius=4.24264 StartAngle=5.49779 EndAngle=10.2102
    g96: LineSegment StartX=382.073 StartY=58.2206 StartZ=0 EndX=382.073 EndY=48.2206 EndZ=0
    g97: LineSegment StartX=400.073 StartY=52.2206 StartZ=0 EndX=400.073 EndY=48.2206 EndZ=0
    g98: LineSegment StartX=394.073 StartY=48.2206 StartZ=0 EndX=388.073 EndY=48.2206 EndZ=0
    g99: LineSegment StartX=306.073 StartY=-27.5935 StartZ=0 EndX=310.073 EndY=-27.5935 EndZ=0
    g100: LineSegment StartX=318.073 StartY=-27.5935 StartZ=0 EndX=314.073 EndY=-27.5935 EndZ=0
    g101: LineSegment StartX=310.073 StartY=-27.5935 StartZ=0 EndX=310.073 EndY=-31.5935 EndZ=0
    g102: LineSegment StartX=314.073 StartY=-27.5935 StartZ=0 EndX=314.073 EndY=-31.5935 EndZ=0
    g103: ArcOfCircle CenterX=312.073 CenterY=-33.5935 CenterZ=0 NormalX=0 NormalY=0 NormalZ=1 AngleXU=0 Radius=2.82843 StartAngle=2.35619 EndAngle=7.06858
    g104: LineSegment StartX=375.073 StartY=72.4095 StartZ=0 EndX=375.073 EndY=48.2206 EndZ=0
    g105: LineSegment StartX=407.073 StartY=48.2206 StartZ=0 EndX=407.073 EndY=136.221 EndZ=0
    g106: LineSegment StartX=318.073 StartY=-27.5935 StartZ=0 EndX=318.073 EndY=72.4095 EndZ=0
    g107: LineSegment StartX=306.073 StartY=73.3346 StartZ=0 EndX=306.073 EndY=-27.5935 EndZ=0
  constraints (136):
    c: Weight(g0) = 1
    c: Equal(g0,g1)
    c: Equal(g0,g2)
    c: InternalAlignment(g0,g3)
    c: InternalAlignment(g1,g3)
    c: InternalAlignment(g2,g3)
    c: InternalAlignment(g4,g3)
    c: InternalAlignment(g5,g3)
    c: Weight(g6) = 1
    c: Equal(g6,g7)
    c: Equal(g6,g8)
    c: InternalAlignment(g6,g9)
    c: InternalAlignment(g7,g9)
    c: InternalAlignment(g8,g9)
    c: InternalAlignment(g10,g9)
    c: InternalAlignment(g11,g9)
    c: Block(g3)
    c: Block(g9)
    c: Coincident(g12,g3)
    c: Coincident(g12,g9)
    c: Vertical(g12)
    c: Weight(g13) = 1
    c: Equal(g13,g14)
    c: Equal(g13,g15)
    c: InternalAlignment(g14,g16)
    c: InternalAlignment(g15,g16)
    c: InternalAlignment(g17,g16)
    c: InternalAlignment(g18,g16)
    c: Block(g71)
    c: Block(g72)
    c: Coincident(g73,g72)
    c: Coincident(g73,g22)
    c: Block(g73)
    c: Coincident(g70,g69)
    c: Coincident(g70,g68)
    c: Coincident(g74,g9)
    c: Block(g74)
    c: Distance(g71) = 2.5
    c: Block(g64)
    c: Block(g46)
    c: Block(g59)
    c: Coincident(g75,g64)
    c: Vertical(g75)
    c: Coincident(g76,g64)
    c: Vertical(g76)
    c: Coincident(g77,g76)
    c: Horizontal(g77)
    c: Coincident(g78,g34)
    c: Coincident(g78,g28)
    c: Horizontal(g78)
    c: Coincident(g79,g28)
    c: Coincident(g79,g46)
    c: Coincident(g80,g40)
    c: Coincident(g80,g46)
    c: Horizontal(g80)
    c: Coincident(g81,g34)
    c: Coincident(g81,g40)
    c: Vertical(g81)
    c: Block(g34)
    c: Block(g40)
    c: Block(g28)
    c: Coincident(g82,g75)
    c: Coincident(g82,g16)
    c: Horizontal(g82)
    c: Coincident(g83,g16)
    c: Block(g82)
    c: Block(g83)
    c: Block(g16)
    c: Coincident(g84,g83)
    c: Block(g84)
    c: Coincident(g85,g84)
    c: Block(g85)
    c: Coincident(g86,g85)
    c: Coincident(g87,g86)
    c: Coincident(g87,g71)
    c: Block(g87)
    c: Coincident(g88,g71)
    c: Coincident(g88,g3)
    c: Block(g88)
    c: Coincident(g89,g74)
    c: Coincident(g89,g68)
    c: Block(g70)
    c: Block(g68)
    c: Block(g69)
    c: Block(g22)
    c: Block(g50)
    c: Block(g56)
    c: Horizontal(g90)
    c: Distance(g90) = 7
    c: Horizontal(g91)
    c: Distance(g91) = 7
    c: Vertical(g92)
    c: Distance(g92) = 4
    c: Vertical(g93)
    c: Distance(g93) = 10
    c: Coincident(g94,g93)
    c: Coincident(g95,g92)
    c: Block(g95)
    c: Block(g94)
    c: Coincident(g96,g94)
    c: Coincident(g96,g90)
    c: Vertical(g96)
    c: Coincident(g97,g95)
    c: Coincident(g97,g91)
    c: Vertical(g97)
    c: Coincident(g98,g92)
    c: Coincident(g98,g93)
    c: Horizontal(g98)
    c: Horizontal(g99)
    c: Distance(g99) = 4
    c: Horizontal(g100)
    c: Distance(g100) = 4
    c: Coincident(g101,g99)
    c: Vertical(g101)
    c: Coincident(g102,g100)
    c: Vertical(g102)
    c: Distance(g101) = 4
    c: Distance(g102) = 4
    c: Coincident(g103,g101)
    c: Coincident(g103,g102)
    c: Block(g103)
    c: Coincident(g104,g56)
    c: Coincident(g104,g90)
    c: Vertical(g104)
    c: Block(g104)
    c: Coincident(g105,g91)
    c: Coincident(g105,g77)
    c: Vertical(g105)
    c: Block(g77)
    c: Block(g105)
    c: Coincident(g106,g100)
    c: Coincident(g106,g50)
    c: Vertical(g106)
    c: Coincident(g107,g22)
    c: Coincident(g107,g99)
    c: Vertical(g107)
FEATURE [Sketcher::SketchObject] Sketch009  label="middleBottom"
  FullyConstrained = true
  sketch-geometry (109):
    g0: Circle CenterX=175.022 CenterY=5.37834 CenterZ=0 NormalX=0 NormalY=0 NormalZ=1 AngleXU=0 Radius=1
    g1: Circle CenterX=179.022 CenterY=7.57463 CenterZ=0 NormalX=0 NormalY=0 NormalZ=1 AngleXU=0 Radius=1
    g2: Circle CenterX=179.022 CenterY=5.34704 CenterZ=0 NormalX=0 NormalY=0 NormalZ=1 AngleXU=0 Radius=1
    g3: BSplineCurve PolesCount=3 KnotsCount=2 Degree=2 IsPeriodic=0
    g4: GeomPoint X=175.022 Y=5.37834 Z=0
    g5: GeomPoint X=179.022 Y=5.34704 Z=0
    g6: Circle CenterX=189.124 CenterY=5.37834 CenterZ=0 NormalX=0 NormalY=0 NormalZ=1 AngleXU=0 Radius=1
    g7: Circle CenterX=185.124 CenterY=7.57463 CenterZ=0 NormalX=0 NormalY=0 NormalZ=1 AngleXU=0 Radius=1
    g8: Circle CenterX=185.124 CenterY=5.34704 CenterZ=0 NormalX=0 NormalY=0 NormalZ=1 AngleXU=0 Radius=1
    g9: BSplineCurve PolesCount=3 KnotsCount=2 Degree=2 IsPeriodic=0
    g10: GeomPoint X=189.124 Y=5.37834 Z=0
    g11: GeomPoint X=185.124 Y=5.34704 Z=0
    g12: Circle CenterX=224.513 CenterY=-14.0532 CenterZ=0 NormalX=0 NormalY=0 NormalZ=1 AngleXU=0 Radius=1
    g13: Circle CenterX=236.584 CenterY=-24.2775 CenterZ=0 NormalX=0 NormalY=0 NormalZ=1 AngleXU=0 Radius=1
    g14: BSplineCurve PolesCount=3 KnotsCount=2 Degree=2 IsPeriodic=0
    g15: GeomPoint X=236.584 Y=-24.2775 Z=0
    g16: Circle CenterX=125.607 CenterY=-21.7539 CenterZ=0 NormalX=0 NormalY=0 NormalZ=1 AngleXU=0 Radius=1
    g17: Circle CenterX=139.632 CenterY=-14.0532 CenterZ=0 NormalX=0 NormalY=0 NormalZ=1 AngleXU=0 Radius=1
    g18: Circle CenterX=127.325 CenterY=-24.2775 CenterZ=0 NormalX=0 NormalY=0 NormalZ=1 AngleXU=0 Radius=1
    g19: BSplineCurve PolesCount=3 KnotsCount=2 Degree=2 IsPeriodic=0
    g20: GeomPoint X=125.607 Y=-21.7539 Z=0
    g21: GeomPoint X=127.325 Y=-24.2775 Z=0
    g22: Circle CenterX=179.022 CenterY=-85.8163 CenterZ=0 NormalX=0 NormalY=0 NormalZ=1 AngleXU=0 Radius=1
    g23: Circle CenterX=179.022 CenterY=-91.7794 CenterZ=0 NormalX=0 NormalY=0 NormalZ=1 AngleXU=0 Radius=1
    g24: Circle CenterX=171.895 CenterY=-91.8014 CenterZ=0 NormalX=0 NormalY=0 NormalZ=1 AngleXU=0 Radius=1
    g25: BSplineCurve PolesCount=3 KnotsCount=2 Degree=2 IsPeriodic=0
    g26: GeomPoint X=179.022 Y=-85.8163 Z=0
    g27: GeomPoint X=171.895 Y=-91.8014 Z=0
    g28: Circle CenterX=185.124 CenterY=-86.2028 CenterZ=0 NormalX=0 NormalY=0 NormalZ=1 AngleXU=0 Radius=1
    g29: Circle CenterX=185.124 CenterY=-91.7794 CenterZ=0 NormalX=0 NormalY=0 NormalZ=1 AngleXU=0 Radius=1
    g30: Circle CenterX=191.747 CenterY=-91.7794 CenterZ=0 NormalX=0 NormalY=0 NormalZ=1 AngleXU=0 Radius=1
    g31: BSplineCurve PolesCount=3 KnotsCount=2 Degree=2 IsPeriodic=0
    g32: GeomPoint X=185.124 Y=-86.2028 Z=0
    g33: GeomPoint X=191.747 Y=-91.7794 Z=0
    g34: BSplineCurve PolesCount=5 KnotsCount=3 Degree=3 IsPeriodic=0
    g35: LineSegment StartX=132.072 StartY=-100.779 StartZ=0 EndX=132.072 EndY=-103.779 EndZ=0
    g36: GeomPoint X=232.072 Y=-94.7794 Z=0
    g37: GeomPoint X=223.072 Y=-97.7794 Z=0
    g38: Circle CenterX=232.072 CenterY=-94.7794 CenterZ=0 NormalX=0 NormalY=0 NormalZ=1 AngleXU=0 Radius=1
    g39: Circle CenterX=232.072 CenterY=-100.779 CenterZ=0 NormalX=0 NormalY=0 NormalZ=1 AngleXU=0 Radius=1
    g40: BSplineCurve PolesCount=5 KnotsCount=3 Degree=3 IsPeriodic=0
    g41: GeomPoint X=232.072 Y=-100.779 Z=0
    g42: LineSegment StartX=123.656 StartY=-37.1092 StartZ=0 EndX=122.136 EndY=-35.2714 EndZ=0
    g43: LineSegment StartX=117.05 StartY=-39.4781 StartZ=0 EndX=115.291 EndY=-37.3514 EndZ=0
    g44: LineSegment StartX=120.377 StartY=-33.1447 StartZ=0 EndX=118.86 EndY=-31.3104 EndZ=0
    g45: ArcOfCircle CenterX=116.562 CenterY=-19.6236 CenterZ=0 NormalX=0 NormalY=0 NormalZ=1 AngleXU=0 Radius=4.24264 StartAngle=1.28753 EndAngle=5.99992
    g46: LineSegment StartX=240.266 StartY=-37.1092 StartZ=0 EndX=189.124 EndY=5.37834 EndZ=0
    g47: LineSegment StartX=191.747 StartY=-91.7794 StartZ=0 EndX=232.072 EndY=-91.7794 EndZ=0
    g48: LineSegment StartX=232.072 StartY=-91.7794 StartZ=0 EndX=232.072 EndY=-94.7794 EndZ=0
    g49: LineSegment StartX=232.072 StartY=-100.779 StartZ=0 EndX=232.072 EndY=-103.779 EndZ=0
    g50: LineSegment StartX=132.072 StartY=-103.779 StartZ=0 EndX=232.072 EndY=-103.779 EndZ=0
    g51: LineSegment StartX=132.072 StartY=-91.8014 StartZ=0 EndX=132.072 EndY=-94.7791 EndZ=0
    g52: LineSegment StartX=132.072 StartY=-91.8014 StartZ=0 EndX=171.895 EndY=-91.8014 EndZ=0
    g53: LineSegment StartX=179.022 StartY=-85.8163 StartZ=0 EndX=179.022 EndY=5.34704 EndZ=0
    g54: LineSegment StartX=175.022 StartY=5.37834 StartZ=0 EndX=123.656 EndY=-37.1092 EndZ=0
    g55: LineSegment StartX=185.124 StartY=5.34704 StartZ=0 EndX=185.124 EndY=-86.2028 EndZ=0
    g56: LineSegment StartX=122.136 StartY=-35.2714 StartZ=0 EndX=117.05 EndY=-39.4781 EndZ=0
    g57: LineSegment StartX=115.291 StartY=-37.3514 StartZ=0 EndX=120.377 EndY=-33.1447 EndZ=0
    g58: LineSegment StartX=118.86 StartY=-31.3104 StartZ=0 EndX=127.325 EndY=-24.2775 EndZ=0
    g59: LineSegment StartX=125.607 StartY=-21.7539 StartZ=0 EndX=124.815 EndY=-22.1887 EndZ=0
    g60: LineSegment StartX=123.265 StartY=-19.3655 StartZ=0 EndX=124.815 EndY=-22.1887 EndZ=0
    g61: LineSegment StartX=120.636 StartY=-20.8094 StartZ=0 EndX=123.265 EndY=-19.3655 EndZ=0
    g62: LineSegment StartX=117.748 StartY=-15.55 StartZ=0 EndX=120.377 EndY=-14.1062 EndZ=0
    g63: LineSegment StartX=120.377 StartY=-14.1062 StartZ=0 EndX=118.934 EndY=-11.4765 EndZ=0
    g64: LineSegment StartX=236.584 StartY=-24.2775 StartZ=0 EndX=245.072 EndY=-31.3037 EndZ=0
    g65: LineSegment StartX=245.072 StartY=-31.3037 StartZ=0 EndX=243.535 EndY=-33.1602 EndZ=0
    g66: LineSegment StartX=243.535 StartY=-33.1602 StartZ=0 EndX=248.619 EndY=-37.3688 EndZ=0
    g67: LineSegment StartX=248.619 StartY=-37.3688 StartZ=0 EndX=246.855 EndY=-39.5064 EndZ=0
    g68: LineSegment StartX=246.855 StartY=-39.5064 StartZ=0 EndX=241.778 EndY=-35.2889 EndZ=0
    g69: LineSegment StartX=241.778 StartY=-35.2889 StartZ=0 EndX=240.266 EndY=-37.1092 EndZ=0
    g70: LineSegment StartX=243.628 StartY=-14.0323 StartZ=0 EndX=246.258 EndY=-15.476 EndZ=0
    g71: LineSegment StartX=240.741 StartY=-19.2917 StartZ=0 EndX=243.37 EndY=-20.7355 EndZ=0
    g72: ArcOfCircle CenterX=247.444 CenterY=-19.5496 CenterZ=0 NormalX=0 NormalY=0 NormalZ=1 AngleXU=0 Radius=4.24264 StartAngle=3.4249 EndAngle=8.13729
    g73: LineSegment StartX=240.741 StartY=-19.2917 StartZ=0 EndX=239.201 EndY=-22.0968 EndZ=0
    g74: LineSegment StartX=238.538 StartY=-21.7516 StartZ=0 EndX=239.201 EndY=-22.0968 EndZ=0
    g75: LineSegment StartX=245.072 StartY=-11.4025 StartZ=0 EndX=243.628 EndY=-14.0323 EndZ=0
    g76-g91: Circle x16 (B-spline internal-alignment scaffolding for g92; pole/knot coordinates omitted)
    g92: BSplineCurve PolesCount=16 KnotsCount=14 Degree=3 IsPeriodic=0
    g93-g106: GeomPoint x14 (B-spline internal-alignment scaffolding for g92; pole/knot coordinates omitted)
    g107: LineSegment StartX=165.871 StartY=14.2956 StartZ=0 EndX=118.934 EndY=-11.4765 EndZ=0
    g108: LineSegment StartX=198.264 StartY=14.2963 StartZ=0 EndX=245.072 EndY=-11.4025 EndZ=0
  constraints (146):
    c: Weight(g0) = 1
    c: Equal(g0,g1)
    c: Equal(g0,g2)
    c: InternalAlignment(g0,g3)
    c: InternalAlignment(g1,g3)
    c: InternalAlignment(g2,g3)
    c: InternalAlignment(g4,g3)
    c: InternalAlignment(g5,g3)
    c: Weight(g6) = 1
    c: Equal(g6,g7)
    c: Equal(g6,g8)
    c: InternalAlignment(g6,g9)
    c: InternalAlignment(g7,g9)
    c: InternalAlignment(g8,g9)
    c: InternalAlignment(g10,g9)
    c: InternalAlignment(g11,g9)
    c: Block(g9)
    c: Block(g3)
    c: InternalAlignment(g12,g14)
    c: InternalAlignment(g13,g14)
    c: InternalAlignment(g15,g14)
    c: Block(g14)
    c: Weight(g16) = 1
    c: Equal(g16,g17)
    c: Equal(g16,g18)
    c: InternalAlignment(g16,g19)
    c: InternalAlignment(g17,g19)
    c: InternalAlignment(g18,g19)
    c: InternalAlignment(g20,g19)
    c: InternalAlignment(g21,g19)
    c: Block(g19)
    c: Weight(g22) = 1
    c: Equal(g22,g23)
    c: Equal(g22,g24)
    c: InternalAlignment(g22,g25)
    c: InternalAlignment(g23,g25)
    c: InternalAlignment(g24,g25)
    c: InternalAlignment(g26,g25)
    c: InternalAlignment(g27,g25)
    c: Weight(g28) = 1
    c: Equal(g28,g29)
    c: Equal(g28,g30)
    c: InternalAlignment(g28,g31)
    c: InternalAlignment(g29,g31)
    c: InternalAlignment(g30,g31)
    c: InternalAlignment(g32,g31)
    c: InternalAlignment(g33,g31)
    c: Block(g31)
    c: Block(g25)
    c: Block(g34)
    c: Coincident(g35,g34)
    c: Vertical(g35)
    c: Block(g35)
    c: Equal(g38,g39)
    c: InternalAlignment(g38,g40)
    c: InternalAlignment(g39,g40)
    c: InternalAlignment(g36,g40)
    c: InternalAlignment(g37,g40)
    c: InternalAlignment(g41,g40)
    c: Block(g40)
    c: Distance(g42) = 2.385
    c: Distance(g43) = 2.76
    c: Parallel(g42,g44)
    c: Block(g45)
    c: Coincident(g46,g9)
    c: Coincident(g47,g31)
    c: Horizontal(g47)
    c: Block(g47)
    c: Coincident(g48,g47)
    c: Coincident(g48,g40)
    c: Vertical(g48)
    c: Block(g48)
    c: Coincident(g49,g40)
    c: Vertical(g49)
    c: Block(g49)
    c: Coincident(g50,g35)
    c: Coincident(g50,g49)
    c: Horizontal(g50)
    c: Block(g50)
    c: Coincident(g51,g34)
    c: Vertical(g51)
    c: Coincident(g52,g51)
    c: Coincident(g52,g25)
    c: Horizontal(g52)
    c: Coincident(g53,g25)
    c: Coincident(g53,g3)
    c: Vertical(g53)
    c: Coincident(g54,g3)
    c: Coincident(g54,g42)
    c: Coincident(g55,g9)
    c: Coincident(g55,g31)
    c: Vertical(g55)
    c: Block(g42)
    c: Coincident(g56,g42)
    c: Coincident(g56,g43)
    c: Coincident(g57,g43)
    c: Coincident(g57,g44)
    c: Block(g57)
    c: Block(g56)
    c: Coincident(g58,g44)
    c: Coincident(g58,g19)
    c: Block(g58)
    c: Coincident(g59,g19)
    c: Block(g59)
    c: Coincident(g60,g59)
    c: Block(g60)
    c: Coincident(g61,g45)
    c: Coincident(g61,g60)
    c: Coincident(g62,g45)
    c: Coincident(g63,g62)
    c: Block(g63)
    c: Coincident(g64,g14)
    c: Block(g64)
    c: Coincident(g65,g64)
    c: Coincident(g66,g65)
    c: Coincident(g67,g66)
    c: Coincident(g68,g67)
    c: Coincident(g69,g68)
    c: Coincident(g69,g46)
    c: Block(g46)
    c: Block(g68)
    c: Block(g66)
    c: Distance(g70) = 3
    c: Distance(g71) = 3
    c: Coincident(g72,g70)
    c: Coincident(g72,g71)
    c: Block(g72)
    c: Coincident(g73,g71)
    c: Distance(g73) = 3.2
    c: Coincident(g74,g14)
    c: Coincident(g74,g73)
    c: Coincident(g75,g70)
    c: Block(g75)
    c: Block(g73)
    c: Distance(g63) = 3
    c: Distance(g60) = 3.22077
    c: Weight(g76) = 1
    c: Equal(g76, g77-g91) x15
    c: InternalAlignment(g76-g91 -> g92) x16
    c: InternalAlignment(g93-g106 -> g92) x14
    c: Coincident(g107,g92)
    c: Coincident(g107,g63)
    c: Block(g107)
    c: Block(g92)
    c: Coincident(g108,g92)
    c: Coincident(g108,g75)
FEATURE [Sketcher::SketchObject] Sketch010  label="legBottomBack"
  FullyConstrained = true
  MapMode = 4
  Placement = pos=(0,0,0) rot=(0.57735,0.57735,0.57735;2.0944rad)
  sketch-geometry (76):
    g0: Circle CenterX=-17.0256 CenterY=-190.268 CenterZ=0 NormalX=0 NormalY=0 NormalZ=1 AngleXU=0 Radius=10.5072
    g1: Circle CenterX=-37.7758 CenterY=-187.672 CenterZ=0 NormalX=0 NormalY=0 NormalZ=1 AngleXU=0 Radius=5.64388
    g2: Circle CenterX=-51.4606 CenterY=-185.091 CenterZ=0 NormalX=0 NormalY=0 NormalZ=1 AngleXU=0 Radius=3.01653
    g3: Circle CenterX=-60.4835 CenterY=-182.688 CenterZ=0 NormalX=0 NormalY=0 NormalZ=1 AngleXU=0 Radius=2.12826
    g4: Circle CenterX=-3.29005 CenterY=-177.662 CenterZ=0 NormalX=0 NormalY=0 NormalZ=1 AngleXU=0 Radius=3.26661
    g5: ArcOfCircle CenterX=11.0205 CenterY=-198.019 CenterZ=0 NormalX=0 NormalY=0 NormalZ=1 AngleXU=0 Radius=13 StartAngle=2.78068 EndAngle=5.92131
    g6: LineSegment StartX=5.08312 StartY=-176.581 StartZ=0 EndX=-1.14188 EndY=-193.429 EndZ=0
    g7: ArcOfCircle CenterX=17.2475 CenterY=-181.166 CenterZ=0 NormalX=0 NormalY=0 NormalZ=1 AngleXU=0 Radius=13 StartAngle=1.21042 EndAngle=2.78109
    g8: LineSegment StartX=38.8952 StartY=-231.233 StartZ=0 EndX=39.9512 EndY=-228.425 EndZ=0
    g9: ArcOfCircle CenterX=46.9911 CenterY=-209.705 CenterZ=0 NormalX=0 NormalY=0 NormalZ=1 AngleXU=0 Radius=20 StartAngle=2.78766 EndAngle=4.35269
    g10: LineSegment StartX=23.7323 StartY=-126.969 StartZ=0 EndX=17.4091 EndY=-143.817 EndZ=0
    g11: ArcOfCircle CenterX=29.5716 CenterY=-148.408 CenterZ=0 NormalX=0 NormalY=0 NormalZ=1 AngleXU=0 Radius=13 StartAngle=2.78068 EndAngle=4.35262
    g12: ArcOfCircle CenterX=35.8967 CenterY=-131.555 CenterZ=0 NormalX=0 NormalY=0 NormalZ=1 AngleXU=0 Radius=13 StartAngle=1.21584 EndAngle=2.78109
    g13: ArcOfCircle CenterX=48.1805 CenterY=-98.7782 CenterZ=0 NormalX=0 NormalY=0 NormalZ=1 AngleXU=0 Radius=13 StartAngle=2.78068 EndAngle=4.35005
    g14: LineSegment StartX=42.354 StartY=-77.3391 StartZ=0 EndX=36.018 EndY=-94.1875 EndZ=0
    g15: ArcOfCircle CenterX=54.5183 CenterY=-81.9247 CenterZ=0 NormalX=0 NormalY=0 NormalZ=1 AngleXU=0 Radius=13 StartAngle=2.42113 EndAngle=2.78109
    g16: ArcOfCircle CenterX=20.184 CenterY=-217.506 CenterZ=0 NormalX=0 NormalY=0 NormalZ=1 AngleXU=0 Radius=3.81084 StartAngle=1.88136 EndAngle=6.80465
    g17: LineSegment StartX=38.4753 StartY=-115.966 StartZ=0 EndX=41.2852 EndY=-117.017 EndZ=0
    g18: ArcOfCircle CenterX=36.3663 CenterY=-113.042 CenterZ=0 NormalX=0 NormalY=0 NormalZ=1 AngleXU=0 Radius=3.60555 StartAngle=0.230024 EndAngle=5.3372
    g19: LineSegment StartX=39.8769 StartY=-112.22 StartZ=0 EndX=42.6867 EndY=-113.271 EndZ=0
    g20: LineSegment StartX=19.9036 StartY=-165.61 StartZ=0 EndX=22.7134 EndY=-166.661 EndZ=0
    g21: ArcOfCircle CenterX=17.7945 CenterY=-162.686 CenterZ=0 NormalX=0 NormalY=0 NormalZ=1 AngleXU=0 Radius=3.60555 StartAngle=0.230024 EndAngle=5.3372
    g22: LineSegment StartX=21.3051 StartY=-161.864 StartZ=0 EndX=24.1149 EndY=-162.915 EndZ=0
    g23: LineSegment StartX=41.085 StartY=-66.3176 StartZ=0 EndX=46.0385 EndY=-62.5254 EndZ=0
    g24: LineSegment StartX=48.9563 StartY=-66.3367 StartZ=0 EndX=44.7488 EndY=-73.3482 EndZ=0
    g25: ArcOfCircle CenterX=49.8795 CenterY=-62.6074 CenterZ=0 NormalX=0 NormalY=0 NormalZ=1 AngleXU=0 Radius=3.84187 StartAngle=4.46973 EndAngle=9.40343
    g26: LineSegment StartX=43.5724 StartY=-110.934 StartZ=0 EndX=42.6867 EndY=-113.271 EndZ=0
    g27: LineSegment StartX=40.4148 StartY=-119.365 StartZ=0 EndX=41.2852 EndY=-117.017 EndZ=0
    g28: LineSegment StartX=21.8316 StartY=-169.001 StartZ=0 EndX=22.7134 EndY=-166.661 EndZ=0
    g29: LineSegment StartX=24.9948 StartY=-160.575 StartZ=0 EndX=24.1149 EndY=-162.915 EndZ=0
    g30: LineSegment StartX=23.1786 StartY=-202.622 StartZ=0 EndX=19.0195 EndY=-213.878 EndZ=0
    g31: LineSegment StartX=28.2308 StartY=-202.773 StartZ=0 EndX=23.4884 EndY=-215.608 EndZ=0
    g32: LineSegment StartX=-76.2249 StartY=-179.393 StartZ=0 EndX=-72.8553 EndY=-180.66 EndZ=0
    g33: ArcOfCircle CenterX=-71.1257 CenterY=-183.448 CenterZ=0 NormalX=0 NormalY=0 NormalZ=1 AngleXU=0 Radius=3.28025 StartAngle=3.43759 EndAngle=8.40938
    g34: LineSegment StartX=-79.0409 StartY=-186.881 StartZ=0 EndX=38.8952 EndY=-231.233 EndZ=0
    g35-g53: Circle x19 (B-spline internal-alignment scaffolding for g54; pole/knot coordinates omitted)
    g54: BSplineCurve PolesCount=19 KnotsCount=17 Degree=3 IsPeriodic=0
    g55-g71: GeomPoint x17 (B-spline internal-alignment scaffolding for g54; pole/knot coordinates omitted)
    g72: LineSegment StartX=-74.2633 StartY=-184.404 StartZ=0 EndX=-77.6329 EndY=-183.137 EndZ=0
    g73: LineSegment StartX=-79.0409 StartY=-186.881 StartZ=0 EndX=-77.6329 EndY=-183.137 EndZ=0
    g74: LineSegment StartX=8.65492 StartY=-152.553 StartZ=0 EndX=41.085 EndY=-66.3176 EndZ=0
    g75: LineSegment StartX=-74.4658 StartY=-174.715 StartZ=0 EndX=-76.2249 EndY=-179.393 EndZ=0
  constraints (76):
    c: Block(g5)
    c: Block(g7)
    c: Block(g0)
    c: Block(g4)
    c: Block(g1)
    c: Block(g2)
    c: Block(g3)
    c: Block(g9)
    c: Coincident(g8,g9)
    c: Block(g8)
    c: Coincident(g6,g7)
    c: Coincident(g6,g5)
    c: Block(g11)
    c: Block(g12)
    c: Coincident(g10,g12)
    c: Coincident(g10,g11)
    c: Block(g13)
    c: Block(g15)
    c: Coincident(g14,g15)
    c: Coincident(g14,g13)
    c: Block(g16)
    c: Block(g18)
    c: Coincident(g19,g18)
    c: Coincident(g17,g18)
    c: Parallel(g19,g17)
    c: Block(g17)
    c: Block(g19)
    c: Block(g21)
    c: Coincident(g22,g21)
    c: Coincident(g20,g21)
    c: Parallel(g22,g20)
    c: Block(g20)
    c: Block(g22)
    c: Block(g23)
    c: Coincident(g25,g23)
    c: Coincident(g25,g24)
    c: Block(g25)
    c: Block(g24)
    c: Coincident(g26,g19)
    c: Block(g26)
    c: Coincident(g27,g17)
    c: Block(g27)
    c: Coincident(g28,g20)
    c: Coincident(g29,g22)
    c: Block(g29)
    c: Block(g28)
    c: Coincident(g30,g5)
    c: Coincident(g30,g16)
    c: Block(g30)
    c: Coincident(g7,g28)
    c: Coincident(g11,g29)
    c: Coincident(g12,g27)
    c: Coincident(g13,g26)
    c: Coincident(g15,g24)
    c: Coincident(g31,g9)
    c: Coincident(g31,g16)
    c: Distance(g32) = 3.6
    c: Block(g32)
    c: Coincident(g33,g32)
    c: Coincident(g34,g8)
    c: Weight(g35) = 1
    c: Equal(g35, g36-g53) x18
    c: InternalAlignment(g35-g53 -> g54) x19
    c: InternalAlignment(g55-g71 -> g54) x17
    c: Block(g33)
    c: Block(g54)
    c: Coincident(g72,g33)
    c: Coincident(g73,g34)
    c: Block(g34)
    c: Parallel(g72,g34)
    c: Perpendicular(g73,g34)
    c: Coincident(g72,g73)
    c: Coincident(g74,g54)
    c: Coincident(g74,g23)
    c: Coincident(g75,g54)
    c: Coincident(g75,g32)
FEATURE [Sketcher::SketchObject] Sketch011  label="legBottomFront"
  FullyConstrained = true
  MapMode = 4
  Placement = pos=(0,0,0) rot=(0.57735,0.57735,0.57735;2.0944rad)
  sketch-geometry (13):
    g0: LineSegment StartX=-199.665 StartY=-138.314 StartZ=0 EndX=-200.721 EndY=-141.122 EndZ=0
    g1: LineSegment StartX=-200.721 StartY=-141.122 StartZ=0 EndX=-79.0409 EndY=-186.881 EndZ=0
    g2: ArcOfCircle CenterX=-71.1257 CenterY=-183.448 CenterZ=0 NormalX=0 NormalY=0 NormalZ=1 AngleXU=0 Radius=3.28025 StartAngle=3.43759 EndAngle=8.40938
    g3: LineSegment StartX=-74.4626 StartY=-174.707 StartZ=0 EndX=-76.2249 EndY=-179.393 EndZ=0
    g4: LineSegment StartX=-76.2249 StartY=-179.393 StartZ=0 EndX=-72.8553 EndY=-180.66 EndZ=0
    g5: Circle CenterX=-74.4626 CenterY=-174.707 CenterZ=0 NormalX=0 NormalY=0 NormalZ=1 AngleXU=0 Radius=1
    g6: Circle CenterX=-130.185 CenterY=-164.454 CenterZ=0 NormalX=0 NormalY=0 NormalZ=1 AngleXU=0 Radius=1
    g7: Circle CenterX=-199.665 CenterY=-138.314 CenterZ=0 NormalX=0 NormalY=0 NormalZ=1 AngleXU=0 Radius=1
    g8: BSplineCurve PolesCount=3 KnotsCount=2 Degree=2 IsPeriodic=0
    g9: GeomPoint X=-74.4626 Y=-174.707 Z=0
    g10: GeomPoint X=-199.665 Y=-138.314 Z=0
    g11: LineSegment StartX=-77.6329 StartY=-183.137 StartZ=0 EndX=-79.0409 EndY=-186.881 EndZ=0
    g12: LineSegment StartX=-77.6329 StartY=-183.137 StartZ=0 EndX=-74.2633 EndY=-184.404 EndZ=0
  constraints (24):
    c: Coincident(g1,g0)
    c: Block(g0)
    c: Perpendicular(g1,g0)
    c: Distance(g1) = 130
    c: Coincident(g4,g3)
    c: Coincident(g4,g2)
    c: Block(g2)
    c: Block(g4)
    c: Coincident(g8,g3)
    c: Weight(g5) = 1
    c: Equal(g5,g6)
    c: Equal(g5,g7)
    c: Coincident(g8,g0)
    c: InternalAlignment(g5,g8)
    c: InternalAlignment(g6,g8)
    c: InternalAlignment(g7,g8)
    c: InternalAlignment(g9,g8)
    c: InternalAlignment(g10,g8)
    c: Block(g8)
    c: Block(g3)
    c: Coincident(g11,g1)
    c: Coincident(g12,g11)
    c: Coincident(g12,g2)
    c: Block(g12)
FEATURE [Sketcher::SketchObject] Sketch
  FullyConstrained = true
  Placement = pos=(0,0,0) rot=(-1,0,0;4.71239rad)
  sketch-geometry (13):
    g0: LineSegment StartX=19.9194 StartY=-5.9387 StartZ=0 EndX=79.9194 EndY=-5.9387 EndZ=0
    g1: LineSegment StartX=19.9194 StartY=-115.939 StartZ=0 EndX=24.9194 EndY=-115.939 EndZ=0
    g2: LineSegment StartX=79.9194 StartY=-5.9387 StartZ=0 EndX=79.9194 EndY=-10.9387 EndZ=0
    g3: Circle CenterX=79.9194 CenterY=-10.9387 CenterZ=0 NormalX=0 NormalY=0 NormalZ=1 AngleXU=0 Radius=1
    g4: Circle CenterX=24.9194 CenterY=-10.9387 CenterZ=0 NormalX=0 NormalY=0 NormalZ=1 AngleXU=0 Radius=1
    g5: Circle CenterX=24.9194 CenterY=-115.939 CenterZ=0 NormalX=0 NormalY=0 NormalZ=1 AngleXU=0 Radius=1
    g6: BSplineCurve PolesCount=3 KnotsCount=2 Degree=2 IsPeriodic=0
    g7: GeomPoint X=79.9194 Y=-10.9387 Z=0
    g8: GeomPoint X=24.9194 Y=-115.939 Z=0
    g9: LineSegment StartX=19.9194 StartY=-5.9387 StartZ=0 EndX=19.9194 EndY=-115.939 EndZ=0
    g10: Circle CenterX=33.6194 CenterY=-19.6387 CenterZ=0 NormalX=0 NormalY=0 NormalZ=1 AngleXU=0 Radius=8.7
    g11: Circle CenterX=28.8194 CenterY=-36.6387 CenterZ=0 NormalX=0 NormalY=0 NormalZ=1 AngleXU=0 Radius=3.9
    g12: Circle CenterX=48.6194 CenterY=-13.5387 CenterZ=0 NormalX=0 NormalY=0 NormalZ=1 AngleXU=0 Radius=2.6
  constraints (26):
    c: Horizontal(g0)
    c: Distance(g0) = 60
    c: Horizontal(g1)
    c: Distance(g1) = 5
    c: Coincident(g2,g0)
    c: Vertical(g2)
    c: Distance(g2) = 5
    c: Coincident(g6,g2)
    c: Weight(g3) = 1
    c: Equal(g3,g4)
    c: Equal(g3,g5)
    c: Coincident(g6,g1)
    c: InternalAlignment(g3,g6)
    c: InternalAlignment(g4,g6)
    c: InternalAlignment(g5,g6)
    c: InternalAlignment(g7,g6)
    c: InternalAlignment(g8,g6)
    c: Coincident(g9,g0)
    c: Coincident(g9,g1)
    c: Vertical(g9)
    c: Block(g4)
    c: Block(g10)
    c: Block(g6)
    c: Block(g0)
    c: Block(g11)
    c: Block(g12)
